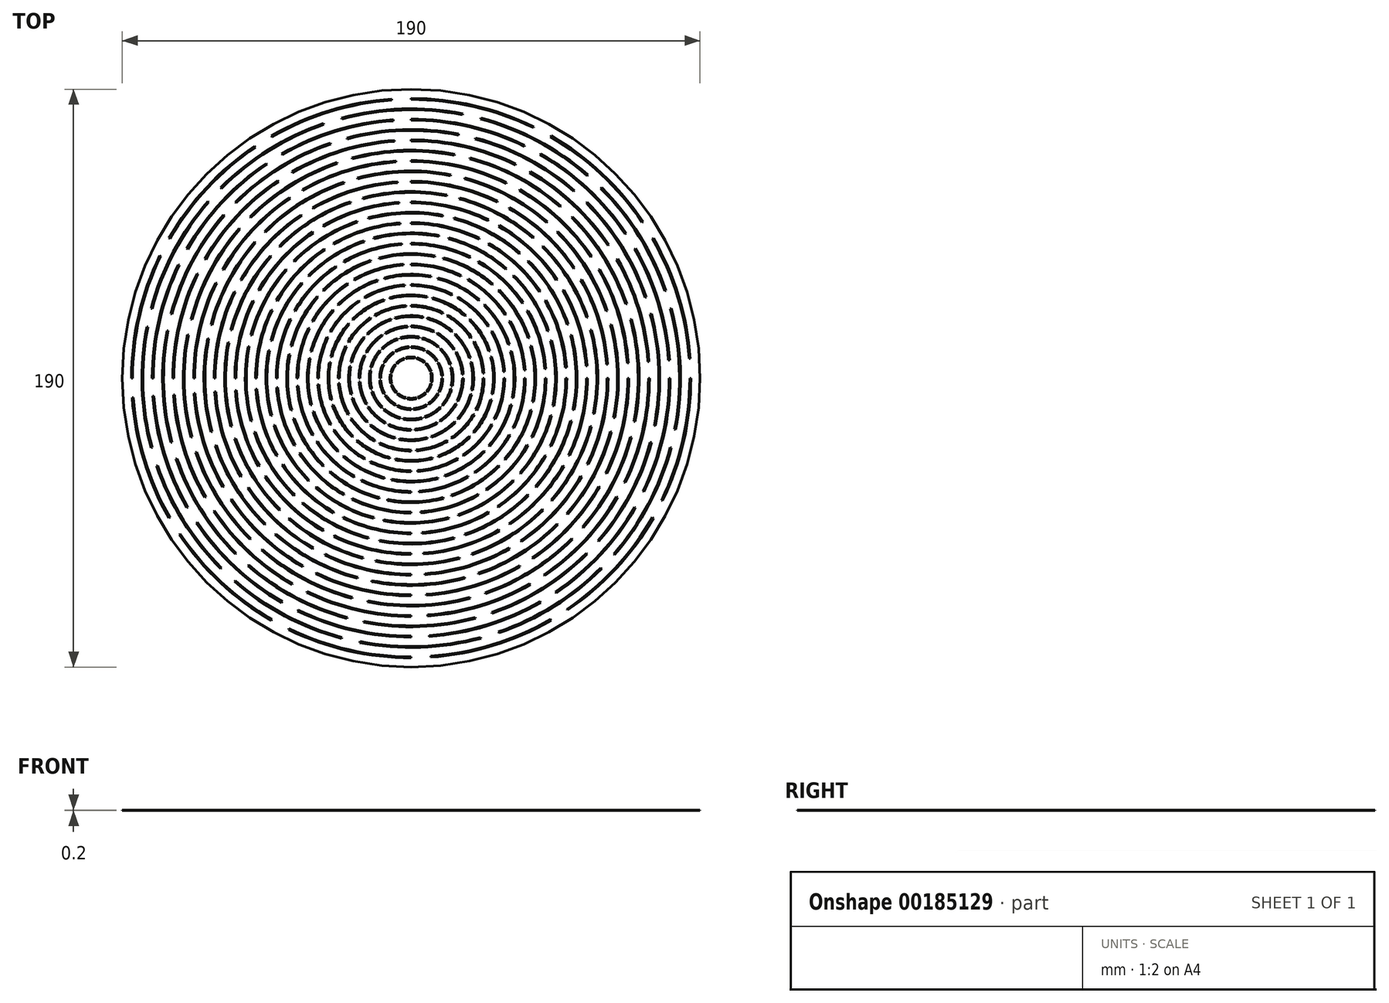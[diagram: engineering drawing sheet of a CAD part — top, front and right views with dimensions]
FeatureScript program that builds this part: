
annotation { "Feature Type Name" : "Feature", "Feature Type Description" : "" }
export const myFeature = defineFeature(function(context is Context, id is Id, definition is map)
    precondition{}
    {
        {
            assignVariable(context, id + "F0", {"name" : "T", "anyValue" : 0.2});
        }
        {
            var Q0;
            Q0=qCreatedBy(makeId("Top.planeOp"),FACE);
            var sketch = newSketch(context, id + "F1", { "sketchPlane" : qUnion([Q0])});
            skCircle(sketch, "E0", {"center": v(0, 0) * mm, "radius": 95 * mm});
            skPoint(sketch, "E1", {"position": v(-95, 0) * mm});
            skPoint(sketch, "E2", {"position": v(-92, 0) * mm});
            skPoint(sketch, "E3.1.0.0", {"position": v(-88.6, 0) * mm});
            skPoint(sketch, "E3.1.0.1", {"position": v(-91.6, 0) * mm});
            skPoint(sketch, "E3.2.0.0", {"position": v(-85.2, 0) * mm});
            skPoint(sketch, "E3.2.0.1", {"position": v(-88.2, 0) * mm});
            skPoint(sketch, "E3.3.0.0", {"position": v(-81.8, 0) * mm});
            skPoint(sketch, "E3.3.0.1", {"position": v(-84.8, 0) * mm});
            skPoint(sketch, "E3.4.0.0", {"position": v(-78.4, 0) * mm});
            skPoint(sketch, "E3.4.0.1", {"position": v(-81.4, 0) * mm});
            skPoint(sketch, "E3.5.0.0", {"position": v(-75, 0) * mm});
            skPoint(sketch, "E3.5.0.1", {"position": v(-78, 0) * mm});
            skPoint(sketch, "E3.6.0.0", {"position": v(-71.6, 0) * mm});
            skPoint(sketch, "E3.6.0.1", {"position": v(-74.6, 0) * mm});
            skPoint(sketch, "E3.7.0.0", {"position": v(-68.2, 0) * mm});
            skPoint(sketch, "E3.7.0.1", {"position": v(-71.2, 0) * mm});
            skPoint(sketch, "E3.8.0.0", {"position": v(-64.8, 0) * mm});
            skPoint(sketch, "E3.8.0.1", {"position": v(-67.8, 0) * mm});
            skPoint(sketch, "E3.9.0.0", {"position": v(-61.4, 0) * mm});
            skPoint(sketch, "E3.9.0.1", {"position": v(-64.4, 0) * mm});
            skPoint(sketch, "E3.10.0.0", {"position": v(-58, 0) * mm});
            skPoint(sketch, "E3.10.0.1", {"position": v(-61, 0) * mm});
            skPoint(sketch, "E3.11.0.0", {"position": v(-54.6, 0) * mm});
            skPoint(sketch, "E3.11.0.1", {"position": v(-57.6, 0) * mm});
            skPoint(sketch, "E3.12.0.0", {"position": v(-51.2, 0) * mm});
            skPoint(sketch, "E3.12.0.1", {"position": v(-54.2, 0) * mm});
            skPoint(sketch, "E3.13.0.0", {"position": v(-47.8, 0) * mm});
            skPoint(sketch, "E3.13.0.1", {"position": v(-50.8, 0) * mm});
            skPoint(sketch, "E3.14.0.0", {"position": v(-44.4, 0) * mm});
            skPoint(sketch, "E3.14.0.1", {"position": v(-47.4, 0) * mm});
            skPoint(sketch, "E3.15.0.0", {"position": v(-41, 0) * mm});
            skPoint(sketch, "E3.15.0.1", {"position": v(-44, 0) * mm});
            skPoint(sketch, "E3.16.0.0", {"position": v(-37.6, 0) * mm});
            skPoint(sketch, "E3.16.0.1", {"position": v(-40.6, 0) * mm});
            skPoint(sketch, "E3.17.0.0", {"position": v(-34.2, 0) * mm});
            skPoint(sketch, "E3.17.0.1", {"position": v(-37.2, 0) * mm});
            skPoint(sketch, "E3.18.0.0", {"position": v(-30.8, 0) * mm});
            skPoint(sketch, "E3.18.0.1", {"position": v(-33.8, 0) * mm});
            skPoint(sketch, "E3.19.0.0", {"position": v(-27.4, 0) * mm});
            skPoint(sketch, "E3.19.0.1", {"position": v(-30.4, 0) * mm});
            skPoint(sketch, "E3.20.0.0", {"position": v(-24, 0) * mm});
            skPoint(sketch, "E3.20.0.1", {"position": v(-27, 0) * mm});
            skPoint(sketch, "E3.21.0.0", {"position": v(-20.6, 0) * mm});
            skPoint(sketch, "E3.21.0.1", {"position": v(-23.6, 0) * mm});
            skPoint(sketch, "E3.22.0.0", {"position": v(-17.2, 0) * mm});
            skPoint(sketch, "E3.22.0.1", {"position": v(-20.2, 0) * mm});
            skPoint(sketch, "E3.23.0.0", {"position": v(-13.8, 0) * mm});
            skPoint(sketch, "E3.23.0.1", {"position": v(-16.8, 0) * mm});
            skPoint(sketch, "E3.24.0.0", {"position": v(-10.4, 0) * mm});
            skPoint(sketch, "E3.24.0.1", {"position": v(-13.4, 0) * mm});
            skPoint(sketch, "E3.25.0.0", {"position": v(-7, 0) * mm});
            skPoint(sketch, "E3.25.0.1", {"position": v(-10, 0) * mm});
            skLineSegment(sketch, "E3.direction1", {"start": v(-95, 0) * mm, "end": v(-91.6, 0) * mm, "construction": true});
            skArc(sketch, "E4", {"start": v(-92, 0) * mm, "mid": v(-89.64, 20.7) * mm, "end": v(-82.69, 40.33) * mm});
            skLineSegment(sketch, "E5", {"start": v(-82.69, 40.33) * mm, "end": v(0, 0) * mm, "construction": true});
            skLineSegment(sketch, "E6", {"start": v(0, 0) * mm, "end": v(-95, 0) * mm, "construction": true});
            skArc(sketch, "E7", {"start": v(-91.6, 0) * mm, "mid": v(-89.25, 20.6) * mm, "end": v(-82.33, 40.15) * mm});
            skLineSegment(sketch, "E8", {"start": v(-92, 0) * mm, "end": v(-91.6, 0) * mm});
            skLineSegment(sketch, "E9", {"start": v(-82.69, 40.33) * mm, "end": v(-82.33, 40.15) * mm});
            skArc(sketch, "E10", {"start": v(-88.6, 0) * mm, "mid": v(-88.2, 8.5) * mm, "end": v(-86.97, 16.9) * mm});
            skArc(sketch, "E11", {"start": v(-88.6, 0) * mm, "mid": v(-87.84, -11.56) * mm, "end": v(-85.58, -22.93) * mm});
            skLineSegment(sketch, "E12", {"start": v(-86.97, 16.9) * mm, "end": v(0, 0) * mm, "construction": true});
            skLineSegment(sketch, "E13", {"start": v(0, 0) * mm, "end": v(-85.58, -22.93) * mm, "construction": true});
            skArc(sketch, "E14", {"start": v(-88.2, 0) * mm, "mid": v(-87.8, 8.45) * mm, "end": v(-86.58, 16.83) * mm});
            skArc(sketch, "E15", {"start": v(-88.2, 0) * mm, "mid": v(-87.45, -11.51) * mm, "end": v(-85.2, -22.83) * mm});
            skLineSegment(sketch, "E16", {"start": v(-86.97, 16.9) * mm, "end": v(-86.58, 16.83) * mm});
            skLineSegment(sketch, "E17", {"start": v(-85.58, -22.93) * mm, "end": v(-85.2, -22.83) * mm});
            skArc(sketch, "E18", {"start": v(-85.2, 0) * mm, "mid": v(-83.02, 19.17) * mm, "end": v(-76.58, 37.35) * mm});
            skArc(sketch, "E19", {"start": v(-84.8, 0) * mm, "mid": v(-82.63, 19.08) * mm, "end": v(-76.22, 37.17) * mm});
            skLineSegment(sketch, "E20", {"start": v(-76.58, 37.35) * mm, "end": v(-76.22, 37.17) * mm});
            skLineSegment(sketch, "E21", {"start": v(-85.2, 0) * mm, "end": v(-84.8, 0) * mm});
            skArc(sketch, "E22", {"start": v(-81.8, 0) * mm, "mid": v(-81.42, 7.84) * mm, "end": v(-80.3, 15.6) * mm});
            skArc(sketch, "E23", {"start": v(-81.8, 0) * mm, "mid": v(-81.1, -10.68) * mm, "end": v(-79.01, -21.17) * mm});
            skArc(sketch, "E24", {"start": v(-81.4, 0) * mm, "mid": v(-81.03, 7.8) * mm, "end": v(-79.9, 15.53) * mm});
            skArc(sketch, "E25", {"start": v(-81.4, 0) * mm, "mid": v(-80.7, -10.62) * mm, "end": v(-78.63, -21.07) * mm});
            skLineSegment(sketch, "E26", {"start": v(-80.3, 15.6) * mm, "end": v(-79.9, 15.53) * mm});
            skLineSegment(sketch, "E27", {"start": v(-79.01, -21.17) * mm, "end": v(-78.63, -21.07) * mm});
            skArc(sketch, "E28", {"start": v(-78.4, 0) * mm, "mid": v(-76.4, 17.64) * mm, "end": v(-70.47, 34.37) * mm});
            skArc(sketch, "E29", {"start": v(-78, 0) * mm, "mid": v(-76, 17.55) * mm, "end": v(-70.1, 34.2) * mm});
            skLineSegment(sketch, "E30", {"start": v(-70.47, 34.37) * mm, "end": v(-70.1, 34.2) * mm});
            skLineSegment(sketch, "E31", {"start": v(-78.4, 0) * mm, "end": v(-78, 0) * mm});
            skArc(sketch, "E32", {"start": v(-75, 0) * mm, "mid": v(-74.65, 7.19) * mm, "end": v(-73.62, 14.31) * mm});
            skArc(sketch, "E33", {"start": v(-75, 0) * mm, "mid": v(-74.36, -9.79) * mm, "end": v(-72.44, -19.41) * mm});
            skArc(sketch, "E34", {"start": v(-74.6, 0) * mm, "mid": v(-74.26, 7.15) * mm, "end": v(-73.23, 14.23) * mm});
            skArc(sketch, "E35", {"start": v(-74.6, 0) * mm, "mid": v(-73.96, -9.74) * mm, "end": v(-72.06, -19.3) * mm});
            skLineSegment(sketch, "E36", {"start": v(-73.62, 14.31) * mm, "end": v(-73.23, 14.23) * mm});
            skLineSegment(sketch, "E37", {"start": v(-72.44, -19.41) * mm, "end": v(-72.06, -19.3) * mm});
            skArc(sketch, "E38", {"start": v(-71.6, 0) * mm, "mid": v(-69.76, 16.1) * mm, "end": v(-64.35, 31.39) * mm});
            skArc(sketch, "E39", {"start": v(-71.2, 0) * mm, "mid": v(-69.38, 16.02) * mm, "end": v(-64, 31.21) * mm});
            skLineSegment(sketch, "E40", {"start": v(-64.35, 31.39) * mm, "end": v(-64, 31.21) * mm});
            skLineSegment(sketch, "E41", {"start": v(-71.6, 0) * mm, "end": v(-71.2, 0) * mm});
            skArc(sketch, "E42", {"start": v(-68.2, 0) * mm, "mid": v(-67.89, 6.54) * mm, "end": v(-66.95, 13.01) * mm});
            skArc(sketch, "E43", {"start": v(-68.2, 0) * mm, "mid": v(-67.62, -8.9) * mm, "end": v(-65.88, -17.65) * mm});
            skArc(sketch, "E44", {"start": v(-67.8, 0) * mm, "mid": v(-67.49, 6.5) * mm, "end": v(-66.55, 12.94) * mm});
            skArc(sketch, "E45", {"start": v(-67.8, 0) * mm, "mid": v(-67.22, -8.85) * mm, "end": v(-65.49, -17.55) * mm});
            skLineSegment(sketch, "E46", {"start": v(-66.95, 13.01) * mm, "end": v(-66.55, 12.94) * mm});
            skLineSegment(sketch, "E47", {"start": v(-65.88, -17.65) * mm, "end": v(-65.49, -17.55) * mm});
            skArc(sketch, "E48", {"start": v(-64.8, 0) * mm, "mid": v(-63.14, 14.58) * mm, "end": v(-58.24, 28.4) * mm});
            skArc(sketch, "E49", {"start": v(-64.4, 0) * mm, "mid": v(-62.75, 14.49) * mm, "end": v(-57.88, 28.23) * mm});
            skLineSegment(sketch, "E50", {"start": v(-58.24, 28.4) * mm, "end": v(-57.88, 28.23) * mm});
            skLineSegment(sketch, "E51", {"start": v(-64.8, 0) * mm, "end": v(-64.4, 0) * mm});
            skArc(sketch, "E52", {"start": v(-61.4, 0) * mm, "mid": v(-61.12, 5.88) * mm, "end": v(-60.27, 11.72) * mm});
            skArc(sketch, "E53", {"start": v(-61.4, 0) * mm, "mid": v(-60.87, -8.01) * mm, "end": v(-59.3, -15.9) * mm});
            skArc(sketch, "E54", {"start": v(-61, 0) * mm, "mid": v(-60.72, 5.85) * mm, "end": v(-59.88, 11.64) * mm});
            skArc(sketch, "E55", {"start": v(-61, 0) * mm, "mid": v(-60.48, -7.96) * mm, "end": v(-58.92, -15.79) * mm});
            skLineSegment(sketch, "E56", {"start": v(-60.27, 11.72) * mm, "end": v(-59.88, 11.64) * mm});
            skLineSegment(sketch, "E57", {"start": v(-59.3, -15.9) * mm, "end": v(-58.92, -15.79) * mm});
            skArc(sketch, "E58", {"start": v(-58, 0) * mm, "mid": v(-56.51, 13.05) * mm, "end": v(-52.13, 25.43) * mm});
            skArc(sketch, "E59", {"start": v(-57.6, 0) * mm, "mid": v(-56.12, 12.96) * mm, "end": v(-51.77, 25.25) * mm});
            skLineSegment(sketch, "E60", {"start": v(-52.13, 25.43) * mm, "end": v(-51.77, 25.25) * mm});
            skLineSegment(sketch, "E61", {"start": v(-58, 0) * mm, "end": v(-57.6, 0) * mm});
            skArc(sketch, "E62", {"start": v(-54.6, 0) * mm, "mid": v(-54.35, 5.23) * mm, "end": v(-53.6, 10.42) * mm});
            skArc(sketch, "E63", {"start": v(-54.6, 0) * mm, "mid": v(-54.13, -7.13) * mm, "end": v(-52.74, -14.13) * mm});
            skArc(sketch, "E64", {"start": v(-54.2, 0) * mm, "mid": v(-53.95, 5.2) * mm, "end": v(-53.2, 10.34) * mm});
            skArc(sketch, "E65", {"start": v(-54.2, 0) * mm, "mid": v(-53.74, -7.07) * mm, "end": v(-52.35, -14.03) * mm});
            skLineSegment(sketch, "E66", {"start": v(-53.6, 10.42) * mm, "end": v(-53.2, 10.34) * mm});
            skLineSegment(sketch, "E67", {"start": v(-52.74, -14.13) * mm, "end": v(-52.35, -14.03) * mm});
            skArc(sketch, "E68", {"start": v(-51.2, 0) * mm, "mid": v(-49.89, 11.52) * mm, "end": v(-46.02, 22.44) * mm});
            skArc(sketch, "E69", {"start": v(-50.8, 0) * mm, "mid": v(-49.5, 11.43) * mm, "end": v(-45.66, 22.27) * mm});
            skLineSegment(sketch, "E70", {"start": v(-46.02, 22.44) * mm, "end": v(-45.66, 22.27) * mm});
            skLineSegment(sketch, "E71", {"start": v(-51.2, 0) * mm, "end": v(-50.8, 0) * mm});
            skArc(sketch, "E72", {"start": v(-47.8, 0) * mm, "mid": v(-47.58, 4.58) * mm, "end": v(-46.92, 9.12) * mm});
            skArc(sketch, "E73", {"start": v(-47.8, 0) * mm, "mid": v(-47.4, -6.24) * mm, "end": v(-46.17, -12.37) * mm});
            skArc(sketch, "E74", {"start": v(-47.4, 0) * mm, "mid": v(-47.18, 4.54) * mm, "end": v(-46.53, 9.04) * mm});
            skArc(sketch, "E75", {"start": v(-47.4, 0) * mm, "mid": v(-47, -6.19) * mm, "end": v(-45.78, -12.27) * mm});
            skLineSegment(sketch, "E76", {"start": v(-46.92, 9.12) * mm, "end": v(-46.53, 9.04) * mm});
            skLineSegment(sketch, "E77", {"start": v(-46.17, -12.37) * mm, "end": v(-45.78, -12.27) * mm});
            skArc(sketch, "E78", {"start": v(-44.4, 0) * mm, "mid": v(-43.26, 9.99) * mm, "end": v(-39.9, 19.46) * mm});
            skArc(sketch, "E79", {"start": v(-44, 0) * mm, "mid": v(-42.87, 9.9) * mm, "end": v(-39.55, 19.29) * mm});
            skLineSegment(sketch, "E80", {"start": v(-39.9, 19.46) * mm, "end": v(-39.55, 19.29) * mm});
            skLineSegment(sketch, "E81", {"start": v(-44.4, 0) * mm, "end": v(-44, 0) * mm});
            skArc(sketch, "E82", {"start": v(-41, 0) * mm, "mid": v(-40.81, 3.93) * mm, "end": v(-40.25, 7.82) * mm});
            skArc(sketch, "E83", {"start": v(-41, 0) * mm, "mid": v(-40.65, -5.35) * mm, "end": v(-39.6, -10.61) * mm});
            skArc(sketch, "E84", {"start": v(-40.6, 0) * mm, "mid": v(-40.41, 3.9) * mm, "end": v(-39.85, 7.75) * mm});
            skArc(sketch, "E85", {"start": v(-40.6, 0) * mm, "mid": v(-40.25, -5.3) * mm, "end": v(-39.22, -10.5) * mm});
            skLineSegment(sketch, "E86", {"start": v(-40.25, 7.82) * mm, "end": v(-39.85, 7.75) * mm});
            skLineSegment(sketch, "E87", {"start": v(-39.6, -10.61) * mm, "end": v(-39.22, -10.5) * mm});
            skArc(sketch, "E88", {"start": v(-37.6, 0) * mm, "mid": v(-36.64, 8.46) * mm, "end": v(-33.8, 16.48) * mm});
            skArc(sketch, "E89", {"start": v(-37.2, 0) * mm, "mid": v(-36.25, 8.37) * mm, "end": v(-33.44, 16.3) * mm});
            skLineSegment(sketch, "E90", {"start": v(-33.8, 16.48) * mm, "end": v(-33.44, 16.3) * mm});
            skLineSegment(sketch, "E91", {"start": v(-37.6, 0) * mm, "end": v(-37.2, 0) * mm});
            skArc(sketch, "E92", {"start": v(-34.2, 0) * mm, "mid": v(-34.04, 3.28) * mm, "end": v(-33.57, 6.53) * mm});
            skArc(sketch, "E93", {"start": v(-34.2, 0) * mm, "mid": v(-33.9, -4.46) * mm, "end": v(-33.03, -8.85) * mm});
            skArc(sketch, "E94", {"start": v(-33.8, 0) * mm, "mid": v(-33.64, 3.24) * mm, "end": v(-33.18, 6.45) * mm});
            skArc(sketch, "E95", {"start": v(-33.8, 0) * mm, "mid": v(-33.51, -4.41) * mm, "end": v(-32.65, -8.75) * mm});
            skLineSegment(sketch, "E96", {"start": v(-33.57, 6.53) * mm, "end": v(-33.18, 6.45) * mm});
            skLineSegment(sketch, "E97", {"start": v(-33.03, -8.85) * mm, "end": v(-32.65, -8.75) * mm});
            skArc(sketch, "E98", {"start": v(-30.8, 0) * mm, "mid": v(-30.01, 6.93) * mm, "end": v(-27.68, 13.5) * mm});
            skArc(sketch, "E99", {"start": v(-30.4, 0) * mm, "mid": v(-29.62, 6.84) * mm, "end": v(-27.32, 13.33) * mm});
            skLineSegment(sketch, "E100", {"start": v(-27.68, 13.5) * mm, "end": v(-27.32, 13.33) * mm});
            skLineSegment(sketch, "E101", {"start": v(-30.8, 0) * mm, "end": v(-30.4, 0) * mm});
            skArc(sketch, "E102", {"start": v(-27.4, 0) * mm, "mid": v(-27.27, 2.63) * mm, "end": v(-26.9, 5.23) * mm});
            skArc(sketch, "E103", {"start": v(-27, 0) * mm, "mid": v(-26.88, 2.59) * mm, "end": v(-26.5, 5.15) * mm});
            skArc(sketch, "E104", {"start": v(-27.4, 0) * mm, "mid": v(-27.17, -3.58) * mm, "end": v(-26.47, -7.1) * mm});
            skArc(sketch, "E105", {"start": v(-27, 0) * mm, "mid": v(-26.77, -3.52) * mm, "end": v(-26.08, -6.99) * mm});
            skLineSegment(sketch, "E106", {"start": v(-26.9, 5.23) * mm, "end": v(-26.5, 5.15) * mm});
            skLineSegment(sketch, "E107", {"start": v(-26.47, -7.1) * mm, "end": v(-26.08, -6.99) * mm});
            skArc(sketch, "E108", {"start": v(-24, 0) * mm, "mid": v(-23.38, 5.4) * mm, "end": v(-21.57, 10.52) * mm});
            skArc(sketch, "E109", {"start": v(-23.6, 0) * mm, "mid": v(-23, 5.3) * mm, "end": v(-21.21, 10.35) * mm});
            skLineSegment(sketch, "E110", {"start": v(-21.57, 10.52) * mm, "end": v(-21.21, 10.35) * mm});
            skLineSegment(sketch, "E111", {"start": v(-24, 0) * mm, "end": v(-23.6, 0) * mm});
            skArc(sketch, "E112", {"start": v(-20.6, 0) * mm, "mid": v(-20.5, 1.97) * mm, "end": v(-20.22, 3.93) * mm});
            skArc(sketch, "E113", {"start": v(-20.6, 0) * mm, "mid": v(-20.42, -2.69) * mm, "end": v(-19.9, -5.33) * mm});
            skArc(sketch, "E114", {"start": v(-20.2, 0) * mm, "mid": v(-20.1, 1.94) * mm, "end": v(-19.83, 3.85) * mm});
            skArc(sketch, "E115", {"start": v(-20.2, 0) * mm, "mid": v(-20.03, -2.64) * mm, "end": v(-19.51, -5.23) * mm});
            skLineSegment(sketch, "E116", {"start": v(-20.22, 3.93) * mm, "end": v(-19.83, 3.85) * mm});
            skLineSegment(sketch, "E117", {"start": v(-19.9, -5.33) * mm, "end": v(-19.51, -5.23) * mm});
            skArc(sketch, "E118", {"start": v(-17.2, 0) * mm, "mid": v(-16.76, 3.87) * mm, "end": v(-15.46, 7.54) * mm});
            skArc(sketch, "E119", {"start": v(-16.8, 0) * mm, "mid": v(-16.37, 3.78) * mm, "end": v(-15.1, 7.36) * mm});
            skLineSegment(sketch, "E120", {"start": v(-15.46, 7.54) * mm, "end": v(-15.1, 7.36) * mm});
            skLineSegment(sketch, "E121", {"start": v(-17.2, 0) * mm, "end": v(-16.8, 0) * mm});
            skArc(sketch, "E122", {"start": v(-13.8, 0) * mm, "mid": v(-13.74, 1.32) * mm, "end": v(-13.55, 2.63) * mm});
            skArc(sketch, "E123", {"start": v(-13.8, 0) * mm, "mid": v(-13.68, -1.8) * mm, "end": v(-13.33, -3.57) * mm});
            skArc(sketch, "E124", {"start": v(-13.4, 0) * mm, "mid": v(-13.34, 1.28) * mm, "end": v(-13.15, 2.56) * mm});
            skArc(sketch, "E125", {"start": v(-13.4, 0) * mm, "mid": v(-13.29, -1.75) * mm, "end": v(-12.94, -3.47) * mm});
            skLineSegment(sketch, "E126", {"start": v(-13.55, 2.63) * mm, "end": v(-13.15, 2.56) * mm});
            skLineSegment(sketch, "E127", {"start": v(-13.33, -3.57) * mm, "end": v(-12.94, -3.47) * mm});
            skArc(sketch, "E128", {"start": v(-10.4, 0) * mm, "mid": v(-10.13, 2.34) * mm, "end": v(-9.35, 4.56) * mm});
            skArc(sketch, "E129", {"start": v(-10, 0) * mm, "mid": v(-9.74, 2.25) * mm, "end": v(-8.99, 4.38) * mm});
            skLineSegment(sketch, "E130", {"start": v(-9.35, 4.56) * mm, "end": v(-8.99, 4.38) * mm});
            skLineSegment(sketch, "E131", {"start": v(-10.4, 0) * mm, "end": v(-10, 0) * mm});
            skArc(sketch, "E132", {"start": v(-7, 0) * mm, "mid": v(-6.97, 0.67) * mm, "end": v(-6.87, 1.34) * mm});
            skArc(sketch, "E133", {"start": v(-7, 0) * mm, "mid": v(-6.94, -0.91) * mm, "end": v(-6.76, -1.81) * mm});
            skArc(sketch, "E134", {"start": v(-6.38, -1.7) * mm, "mid": v(-6.6, -0.23) * mm, "end": v(-6.48, 1.26) * mm});
            skLineSegment(sketch, "E135", {"start": v(-6.87, 1.34) * mm, "end": v(-6.48, 1.26) * mm});
            skLineSegment(sketch, "E136", {"start": v(-6.76, -1.81) * mm, "end": v(-6.38, -1.7) * mm});
            skArc(sketch, "E137.1.0", {"start": v(-17.84, 10.3) * mm, "mid": v(-19.03, 7.88) * mm, "end": v(-19.9, 5.33) * mm});
            skArc(sketch, "E137.1.1", {"start": v(-14.9, 8.6) * mm, "mid": v(-12.58, 11.73) * mm, "end": v(-9.62, 14.26) * mm});
            skArc(sketch, "E137.1.2", {"start": v(-17.5, 10.1) * mm, "mid": v(-18.66, 7.73) * mm, "end": v(-19.51, 5.23) * mm});
            skArc(sketch, "E137.1.3", {"start": v(-55.77, 32.2) * mm, "mid": v(-47.1, 43.92) * mm, "end": v(-36.01, 53.4) * mm});
            skArc(sketch, "E137.1.4", {"start": v(-70.5, 40.7) * mm, "mid": v(-75.2, 31.15) * mm, "end": v(-78.63, 21.07) * mm});
            skArc(sketch, "E137.1.5", {"start": v(-17.5, 10.1) * mm, "mid": v(-16.45, 11.73) * mm, "end": v(-15.25, 13.25) * mm});
            skArc(sketch, "E137.1.6", {"start": v(-67.9, 39.2) * mm, "mid": v(-57.34, 53.47) * mm, "end": v(-43.84, 65) * mm});
            skArc(sketch, "E137.1.7", {"start": v(-9, 5.2) * mm, "mid": v(-7.6, 7.1) * mm, "end": v(-5.82, 8.62) * mm});
            skArc(sketch, "E137.1.8", {"start": v(-32.56, 18.8) * mm, "mid": v(-27.5, 25.64) * mm, "end": v(-21.03, 31.17) * mm});
            skArc(sketch, "E137.1.9", {"start": v(-79.67, 46) * mm, "mid": v(-67.28, 62.74) * mm, "end": v(-51.45, 76.27) * mm});
            skArc(sketch, "E137.1.10", {"start": v(-23.73, 13.7) * mm, "mid": v(-22.3, 15.91) * mm, "end": v(-20.68, 17.98) * mm});
            skArc(sketch, "E137.1.11", {"start": v(-23.73, 13.7) * mm, "mid": v(-25.31, 10.49) * mm, "end": v(-26.47, 7.1) * mm});
            skArc(sketch, "E137.1.12", {"start": v(-76.73, 44.3) * mm, "mid": v(-81.86, 33.9) * mm, "end": v(-85.58, 22.93) * mm});
            skArc(sketch, "E137.1.13", {"start": v(-73.79, 42.6) * mm, "mid": v(-62.31, 58.1) * mm, "end": v(-47.64, 70.63) * mm});
            skArc(sketch, "E137.1.14", {"start": v(-47.28, 27.3) * mm, "mid": v(-50.44, 20.9) * mm, "end": v(-52.74, 14.13) * mm});
            skArc(sketch, "E137.1.15", {"start": v(-46.94, 27.1) * mm, "mid": v(-50.07, 20.74) * mm, "end": v(-52.35, 14.03) * mm});
            skArc(sketch, "E137.1.16", {"start": v(-79.33, 45.8) * mm, "mid": v(-67, 62.47) * mm, "end": v(-51.22, 75.94) * mm});
            skArc(sketch, "E137.1.17", {"start": v(-70.5, 40.7) * mm, "mid": v(-66.27, 47.27) * mm, "end": v(-61.43, 53.4) * mm});
            skArc(sketch, "E137.1.18", {"start": v(-26.67, 15.4) * mm, "mid": v(-22.53, 21) * mm, "end": v(-17.22, 25.53) * mm});
            skArc(sketch, "E137.1.19", {"start": v(-50.23, 29) * mm, "mid": v(-42.42, 39.56) * mm, "end": v(-32.43, 48.08) * mm});
            skArc(sketch, "E137.1.20", {"start": v(-49.88, 28.8) * mm, "mid": v(-42.13, 39.28) * mm, "end": v(-32.2, 47.75) * mm});
            skArc(sketch, "E137.1.21", {"start": v(-56.12, 32.4) * mm, "mid": v(-47.4, 44.2) * mm, "end": v(-36.24, 53.72) * mm});
            skArc(sketch, "E137.1.22", {"start": v(-35.5, 20.5) * mm, "mid": v(-37.88, 15.7) * mm, "end": v(-39.6, 10.61) * mm});
            skArc(sketch, "E137.1.23", {"start": v(-8.66, 5) * mm, "mid": v(-7.31, 6.82) * mm, "end": v(-5.6, 8.3) * mm});
            skArc(sketch, "E137.1.24", {"start": v(-11.95, 6.9) * mm, "mid": v(-12.75, 5.28) * mm, "end": v(-13.33, 3.57) * mm});
            skArc(sketch, "E137.1.25", {"start": v(-23.38, 13.5) * mm, "mid": v(-21.98, 15.68) * mm, "end": v(-20.38, 17.71) * mm});
            skArc(sketch, "E137.1.26", {"start": v(-29.27, 16.9) * mm, "mid": v(-31.23, 12.93) * mm, "end": v(-32.65, 8.75) * mm});
            skArc(sketch, "E137.1.27", {"start": v(-62, 35.8) * mm, "mid": v(-52.36, 48.83) * mm, "end": v(-40.04, 59.36) * mm});
            skArc(sketch, "E137.1.28", {"start": v(-41.4, 23.9) * mm, "mid": v(-38.91, 27.76) * mm, "end": v(-36.08, 31.36) * mm});
            skArc(sketch, "E137.1.29", {"start": v(-11.6, 6.7) * mm, "mid": v(-12.38, 5.13) * mm, "end": v(-12.94, 3.47) * mm});
            skArc(sketch, "E137.1.30", {"start": v(-46.94, 27.1) * mm, "mid": v(-44.13, 31.47) * mm, "end": v(-40.9, 35.56) * mm});
            skArc(sketch, "E137.1.31", {"start": v(-70.84, 40.9) * mm, "mid": v(-66.6, 47.5) * mm, "end": v(-61.74, 53.67) * mm});
            skArc(sketch, "E137.1.32", {"start": v(-64.95, 37.5) * mm, "mid": v(-61.06, 43.55) * mm, "end": v(-56.6, 49.2) * mm});
            skArc(sketch, "E137.1.33", {"start": v(-29.62, 17.1) * mm, "mid": v(-27.84, 19.86) * mm, "end": v(-25.81, 22.44) * mm});
            skArc(sketch, "E137.1.34", {"start": v(-29.27, 16.9) * mm, "mid": v(-27.52, 19.63) * mm, "end": v(-25.5, 22.17) * mm});
            skArc(sketch, "E137.1.35", {"start": v(-35.16, 20.3) * mm, "mid": v(-37.5, 15.54) * mm, "end": v(-39.22, 10.5) * mm});
            skArc(sketch, "E137.1.36", {"start": v(-73.44, 42.4) * mm, "mid": v(-62.02, 57.83) * mm, "end": v(-47.42, 70.3) * mm});
            skArc(sketch, "E137.1.37", {"start": v(-20.44, 11.8) * mm, "mid": v(-17.26, 16.1) * mm, "end": v(-13.2, 19.57) * mm});
            skArc(sketch, "E137.1.38", {"start": v(-6.06, 3.5) * mm, "mid": v(-6.47, 2.68) * mm, "end": v(-6.76, 1.81) * mm});
            skArc(sketch, "E137.1.39", {"start": v(-70.84, 40.9) * mm, "mid": v(-75.57, 31.3) * mm, "end": v(-79.01, 21.17) * mm});
            skArc(sketch, "E137.1.40", {"start": v(-44.34, 25.6) * mm, "mid": v(-37.45, 34.92) * mm, "end": v(-28.63, 42.45) * mm});
            skArc(sketch, "E137.1.41", {"start": v(-38.45, 22.2) * mm, "mid": v(-32.47, 30.28) * mm, "end": v(-24.83, 36.8) * mm});
            skArc(sketch, "E137.1.42", {"start": v(-53.17, 30.7) * mm, "mid": v(-49.99, 35.66) * mm, "end": v(-46.34, 40.28) * mm});
            skArc(sketch, "E137.1.43", {"start": v(-41.4, 23.9) * mm, "mid": v(-44.16, 18.3) * mm, "end": v(-46.17, 12.37) * mm});
            skArc(sketch, "E137.1.44", {"start": v(-23.38, 13.5) * mm, "mid": v(-24.94, 10.33) * mm, "end": v(-26.08, 6.99) * mm});
            skArc(sketch, "E137.1.45", {"start": v(-11.6, 6.7) * mm, "mid": v(-10.9, 7.78) * mm, "end": v(-10.11, 8.8) * mm});
            skArc(sketch, "E137.1.46", {"start": v(-32.22, 18.6) * mm, "mid": v(-27.2, 25.37) * mm, "end": v(-20.8, 30.84) * mm});
            skArc(sketch, "E137.1.47", {"start": v(-59.06, 34.1) * mm, "mid": v(-55.52, 39.6) * mm, "end": v(-51.47, 44.74) * mm});
            skArc(sketch, "E137.1.48", {"start": v(-52.83, 30.5) * mm, "mid": v(-49.66, 35.42) * mm, "end": v(-46.04, 40.02) * mm});
            skArc(sketch, "E137.1.49", {"start": v(-76.73, 44.3) * mm, "mid": v(-72.13, 51.45) * mm, "end": v(-66.87, 58.13) * mm});
            skArc(sketch, "E137.1.50", {"start": v(-58.72, 33.9) * mm, "mid": v(-55.2, 39.37) * mm, "end": v(-51.17, 44.48) * mm});
            skArc(sketch, "E137.1.51", {"start": v(-67.55, 39) * mm, "mid": v(-57.05, 53.2) * mm, "end": v(-43.62, 64.66) * mm});
            skArc(sketch, "E137.1.52", {"start": v(-14.55, 8.4) * mm, "mid": v(-12.29, 11.46) * mm, "end": v(-9.4, 13.93) * mm});
            skArc(sketch, "E137.1.53", {"start": v(-44, 25.4) * mm, "mid": v(-37.15, 34.65) * mm, "end": v(-28.4, 42.12) * mm});
            skArc(sketch, "E137.1.54", {"start": v(-41.05, 23.7) * mm, "mid": v(-38.59, 27.53) * mm, "end": v(-35.77, 31.1) * mm});
            skArc(sketch, "E137.1.55", {"start": v(-38.1, 22) * mm, "mid": v(-32.18, 30) * mm, "end": v(-24.6, 36.48) * mm});
            skArc(sketch, "E137.1.56", {"start": v(-59.06, 34.1) * mm, "mid": v(-63, 26.1) * mm, "end": v(-65.88, 17.65) * mm});
            skArc(sketch, "E137.1.57", {"start": v(-76.38, 44.1) * mm, "mid": v(-71.8, 51.22) * mm, "end": v(-66.57, 57.86) * mm});
            skArc(sketch, "E137.1.58", {"start": v(-64.6, 37.3) * mm, "mid": v(-60.73, 43.32) * mm, "end": v(-56.3, 48.94) * mm});
            skLineSegment(sketch, "E137.1.59", {"start": v(-51.45, 76.27) * mm, "end": v(-51.22, 75.94) * mm});
            skArc(sketch, "E137.1.60", {"start": v(-64.95, 37.5) * mm, "mid": v(-69.3, 28.7) * mm, "end": v(-72.44, 19.41) * mm});
            skArc(sketch, "E137.1.61", {"start": v(-64.6, 37.3) * mm, "mid": v(-68.92, 28.55) * mm, "end": v(-72.06, 19.3) * mm});
            skArc(sketch, "E137.1.62", {"start": v(-76.38, 44.1) * mm, "mid": v(-81.49, 33.75) * mm, "end": v(-85.2, 22.83) * mm});
            skArc(sketch, "E137.1.63", {"start": v(-6.06, 3.5) * mm, "mid": v(-5.7, 4.06) * mm, "end": v(-5.28, 4.6) * mm});
            skArc(sketch, "E137.1.64", {"start": v(-35.5, 20.5) * mm, "mid": v(-33.38, 23.8) * mm, "end": v(-30.94, 26.9) * mm});
            skArc(sketch, "E137.1.65", {"start": v(-58.72, 33.9) * mm, "mid": v(-62.64, 25.95) * mm, "end": v(-65.49, 17.55) * mm});
            skArc(sketch, "E137.1.66", {"start": v(-47.28, 27.3) * mm, "mid": v(-44.45, 31.7) * mm, "end": v(-41.2, 35.82) * mm});
            skArc(sketch, "E137.1.67", {"start": v(-17.84, 10.3) * mm, "mid": v(-16.77, 11.96) * mm, "end": v(-15.55, 13.51) * mm});
            skArc(sketch, "E137.1.68", {"start": v(-11.95, 6.9) * mm, "mid": v(-11.23, 8.01) * mm, "end": v(-10.41, 9.05) * mm});
            skArc(sketch, "E137.1.69", {"start": v(-20.78, 12) * mm, "mid": v(-17.55, 16.37) * mm, "end": v(-13.42, 19.9) * mm});
            skArc(sketch, "E137.1.70", {"start": v(-26.33, 15.2) * mm, "mid": v(-22.23, 20.73) * mm, "end": v(-17, 25.2) * mm});
            skArc(sketch, "E137.1.71", {"start": v(-53.17, 30.7) * mm, "mid": v(-56.73, 23.5) * mm, "end": v(-59.3, 15.9) * mm});
            skArc(sketch, "E137.1.72", {"start": v(-6.38, 1.7) * mm, "mid": v(-5.83, 3.1) * mm, "end": v(-4.98, 4.33) * mm});
            skArc(sketch, "E137.1.73", {"start": v(-52.83, 30.5) * mm, "mid": v(-56.36, 23.34) * mm, "end": v(-58.92, 15.79) * mm});
            skArc(sketch, "E137.1.74", {"start": v(-41.05, 23.7) * mm, "mid": v(-43.8, 18.14) * mm, "end": v(-45.78, 12.27) * mm});
            skArc(sketch, "E137.1.75", {"start": v(-29.62, 17.1) * mm, "mid": v(-31.6, 13.09) * mm, "end": v(-33.03, 8.85) * mm});
            skArc(sketch, "E137.1.76", {"start": v(-35.16, 20.3) * mm, "mid": v(-33.05, 23.58) * mm, "end": v(-30.64, 26.64) * mm});
            skArc(sketch, "E137.1.77", {"start": v(-61.66, 35.6) * mm, "mid": v(-52.07, 48.56) * mm, "end": v(-39.81, 59.03) * mm});
            skArc(sketch, "E137.2.0", {"start": v(-10.3, 17.84) * mm, "mid": v(-12.54, 16.34) * mm, "end": v(-14.57, 14.57) * mm});
            skArc(sketch, "E137.2.1", {"start": v(-8.6, 14.9) * mm, "mid": v(-5.03, 16.45) * mm, "end": v(-1.2, 17.16) * mm});
            skArc(sketch, "E137.2.2", {"start": v(-10.1, 17.5) * mm, "mid": v(-12.3, 16.03) * mm, "end": v(-14.28, 14.28) * mm});
            skArc(sketch, "E137.2.3", {"start": v(-32.2, 55.77) * mm, "mid": v(-18.83, 61.59) * mm, "end": v(-4.5, 64.24) * mm});
            skArc(sketch, "E137.2.4", {"start": v(-40.7, 70.5) * mm, "mid": v(-49.55, 64.58) * mm, "end": v(-57.56, 57.56) * mm});
            skArc(sketch, "E137.2.5", {"start": v(-10.1, 17.5) * mm, "mid": v(-8.38, 18.38) * mm, "end": v(-6.58, 19.1) * mm});
            skArc(sketch, "E137.2.6", {"start": v(-39.2, 67.9) * mm, "mid": v(-22.92, 74.97) * mm, "end": v(-5.47, 78.2) * mm});
            skArc(sketch, "E137.2.7", {"start": v(-5.2, 9) * mm, "mid": v(-3.04, 9.95) * mm, "end": v(-0.73, 10.37) * mm});
            skArc(sketch, "E137.2.8", {"start": v(-18.8, 32.56) * mm, "mid": v(-11, 35.96) * mm, "end": v(-2.62, 37.5) * mm});
            skArc(sketch, "E137.2.9", {"start": v(-46, 79.67) * mm, "mid": v(-26.9, 87.98) * mm, "end": v(-6.42, 91.78) * mm});
            skArc(sketch, "E137.2.10", {"start": v(-13.7, 23.73) * mm, "mid": v(-11.36, 24.93) * mm, "end": v(-8.92, 25.9) * mm});
            skArc(sketch, "E137.2.11", {"start": v(-13.7, 23.73) * mm, "mid": v(-16.68, 21.74) * mm, "end": v(-19.37, 19.37) * mm});
            skArc(sketch, "E137.2.12", {"start": v(-44.3, 76.73) * mm, "mid": v(-53.94, 70.3) * mm, "end": v(-62.65, 62.65) * mm});
            skArc(sketch, "E137.2.13", {"start": v(-42.6, 73.79) * mm, "mid": v(-24.91, 81.48) * mm, "end": v(-5.94, 85) * mm});
            skArc(sketch, "E137.2.14", {"start": v(-27.3, 47.28) * mm, "mid": v(-33.24, 43.32) * mm, "end": v(-38.6, 38.6) * mm});
            skArc(sketch, "E137.2.15", {"start": v(-27.1, 46.94) * mm, "mid": v(-33, 43) * mm, "end": v(-38.33, 38.33) * mm});
            skArc(sketch, "E137.2.16", {"start": v(-45.8, 79.33) * mm, "mid": v(-26.78, 87.6) * mm, "end": v(-6.39, 91.38) * mm});
            skArc(sketch, "E137.2.17", {"start": v(-40.7, 70.5) * mm, "mid": v(-33.76, 74.07) * mm, "end": v(-26.5, 76.97) * mm});
            skArc(sketch, "E137.2.18", {"start": v(-15.4, 26.67) * mm, "mid": v(-9, 29.45) * mm, "end": v(-2.15, 30.72) * mm});
            skArc(sketch, "E137.2.19", {"start": v(-29, 50.23) * mm, "mid": v(-16.96, 55.47) * mm, "end": v(-4.05, 57.86) * mm});
            skArc(sketch, "E137.2.20", {"start": v(-28.8, 49.88) * mm, "mid": v(-16.84, 55.08) * mm, "end": v(-4.02, 57.46) * mm});
            skArc(sketch, "E137.2.21", {"start": v(-32.4, 56.12) * mm, "mid": v(-18.95, 61.97) * mm, "end": v(-4.52, 64.64) * mm});
            skArc(sketch, "E137.2.22", {"start": v(-20.5, 35.5) * mm, "mid": v(-24.96, 32.53) * mm, "end": v(-29, 29) * mm});
            skArc(sketch, "E137.2.23", {"start": v(-5, 8.66) * mm, "mid": v(-2.92, 9.56) * mm, "end": v(-0.7, 9.98) * mm});
            skArc(sketch, "E137.2.24", {"start": v(-6.9, 11.95) * mm, "mid": v(-8.4, 10.95) * mm, "end": v(-9.76, 9.76) * mm});
            skArc(sketch, "E137.2.25", {"start": v(-13.5, 23.38) * mm, "mid": v(-11.2, 24.57) * mm, "end": v(-8.8, 25.53) * mm});
            skArc(sketch, "E137.2.26", {"start": v(-16.9, 29.27) * mm, "mid": v(-20.58, 26.82) * mm, "end": v(-23.9, 23.9) * mm});
            skArc(sketch, "E137.2.27", {"start": v(-35.8, 62) * mm, "mid": v(-20.93, 68.47) * mm, "end": v(-5, 71.43) * mm});
            skArc(sketch, "E137.2.28", {"start": v(-23.9, 41.4) * mm, "mid": v(-19.82, 43.5) * mm, "end": v(-15.56, 45.2) * mm});
            skArc(sketch, "E137.2.29", {"start": v(-6.7, 11.6) * mm, "mid": v(-8.16, 10.63) * mm, "end": v(-9.48, 9.48) * mm});
            skArc(sketch, "E137.2.30", {"start": v(-27.1, 46.94) * mm, "mid": v(-22.48, 49.32) * mm, "end": v(-17.65, 51.25) * mm});
            skArc(sketch, "E137.2.31", {"start": v(-40.9, 70.84) * mm, "mid": v(-33.92, 74.43) * mm, "end": v(-26.63, 77.34) * mm});
            skArc(sketch, "E137.2.32", {"start": v(-37.5, 64.95) * mm, "mid": v(-31.1, 68.25) * mm, "end": v(-24.42, 70.91) * mm});
            skArc(sketch, "E137.2.33", {"start": v(-17.1, 29.62) * mm, "mid": v(-14.18, 31.12) * mm, "end": v(-11.13, 32.34) * mm});
            skArc(sketch, "E137.2.34", {"start": v(-16.9, 29.27) * mm, "mid": v(-14.02, 30.76) * mm, "end": v(-11, 31.96) * mm});
            skArc(sketch, "E137.2.35", {"start": v(-20.3, 35.16) * mm, "mid": v(-24.72, 32.21) * mm, "end": v(-28.7, 28.7) * mm});
            skArc(sketch, "E137.2.36", {"start": v(-42.4, 73.44) * mm, "mid": v(-24.8, 81.1) * mm, "end": v(-5.92, 84.6) * mm});
            skArc(sketch, "E137.2.37", {"start": v(-11.8, 20.44) * mm, "mid": v(-6.9, 22.57) * mm, "end": v(-1.65, 23.54) * mm});
            skArc(sketch, "E137.2.38", {"start": v(-3.5, 6.06) * mm, "mid": v(-4.26, 5.55) * mm, "end": v(-4.95, 4.95) * mm});
            skArc(sketch, "E137.2.39", {"start": v(-40.9, 70.84) * mm, "mid": v(-49.8, 64.9) * mm, "end": v(-57.84, 57.84) * mm});
            skArc(sketch, "E137.2.40", {"start": v(-25.6, 44.34) * mm, "mid": v(-14.97, 48.96) * mm, "end": v(-3.57, 51.08) * mm});
            skArc(sketch, "E137.2.41", {"start": v(-22.2, 38.45) * mm, "mid": v(-12.98, 42.46) * mm, "end": v(-3.1, 44.3) * mm});
            skArc(sketch, "E137.2.42", {"start": v(-30.7, 53.17) * mm, "mid": v(-25.46, 55.87) * mm, "end": v(-19.99, 58.05) * mm});
            skArc(sketch, "E137.2.43", {"start": v(-23.9, 41.4) * mm, "mid": v(-29.1, 37.92) * mm, "end": v(-33.8, 33.8) * mm});
            skArc(sketch, "E137.2.44", {"start": v(-13.5, 23.38) * mm, "mid": v(-16.44, 21.42) * mm, "end": v(-19.1, 19.1) * mm});
            skArc(sketch, "E137.2.45", {"start": v(-6.7, 11.6) * mm, "mid": v(-5.56, 12.2) * mm, "end": v(-4.36, 12.67) * mm});
            skArc(sketch, "E137.2.46", {"start": v(-18.6, 32.22) * mm, "mid": v(-10.88, 35.57) * mm, "end": v(-2.6, 37.1) * mm});
            skArc(sketch, "E137.2.47", {"start": v(-34.1, 59.06) * mm, "mid": v(-28.28, 62.06) * mm, "end": v(-22.2, 64.48) * mm});
            skArc(sketch, "E137.2.48", {"start": v(-30.5, 52.83) * mm, "mid": v(-25.3, 55.5) * mm, "end": v(-19.86, 57.68) * mm});
            skArc(sketch, "E137.2.49", {"start": v(-44.3, 76.73) * mm, "mid": v(-36.74, 80.62) * mm, "end": v(-28.85, 83.77) * mm});
            skArc(sketch, "E137.2.50", {"start": v(-33.9, 58.72) * mm, "mid": v(-28.12, 61.7) * mm, "end": v(-22.07, 64.1) * mm});
            skArc(sketch, "E137.2.51", {"start": v(-39, 67.55) * mm, "mid": v(-22.8, 74.6) * mm, "end": v(-5.44, 77.8) * mm});
            skArc(sketch, "E137.2.52", {"start": v(-8.4, 14.55) * mm, "mid": v(-4.91, 16.07) * mm, "end": v(-1.17, 16.76) * mm});
            skArc(sketch, "E137.2.53", {"start": v(-25.4, 44) * mm, "mid": v(-14.85, 48.58) * mm, "end": v(-3.54, 50.68) * mm});
            skArc(sketch, "E137.2.54", {"start": v(-23.7, 41.05) * mm, "mid": v(-19.66, 43.13) * mm, "end": v(-15.43, 44.82) * mm});
            skArc(sketch, "E137.2.55", {"start": v(-22, 38.1) * mm, "mid": v(-12.86, 42.08) * mm, "end": v(-3.07, 43.9) * mm});
            skArc(sketch, "E137.2.56", {"start": v(-34.1, 59.06) * mm, "mid": v(-41.52, 54.1) * mm, "end": v(-48.22, 48.22) * mm});
            skArc(sketch, "E137.2.57", {"start": v(-44.1, 76.38) * mm, "mid": v(-36.58, 80.26) * mm, "end": v(-28.72, 83.4) * mm});
            skArc(sketch, "E137.2.58", {"start": v(-37.3, 64.6) * mm, "mid": v(-30.94, 67.88) * mm, "end": v(-24.29, 70.54) * mm});
            skLineSegment(sketch, "E137.2.59", {"start": v(-6.42, 91.78) * mm, "end": v(-6.39, 91.38) * mm});
            skArc(sketch, "E137.2.60", {"start": v(-37.5, 64.95) * mm, "mid": v(-45.66, 59.5) * mm, "end": v(-53.03, 53.03) * mm});
            skArc(sketch, "E137.2.61", {"start": v(-37.3, 64.6) * mm, "mid": v(-45.41, 59.18) * mm, "end": v(-52.75, 52.75) * mm});
            skArc(sketch, "E137.2.62", {"start": v(-44.1, 76.38) * mm, "mid": v(-53.7, 69.97) * mm, "end": v(-62.37, 62.37) * mm});
            skArc(sketch, "E137.2.63", {"start": v(-3.5, 6.06) * mm, "mid": v(-2.9, 6.37) * mm, "end": v(-2.28, 6.62) * mm});
            skArc(sketch, "E137.2.64", {"start": v(-20.5, 35.5) * mm, "mid": v(-17, 37.3) * mm, "end": v(-13.35, 38.77) * mm});
            skArc(sketch, "E137.2.65", {"start": v(-33.9, 58.72) * mm, "mid": v(-41.27, 53.79) * mm, "end": v(-47.94, 47.94) * mm});
            skArc(sketch, "E137.2.66", {"start": v(-27.3, 47.28) * mm, "mid": v(-22.64, 49.68) * mm, "end": v(-17.78, 51.63) * mm});
            skArc(sketch, "E137.2.67", {"start": v(-10.3, 17.84) * mm, "mid": v(-8.54, 18.75) * mm, "end": v(-6.7, 19.48) * mm});
            skArc(sketch, "E137.2.68", {"start": v(-6.9, 11.95) * mm, "mid": v(-5.72, 12.56) * mm, "end": v(-4.5, 13.05) * mm});
            skArc(sketch, "E137.2.69", {"start": v(-12, 20.78) * mm, "mid": v(-7.02, 22.95) * mm, "end": v(-1.67, 23.94) * mm});
            skArc(sketch, "E137.2.70", {"start": v(-15.2, 26.33) * mm, "mid": v(-8.89, 29.07) * mm, "end": v(-2.12, 30.33) * mm});
            skArc(sketch, "E137.2.71", {"start": v(-30.7, 53.17) * mm, "mid": v(-37.38, 48.71) * mm, "end": v(-43.42, 43.42) * mm});
            skArc(sketch, "E137.2.72", {"start": v(-4.67, 4.67) * mm, "mid": v(-3.5, 5.6) * mm, "end": v(-2.15, 6.24) * mm});
            skArc(sketch, "E137.2.73", {"start": v(-30.5, 52.83) * mm, "mid": v(-37.13, 48.4) * mm, "end": v(-43.13, 43.13) * mm});
            skArc(sketch, "E137.2.74", {"start": v(-23.7, 41.05) * mm, "mid": v(-28.86, 37.6) * mm, "end": v(-33.52, 33.52) * mm});
            skArc(sketch, "E137.2.75", {"start": v(-17.1, 29.62) * mm, "mid": v(-20.82, 27.13) * mm, "end": v(-24.18, 24.18) * mm});
            skArc(sketch, "E137.2.76", {"start": v(-20.3, 35.16) * mm, "mid": v(-16.84, 36.94) * mm, "end": v(-13.22, 38.39) * mm});
            skArc(sketch, "E137.2.77", {"start": v(-35.6, 61.66) * mm, "mid": v(-20.82, 68.09) * mm, "end": v(-4.97, 71.03) * mm});
            skArc(sketch, "E137.3.0", {"start": v(0, 20.6) * mm, "mid": v(-2.69, 20.42) * mm, "end": v(-5.33, 19.9) * mm});
            skArc(sketch, "E137.3.1", {"start": v(0, 17.2) * mm, "mid": v(3.87, 16.76) * mm, "end": v(7.54, 15.46) * mm});
            skArc(sketch, "E137.3.2", {"start": v(0, 20.2) * mm, "mid": v(-2.64, 20.03) * mm, "end": v(-5.23, 19.51) * mm});
            skArc(sketch, "E137.3.3", {"start": v(0, 64.4) * mm, "mid": v(14.49, 62.75) * mm, "end": v(28.23, 57.88) * mm});
            skArc(sketch, "E137.3.4", {"start": v(0, 81.4) * mm, "mid": v(-10.62, 80.7) * mm, "end": v(-21.07, 78.63) * mm});
            skArc(sketch, "E137.3.5", {"start": v(0, 20.2) * mm, "mid": v(1.94, 20.1) * mm, "end": v(3.85, 19.83) * mm});
            skArc(sketch, "E137.3.6", {"start": v(0, 78.4) * mm, "mid": v(17.64, 76.4) * mm, "end": v(34.37, 70.47) * mm});
            skArc(sketch, "E137.3.7", {"start": v(0, 10.4) * mm, "mid": v(2.34, 10.13) * mm, "end": v(4.56, 9.35) * mm});
            skArc(sketch, "E137.3.8", {"start": v(0, 37.6) * mm, "mid": v(8.46, 36.64) * mm, "end": v(16.48, 33.8) * mm});
            skArc(sketch, "E137.3.9", {"start": v(0, 92) * mm, "mid": v(20.7, 89.64) * mm, "end": v(40.33, 82.69) * mm});
            skArc(sketch, "E137.3.10", {"start": v(0, 27.4) * mm, "mid": v(2.63, 27.27) * mm, "end": v(5.23, 26.9) * mm});
            skArc(sketch, "E137.3.11", {"start": v(0, 27.4) * mm, "mid": v(-3.58, 27.17) * mm, "end": v(-7.1, 26.47) * mm});
            skArc(sketch, "E137.3.12", {"start": v(0, 88.6) * mm, "mid": v(-11.56, 87.84) * mm, "end": v(-22.93, 85.58) * mm});
            skArc(sketch, "E137.3.13", {"start": v(0, 85.2) * mm, "mid": v(19.17, 83.02) * mm, "end": v(37.35, 76.58) * mm});
            skArc(sketch, "E137.3.14", {"start": v(0, 54.6) * mm, "mid": v(-7.13, 54.13) * mm, "end": v(-14.13, 52.74) * mm});
            skArc(sketch, "E137.3.15", {"start": v(0, 54.2) * mm, "mid": v(-7.07, 53.74) * mm, "end": v(-14.03, 52.35) * mm});
            skArc(sketch, "E137.3.16", {"start": v(0, 91.6) * mm, "mid": v(20.6, 89.25) * mm, "end": v(40.15, 82.33) * mm});
            skArc(sketch, "E137.3.17", {"start": v(0, 81.4) * mm, "mid": v(7.8, 81.03) * mm, "end": v(15.53, 79.9) * mm});
            skArc(sketch, "E137.3.18", {"start": v(0, 30.8) * mm, "mid": v(6.93, 30.01) * mm, "end": v(13.5, 27.68) * mm});
            skArc(sketch, "E137.3.19", {"start": v(0, 58) * mm, "mid": v(13.05, 56.51) * mm, "end": v(25.43, 52.13) * mm});
            skArc(sketch, "E137.3.20", {"start": v(0, 57.6) * mm, "mid": v(12.96, 56.12) * mm, "end": v(25.25, 51.77) * mm});
            skArc(sketch, "E137.3.21", {"start": v(0, 64.8) * mm, "mid": v(14.58, 63.14) * mm, "end": v(28.4, 58.24) * mm});
            skArc(sketch, "E137.3.22", {"start": v(0, 41) * mm, "mid": v(-5.35, 40.65) * mm, "end": v(-10.61, 39.6) * mm});
            skArc(sketch, "E137.3.23", {"start": v(0, 10) * mm, "mid": v(2.25, 9.74) * mm, "end": v(4.38, 8.99) * mm});
            skArc(sketch, "E137.3.24", {"start": v(0, 13.8) * mm, "mid": v(-1.8, 13.68) * mm, "end": v(-3.57, 13.33) * mm});
            skArc(sketch, "E137.3.25", {"start": v(0, 27) * mm, "mid": v(2.59, 26.88) * mm, "end": v(5.15, 26.5) * mm});
            skArc(sketch, "E137.3.26", {"start": v(0, 33.8) * mm, "mid": v(-4.41, 33.51) * mm, "end": v(-8.75, 32.65) * mm});
            skArc(sketch, "E137.3.27", {"start": v(0, 71.6) * mm, "mid": v(16.1, 69.76) * mm, "end": v(31.39, 64.35) * mm});
            skArc(sketch, "E137.3.28", {"start": v(0, 47.8) * mm, "mid": v(4.58, 47.58) * mm, "end": v(9.12, 46.92) * mm});
            skArc(sketch, "E137.3.29", {"start": v(0, 13.4) * mm, "mid": v(-1.75, 13.29) * mm, "end": v(-3.47, 12.94) * mm});
            skArc(sketch, "E137.3.30", {"start": v(0, 54.2) * mm, "mid": v(5.2, 53.95) * mm, "end": v(10.34, 53.2) * mm});
            skArc(sketch, "E137.3.31", {"start": v(0, 81.8) * mm, "mid": v(7.84, 81.42) * mm, "end": v(15.6, 80.3) * mm});
            skArc(sketch, "E137.3.32", {"start": v(0, 75) * mm, "mid": v(7.19, 74.65) * mm, "end": v(14.31, 73.62) * mm});
            skArc(sketch, "E137.3.33", {"start": v(0, 34.2) * mm, "mid": v(3.28, 34.04) * mm, "end": v(6.53, 33.57) * mm});
            skArc(sketch, "E137.3.34", {"start": v(0, 33.8) * mm, "mid": v(3.24, 33.64) * mm, "end": v(6.45, 33.18) * mm});
            skArc(sketch, "E137.3.35", {"start": v(0, 40.6) * mm, "mid": v(-5.3, 40.25) * mm, "end": v(-10.5, 39.22) * mm});
            skArc(sketch, "E137.3.36", {"start": v(0, 84.8) * mm, "mid": v(19.08, 82.63) * mm, "end": v(37.17, 76.22) * mm});
            skArc(sketch, "E137.3.37", {"start": v(0, 23.6) * mm, "mid": v(5.3, 23) * mm, "end": v(10.35, 21.21) * mm});
            skArc(sketch, "E137.3.38", {"start": v(0, 7) * mm, "mid": v(-0.91, 6.94) * mm, "end": v(-1.81, 6.76) * mm});
            skArc(sketch, "E137.3.39", {"start": v(0, 81.8) * mm, "mid": v(-10.68, 81.1) * mm, "end": v(-21.17, 79.01) * mm});
            skArc(sketch, "E137.3.40", {"start": v(0, 51.2) * mm, "mid": v(11.52, 49.89) * mm, "end": v(22.44, 46.02) * mm});
            skArc(sketch, "E137.3.41", {"start": v(0, 44.4) * mm, "mid": v(9.99, 43.26) * mm, "end": v(19.46, 39.9) * mm});
            skArc(sketch, "E137.3.42", {"start": v(0, 61.4) * mm, "mid": v(5.88, 61.12) * mm, "end": v(11.72, 60.27) * mm});
            skArc(sketch, "E137.3.43", {"start": v(0, 47.8) * mm, "mid": v(-6.24, 47.4) * mm, "end": v(-12.37, 46.17) * mm});
            skArc(sketch, "E137.3.44", {"start": v(0, 27) * mm, "mid": v(-3.52, 26.77) * mm, "end": v(-6.99, 26.08) * mm});
            skArc(sketch, "E137.3.45", {"start": v(0, 13.4) * mm, "mid": v(1.28, 13.34) * mm, "end": v(2.56, 13.15) * mm});
            skArc(sketch, "E137.3.46", {"start": v(0, 37.2) * mm, "mid": v(8.37, 36.25) * mm, "end": v(16.3, 33.44) * mm});
            skArc(sketch, "E137.3.47", {"start": v(0, 68.2) * mm, "mid": v(6.54, 67.89) * mm, "end": v(13.01, 66.95) * mm});
            skArc(sketch, "E137.3.48", {"start": v(0, 61) * mm, "mid": v(5.85, 60.72) * mm, "end": v(11.64, 59.88) * mm});
            skArc(sketch, "E137.3.49", {"start": v(0, 88.6) * mm, "mid": v(8.5, 88.2) * mm, "end": v(16.9, 86.97) * mm});
            skArc(sketch, "E137.3.50", {"start": v(0, 67.8) * mm, "mid": v(6.5, 67.49) * mm, "end": v(12.94, 66.55) * mm});
            skArc(sketch, "E137.3.51", {"start": v(0, 78) * mm, "mid": v(17.55, 76) * mm, "end": v(34.2, 70.1) * mm});
            skArc(sketch, "E137.3.52", {"start": v(0, 16.8) * mm, "mid": v(3.78, 16.37) * mm, "end": v(7.36, 15.1) * mm});
            skArc(sketch, "E137.3.53", {"start": v(0, 50.8) * mm, "mid": v(11.43, 49.5) * mm, "end": v(22.27, 45.66) * mm});
            skArc(sketch, "E137.3.54", {"start": v(0, 47.4) * mm, "mid": v(4.54, 47.18) * mm, "end": v(9.04, 46.53) * mm});
            skArc(sketch, "E137.3.55", {"start": v(0, 44) * mm, "mid": v(9.9, 42.87) * mm, "end": v(19.29, 39.55) * mm});
            skArc(sketch, "E137.3.56", {"start": v(0, 68.2) * mm, "mid": v(-8.9, 67.62) * mm, "end": v(-17.65, 65.88) * mm});
            skArc(sketch, "E137.3.57", {"start": v(0, 88.2) * mm, "mid": v(8.45, 87.8) * mm, "end": v(16.83, 86.58) * mm});
            skArc(sketch, "E137.3.58", {"start": v(0, 74.6) * mm, "mid": v(7.15, 74.26) * mm, "end": v(14.23, 73.23) * mm});
            skLineSegment(sketch, "E137.3.59", {"start": v(40.33, 82.69) * mm, "end": v(40.15, 82.33) * mm});
            skArc(sketch, "E137.3.60", {"start": v(0, 75) * mm, "mid": v(-9.79, 74.36) * mm, "end": v(-19.41, 72.44) * mm});
            skArc(sketch, "E137.3.61", {"start": v(0, 74.6) * mm, "mid": v(-9.74, 73.96) * mm, "end": v(-19.3, 72.06) * mm});
            skArc(sketch, "E137.3.62", {"start": v(0, 88.2) * mm, "mid": v(-11.51, 87.45) * mm, "end": v(-22.83, 85.2) * mm});
            skArc(sketch, "E137.3.63", {"start": v(0, 7) * mm, "mid": v(0.67, 6.97) * mm, "end": v(1.34, 6.87) * mm});
            skArc(sketch, "E137.3.64", {"start": v(0, 41) * mm, "mid": v(3.93, 40.81) * mm, "end": v(7.82, 40.25) * mm});
            skArc(sketch, "E137.3.65", {"start": v(0, 67.8) * mm, "mid": v(-8.85, 67.22) * mm, "end": v(-17.55, 65.49) * mm});
            skArc(sketch, "E137.3.66", {"start": v(0, 54.6) * mm, "mid": v(5.23, 54.35) * mm, "end": v(10.42, 53.6) * mm});
            skArc(sketch, "E137.3.67", {"start": v(0, 20.6) * mm, "mid": v(1.97, 20.5) * mm, "end": v(3.93, 20.22) * mm});
            skArc(sketch, "E137.3.68", {"start": v(0, 13.8) * mm, "mid": v(1.32, 13.74) * mm, "end": v(2.63, 13.55) * mm});
            skArc(sketch, "E137.3.69", {"start": v(0, 24) * mm, "mid": v(5.4, 23.38) * mm, "end": v(10.52, 21.57) * mm});
            skArc(sketch, "E137.3.70", {"start": v(0, 30.4) * mm, "mid": v(6.84, 29.62) * mm, "end": v(13.33, 27.32) * mm});
            skArc(sketch, "E137.3.71", {"start": v(0, 61.4) * mm, "mid": v(-8.01, 60.87) * mm, "end": v(-15.9, 59.3) * mm});
            skArc(sketch, "E137.3.72", {"start": v(-1.7, 6.38) * mm, "mid": v(-0.23, 6.6) * mm, "end": v(1.26, 6.48) * mm});
            skArc(sketch, "E137.3.73", {"start": v(0, 61) * mm, "mid": v(-7.96, 60.48) * mm, "end": v(-15.79, 58.92) * mm});
            skArc(sketch, "E137.3.74", {"start": v(0, 47.4) * mm, "mid": v(-6.19, 47) * mm, "end": v(-12.27, 45.78) * mm});
            skArc(sketch, "E137.3.75", {"start": v(0, 34.2) * mm, "mid": v(-4.46, 33.9) * mm, "end": v(-8.85, 33.03) * mm});
            skArc(sketch, "E137.3.76", {"start": v(0, 40.6) * mm, "mid": v(3.9, 40.41) * mm, "end": v(7.75, 39.85) * mm});
            skArc(sketch, "E137.3.77", {"start": v(0, 71.2) * mm, "mid": v(16.02, 69.38) * mm, "end": v(31.21, 64) * mm});
            skArc(sketch, "E137.4.0", {"start": v(10.3, 17.84) * mm, "mid": v(7.88, 19.03) * mm, "end": v(5.33, 19.9) * mm});
            skArc(sketch, "E137.4.1", {"start": v(8.6, 14.9) * mm, "mid": v(11.73, 12.58) * mm, "end": v(14.26, 9.62) * mm});
            skArc(sketch, "E137.4.2", {"start": v(10.1, 17.5) * mm, "mid": v(7.73, 18.66) * mm, "end": v(5.23, 19.51) * mm});
            skArc(sketch, "E137.4.3", {"start": v(32.2, 55.77) * mm, "mid": v(43.92, 47.1) * mm, "end": v(53.4, 36.01) * mm});
            skArc(sketch, "E137.4.4", {"start": v(40.7, 70.5) * mm, "mid": v(31.15, 75.2) * mm, "end": v(21.07, 78.63) * mm});
            skArc(sketch, "E137.4.5", {"start": v(10.1, 17.5) * mm, "mid": v(11.73, 16.45) * mm, "end": v(13.25, 15.25) * mm});
            skArc(sketch, "E137.4.6", {"start": v(39.2, 67.9) * mm, "mid": v(53.47, 57.34) * mm, "end": v(65, 43.84) * mm});
            skArc(sketch, "E137.4.7", {"start": v(5.2, 9) * mm, "mid": v(7.1, 7.6) * mm, "end": v(8.62, 5.82) * mm});
            skArc(sketch, "E137.4.8", {"start": v(18.8, 32.56) * mm, "mid": v(25.64, 27.5) * mm, "end": v(31.17, 21.03) * mm});
            skArc(sketch, "E137.4.9", {"start": v(46, 79.67) * mm, "mid": v(62.74, 67.28) * mm, "end": v(76.27, 51.45) * mm});
            skArc(sketch, "E137.4.10", {"start": v(13.7, 23.73) * mm, "mid": v(15.91, 22.3) * mm, "end": v(17.98, 20.68) * mm});
            skArc(sketch, "E137.4.11", {"start": v(13.7, 23.73) * mm, "mid": v(10.49, 25.31) * mm, "end": v(7.1, 26.47) * mm});
            skArc(sketch, "E137.4.12", {"start": v(44.3, 76.73) * mm, "mid": v(33.9, 81.86) * mm, "end": v(22.93, 85.58) * mm});
            skArc(sketch, "E137.4.13", {"start": v(42.6, 73.79) * mm, "mid": v(58.1, 62.31) * mm, "end": v(70.63, 47.64) * mm});
            skArc(sketch, "E137.4.14", {"start": v(27.3, 47.28) * mm, "mid": v(20.9, 50.44) * mm, "end": v(14.13, 52.74) * mm});
            skArc(sketch, "E137.4.15", {"start": v(27.1, 46.94) * mm, "mid": v(20.74, 50.07) * mm, "end": v(14.03, 52.35) * mm});
            skArc(sketch, "E137.4.16", {"start": v(45.8, 79.33) * mm, "mid": v(62.47, 67) * mm, "end": v(75.94, 51.22) * mm});
            skArc(sketch, "E137.4.17", {"start": v(40.7, 70.5) * mm, "mid": v(47.27, 66.27) * mm, "end": v(53.4, 61.43) * mm});
            skArc(sketch, "E137.4.18", {"start": v(15.4, 26.67) * mm, "mid": v(21, 22.53) * mm, "end": v(25.53, 17.22) * mm});
            skArc(sketch, "E137.4.19", {"start": v(29, 50.23) * mm, "mid": v(39.56, 42.42) * mm, "end": v(48.08, 32.43) * mm});
            skArc(sketch, "E137.4.20", {"start": v(28.8, 49.88) * mm, "mid": v(39.28, 42.13) * mm, "end": v(47.75, 32.2) * mm});
            skArc(sketch, "E137.4.21", {"start": v(32.4, 56.12) * mm, "mid": v(44.2, 47.4) * mm, "end": v(53.72, 36.24) * mm});
            skArc(sketch, "E137.4.22", {"start": v(20.5, 35.5) * mm, "mid": v(15.7, 37.88) * mm, "end": v(10.61, 39.6) * mm});
            skArc(sketch, "E137.4.23", {"start": v(5, 8.66) * mm, "mid": v(6.82, 7.31) * mm, "end": v(8.3, 5.6) * mm});
            skArc(sketch, "E137.4.24", {"start": v(6.9, 11.95) * mm, "mid": v(5.28, 12.75) * mm, "end": v(3.57, 13.33) * mm});
            skArc(sketch, "E137.4.25", {"start": v(13.5, 23.38) * mm, "mid": v(15.68, 21.98) * mm, "end": v(17.71, 20.38) * mm});
            skArc(sketch, "E137.4.26", {"start": v(16.9, 29.27) * mm, "mid": v(12.93, 31.23) * mm, "end": v(8.75, 32.65) * mm});
            skArc(sketch, "E137.4.27", {"start": v(35.8, 62) * mm, "mid": v(48.83, 52.36) * mm, "end": v(59.36, 40.04) * mm});
            skArc(sketch, "E137.4.28", {"start": v(23.9, 41.4) * mm, "mid": v(27.76, 38.91) * mm, "end": v(31.36, 36.08) * mm});
            skArc(sketch, "E137.4.29", {"start": v(6.7, 11.6) * mm, "mid": v(5.13, 12.38) * mm, "end": v(3.47, 12.94) * mm});
            skArc(sketch, "E137.4.30", {"start": v(27.1, 46.94) * mm, "mid": v(31.47, 44.13) * mm, "end": v(35.56, 40.9) * mm});
            skArc(sketch, "E137.4.31", {"start": v(40.9, 70.84) * mm, "mid": v(47.5, 66.6) * mm, "end": v(53.67, 61.74) * mm});
            skArc(sketch, "E137.4.32", {"start": v(37.5, 64.95) * mm, "mid": v(43.55, 61.06) * mm, "end": v(49.2, 56.6) * mm});
            skArc(sketch, "E137.4.33", {"start": v(17.1, 29.62) * mm, "mid": v(19.86, 27.84) * mm, "end": v(22.44, 25.81) * mm});
            skArc(sketch, "E137.4.34", {"start": v(16.9, 29.27) * mm, "mid": v(19.63, 27.52) * mm, "end": v(22.17, 25.5) * mm});
            skArc(sketch, "E137.4.35", {"start": v(20.3, 35.16) * mm, "mid": v(15.54, 37.5) * mm, "end": v(10.5, 39.22) * mm});
            skArc(sketch, "E137.4.36", {"start": v(42.4, 73.44) * mm, "mid": v(57.83, 62.02) * mm, "end": v(70.3, 47.42) * mm});
            skArc(sketch, "E137.4.37", {"start": v(11.8, 20.44) * mm, "mid": v(16.1, 17.26) * mm, "end": v(19.57, 13.2) * mm});
            skArc(sketch, "E137.4.38", {"start": v(3.5, 6.06) * mm, "mid": v(2.68, 6.47) * mm, "end": v(1.81, 6.76) * mm});
            skArc(sketch, "E137.4.39", {"start": v(40.9, 70.84) * mm, "mid": v(31.3, 75.57) * mm, "end": v(21.17, 79.01) * mm});
            skArc(sketch, "E137.4.40", {"start": v(25.6, 44.34) * mm, "mid": v(34.92, 37.45) * mm, "end": v(42.45, 28.63) * mm});
            skArc(sketch, "E137.4.41", {"start": v(22.2, 38.45) * mm, "mid": v(30.28, 32.47) * mm, "end": v(36.8, 24.83) * mm});
            skArc(sketch, "E137.4.42", {"start": v(30.7, 53.17) * mm, "mid": v(35.66, 49.99) * mm, "end": v(40.28, 46.34) * mm});
            skArc(sketch, "E137.4.43", {"start": v(23.9, 41.4) * mm, "mid": v(18.3, 44.16) * mm, "end": v(12.37, 46.17) * mm});
            skArc(sketch, "E137.4.44", {"start": v(13.5, 23.38) * mm, "mid": v(10.33, 24.94) * mm, "end": v(6.99, 26.08) * mm});
            skArc(sketch, "E137.4.45", {"start": v(6.7, 11.6) * mm, "mid": v(7.78, 10.9) * mm, "end": v(8.8, 10.11) * mm});
            skArc(sketch, "E137.4.46", {"start": v(18.6, 32.22) * mm, "mid": v(25.37, 27.2) * mm, "end": v(30.84, 20.8) * mm});
            skArc(sketch, "E137.4.47", {"start": v(34.1, 59.06) * mm, "mid": v(39.6, 55.52) * mm, "end": v(44.74, 51.47) * mm});
            skArc(sketch, "E137.4.48", {"start": v(30.5, 52.83) * mm, "mid": v(35.42, 49.66) * mm, "end": v(40.02, 46.04) * mm});
            skArc(sketch, "E137.4.49", {"start": v(44.3, 76.73) * mm, "mid": v(51.45, 72.13) * mm, "end": v(58.13, 66.87) * mm});
            skArc(sketch, "E137.4.50", {"start": v(33.9, 58.72) * mm, "mid": v(39.37, 55.2) * mm, "end": v(44.48, 51.17) * mm});
            skArc(sketch, "E137.4.51", {"start": v(39, 67.55) * mm, "mid": v(53.2, 57.05) * mm, "end": v(64.66, 43.62) * mm});
            skArc(sketch, "E137.4.52", {"start": v(8.4, 14.55) * mm, "mid": v(11.46, 12.29) * mm, "end": v(13.93, 9.4) * mm});
            skArc(sketch, "E137.4.53", {"start": v(25.4, 44) * mm, "mid": v(34.65, 37.15) * mm, "end": v(42.12, 28.4) * mm});
            skArc(sketch, "E137.4.54", {"start": v(23.7, 41.05) * mm, "mid": v(27.53, 38.59) * mm, "end": v(31.1, 35.77) * mm});
            skArc(sketch, "E137.4.55", {"start": v(22, 38.1) * mm, "mid": v(30, 32.18) * mm, "end": v(36.48, 24.6) * mm});
            skArc(sketch, "E137.4.56", {"start": v(34.1, 59.06) * mm, "mid": v(26.1, 63) * mm, "end": v(17.65, 65.88) * mm});
            skArc(sketch, "E137.4.57", {"start": v(44.1, 76.38) * mm, "mid": v(51.22, 71.8) * mm, "end": v(57.86, 66.57) * mm});
            skArc(sketch, "E137.4.58", {"start": v(37.3, 64.6) * mm, "mid": v(43.32, 60.73) * mm, "end": v(48.94, 56.3) * mm});
            skLineSegment(sketch, "E137.4.59", {"start": v(76.27, 51.45) * mm, "end": v(75.94, 51.22) * mm});
            skArc(sketch, "E137.4.60", {"start": v(37.5, 64.95) * mm, "mid": v(28.7, 69.3) * mm, "end": v(19.41, 72.44) * mm});
            skArc(sketch, "E137.4.61", {"start": v(37.3, 64.6) * mm, "mid": v(28.55, 68.92) * mm, "end": v(19.3, 72.06) * mm});
            skArc(sketch, "E137.4.62", {"start": v(44.1, 76.38) * mm, "mid": v(33.75, 81.49) * mm, "end": v(22.83, 85.2) * mm});
            skArc(sketch, "E137.4.63", {"start": v(3.5, 6.06) * mm, "mid": v(4.06, 5.7) * mm, "end": v(4.6, 5.28) * mm});
            skArc(sketch, "E137.4.64", {"start": v(20.5, 35.5) * mm, "mid": v(23.8, 33.38) * mm, "end": v(26.9, 30.94) * mm});
            skArc(sketch, "E137.4.65", {"start": v(33.9, 58.72) * mm, "mid": v(25.95, 62.64) * mm, "end": v(17.55, 65.49) * mm});
            skArc(sketch, "E137.4.66", {"start": v(27.3, 47.28) * mm, "mid": v(31.7, 44.45) * mm, "end": v(35.82, 41.2) * mm});
            skArc(sketch, "E137.4.67", {"start": v(10.3, 17.84) * mm, "mid": v(11.96, 16.77) * mm, "end": v(13.51, 15.55) * mm});
            skArc(sketch, "E137.4.68", {"start": v(6.9, 11.95) * mm, "mid": v(8.01, 11.23) * mm, "end": v(9.05, 10.41) * mm});
            skArc(sketch, "E137.4.69", {"start": v(12, 20.78) * mm, "mid": v(16.37, 17.55) * mm, "end": v(19.9, 13.42) * mm});
            skArc(sketch, "E137.4.70", {"start": v(15.2, 26.33) * mm, "mid": v(20.73, 22.23) * mm, "end": v(25.2, 17) * mm});
            skArc(sketch, "E137.4.71", {"start": v(30.7, 53.17) * mm, "mid": v(23.5, 56.73) * mm, "end": v(15.9, 59.3) * mm});
            skArc(sketch, "E137.4.72", {"start": v(1.7, 6.38) * mm, "mid": v(3.1, 5.83) * mm, "end": v(4.33, 4.98) * mm});
            skArc(sketch, "E137.4.73", {"start": v(30.5, 52.83) * mm, "mid": v(23.34, 56.36) * mm, "end": v(15.79, 58.92) * mm});
            skArc(sketch, "E137.4.74", {"start": v(23.7, 41.05) * mm, "mid": v(18.14, 43.8) * mm, "end": v(12.27, 45.78) * mm});
            skArc(sketch, "E137.4.75", {"start": v(17.1, 29.62) * mm, "mid": v(13.09, 31.6) * mm, "end": v(8.85, 33.03) * mm});
            skArc(sketch, "E137.4.76", {"start": v(20.3, 35.16) * mm, "mid": v(23.58, 33.05) * mm, "end": v(26.64, 30.64) * mm});
            skArc(sketch, "E137.4.77", {"start": v(35.6, 61.66) * mm, "mid": v(48.56, 52.07) * mm, "end": v(59.03, 39.81) * mm});
            skArc(sketch, "E137.5.0", {"start": v(17.84, 10.3) * mm, "mid": v(16.34, 12.54) * mm, "end": v(14.57, 14.57) * mm});
            skArc(sketch, "E137.5.1", {"start": v(14.9, 8.6) * mm, "mid": v(16.45, 5.03) * mm, "end": v(17.16, 1.2) * mm});
            skArc(sketch, "E137.5.2", {"start": v(17.5, 10.1) * mm, "mid": v(16.03, 12.3) * mm, "end": v(14.28, 14.28) * mm});
            skArc(sketch, "E137.5.3", {"start": v(55.77, 32.2) * mm, "mid": v(61.59, 18.83) * mm, "end": v(64.24, 4.5) * mm});
            skArc(sketch, "E137.5.4", {"start": v(70.5, 40.7) * mm, "mid": v(64.58, 49.55) * mm, "end": v(57.56, 57.56) * mm});
            skArc(sketch, "E137.5.5", {"start": v(17.5, 10.1) * mm, "mid": v(18.38, 8.38) * mm, "end": v(19.1, 6.58) * mm});
            skArc(sketch, "E137.5.6", {"start": v(67.9, 39.2) * mm, "mid": v(74.97, 22.92) * mm, "end": v(78.2, 5.47) * mm});
            skArc(sketch, "E137.5.7", {"start": v(9, 5.2) * mm, "mid": v(9.95, 3.04) * mm, "end": v(10.37, 0.73) * mm});
            skArc(sketch, "E137.5.8", {"start": v(32.56, 18.8) * mm, "mid": v(35.96, 11) * mm, "end": v(37.5, 2.62) * mm});
            skArc(sketch, "E137.5.9", {"start": v(79.67, 46) * mm, "mid": v(87.98, 26.9) * mm, "end": v(91.78, 6.42) * mm});
            skArc(sketch, "E137.5.10", {"start": v(23.73, 13.7) * mm, "mid": v(24.93, 11.36) * mm, "end": v(25.9, 8.92) * mm});
            skArc(sketch, "E137.5.11", {"start": v(23.73, 13.7) * mm, "mid": v(21.74, 16.68) * mm, "end": v(19.37, 19.37) * mm});
            skArc(sketch, "E137.5.12", {"start": v(76.73, 44.3) * mm, "mid": v(70.3, 53.94) * mm, "end": v(62.65, 62.65) * mm});
            skArc(sketch, "E137.5.13", {"start": v(73.79, 42.6) * mm, "mid": v(81.48, 24.91) * mm, "end": v(85, 5.94) * mm});
            skArc(sketch, "E137.5.14", {"start": v(47.28, 27.3) * mm, "mid": v(43.32, 33.24) * mm, "end": v(38.6, 38.6) * mm});
            skArc(sketch, "E137.5.15", {"start": v(46.94, 27.1) * mm, "mid": v(43, 33) * mm, "end": v(38.33, 38.33) * mm});
            skArc(sketch, "E137.5.16", {"start": v(79.33, 45.8) * mm, "mid": v(87.6, 26.78) * mm, "end": v(91.38, 6.39) * mm});
            skArc(sketch, "E137.5.17", {"start": v(70.5, 40.7) * mm, "mid": v(74.07, 33.76) * mm, "end": v(76.97, 26.5) * mm});
            skArc(sketch, "E137.5.18", {"start": v(26.67, 15.4) * mm, "mid": v(29.45, 9) * mm, "end": v(30.72, 2.15) * mm});
            skArc(sketch, "E137.5.19", {"start": v(50.23, 29) * mm, "mid": v(55.47, 16.96) * mm, "end": v(57.86, 4.05) * mm});
            skArc(sketch, "E137.5.20", {"start": v(49.88, 28.8) * mm, "mid": v(55.08, 16.84) * mm, "end": v(57.46, 4.02) * mm});
            skArc(sketch, "E137.5.21", {"start": v(56.12, 32.4) * mm, "mid": v(61.97, 18.95) * mm, "end": v(64.64, 4.52) * mm});
            skArc(sketch, "E137.5.22", {"start": v(35.5, 20.5) * mm, "mid": v(32.53, 24.96) * mm, "end": v(29, 29) * mm});
            skArc(sketch, "E137.5.23", {"start": v(8.66, 5) * mm, "mid": v(9.56, 2.92) * mm, "end": v(9.98, 0.7) * mm});
            skArc(sketch, "E137.5.24", {"start": v(11.95, 6.9) * mm, "mid": v(10.95, 8.4) * mm, "end": v(9.76, 9.76) * mm});
            skArc(sketch, "E137.5.25", {"start": v(23.38, 13.5) * mm, "mid": v(24.57, 11.2) * mm, "end": v(25.53, 8.8) * mm});
            skArc(sketch, "E137.5.26", {"start": v(29.27, 16.9) * mm, "mid": v(26.82, 20.58) * mm, "end": v(23.9, 23.9) * mm});
            skArc(sketch, "E137.5.27", {"start": v(62, 35.8) * mm, "mid": v(68.47, 20.93) * mm, "end": v(71.43, 5) * mm});
            skArc(sketch, "E137.5.28", {"start": v(41.4, 23.9) * mm, "mid": v(43.5, 19.82) * mm, "end": v(45.2, 15.56) * mm});
            skArc(sketch, "E137.5.29", {"start": v(11.6, 6.7) * mm, "mid": v(10.63, 8.16) * mm, "end": v(9.48, 9.48) * mm});
            skArc(sketch, "E137.5.30", {"start": v(46.94, 27.1) * mm, "mid": v(49.32, 22.48) * mm, "end": v(51.25, 17.65) * mm});
            skArc(sketch, "E137.5.31", {"start": v(70.84, 40.9) * mm, "mid": v(74.43, 33.92) * mm, "end": v(77.34, 26.63) * mm});
            skArc(sketch, "E137.5.32", {"start": v(64.95, 37.5) * mm, "mid": v(68.25, 31.1) * mm, "end": v(70.91, 24.42) * mm});
            skArc(sketch, "E137.5.33", {"start": v(29.62, 17.1) * mm, "mid": v(31.12, 14.18) * mm, "end": v(32.34, 11.13) * mm});
            skArc(sketch, "E137.5.34", {"start": v(29.27, 16.9) * mm, "mid": v(30.76, 14.02) * mm, "end": v(31.96, 11) * mm});
            skArc(sketch, "E137.5.35", {"start": v(35.16, 20.3) * mm, "mid": v(32.21, 24.72) * mm, "end": v(28.7, 28.7) * mm});
            skArc(sketch, "E137.5.36", {"start": v(73.44, 42.4) * mm, "mid": v(81.1, 24.8) * mm, "end": v(84.6, 5.92) * mm});
            skArc(sketch, "E137.5.37", {"start": v(20.44, 11.8) * mm, "mid": v(22.57, 6.9) * mm, "end": v(23.54, 1.65) * mm});
            skArc(sketch, "E137.5.38", {"start": v(6.06, 3.5) * mm, "mid": v(5.55, 4.26) * mm, "end": v(4.95, 4.95) * mm});
            skArc(sketch, "E137.5.39", {"start": v(70.84, 40.9) * mm, "mid": v(64.9, 49.8) * mm, "end": v(57.84, 57.84) * mm});
            skArc(sketch, "E137.5.40", {"start": v(44.34, 25.6) * mm, "mid": v(48.96, 14.97) * mm, "end": v(51.08, 3.57) * mm});
            skArc(sketch, "E137.5.41", {"start": v(38.45, 22.2) * mm, "mid": v(42.46, 12.98) * mm, "end": v(44.3, 3.1) * mm});
            skArc(sketch, "E137.5.42", {"start": v(53.17, 30.7) * mm, "mid": v(55.87, 25.46) * mm, "end": v(58.05, 19.99) * mm});
            skArc(sketch, "E137.5.43", {"start": v(41.4, 23.9) * mm, "mid": v(37.92, 29.1) * mm, "end": v(33.8, 33.8) * mm});
            skArc(sketch, "E137.5.44", {"start": v(23.38, 13.5) * mm, "mid": v(21.42, 16.44) * mm, "end": v(19.1, 19.1) * mm});
            skArc(sketch, "E137.5.45", {"start": v(11.6, 6.7) * mm, "mid": v(12.2, 5.56) * mm, "end": v(12.67, 4.36) * mm});
            skArc(sketch, "E137.5.46", {"start": v(32.22, 18.6) * mm, "mid": v(35.57, 10.88) * mm, "end": v(37.1, 2.6) * mm});
            skArc(sketch, "E137.5.47", {"start": v(59.06, 34.1) * mm, "mid": v(62.06, 28.28) * mm, "end": v(64.48, 22.2) * mm});
            skArc(sketch, "E137.5.48", {"start": v(52.83, 30.5) * mm, "mid": v(55.5, 25.3) * mm, "end": v(57.68, 19.86) * mm});
            skArc(sketch, "E137.5.49", {"start": v(76.73, 44.3) * mm, "mid": v(80.62, 36.74) * mm, "end": v(83.77, 28.85) * mm});
            skArc(sketch, "E137.5.50", {"start": v(58.72, 33.9) * mm, "mid": v(61.7, 28.12) * mm, "end": v(64.1, 22.07) * mm});
            skArc(sketch, "E137.5.51", {"start": v(67.55, 39) * mm, "mid": v(74.6, 22.8) * mm, "end": v(77.8, 5.44) * mm});
            skArc(sketch, "E137.5.52", {"start": v(14.55, 8.4) * mm, "mid": v(16.07, 4.91) * mm, "end": v(16.76, 1.17) * mm});
            skArc(sketch, "E137.5.53", {"start": v(44, 25.4) * mm, "mid": v(48.58, 14.85) * mm, "end": v(50.68, 3.54) * mm});
            skArc(sketch, "E137.5.54", {"start": v(41.05, 23.7) * mm, "mid": v(43.13, 19.66) * mm, "end": v(44.82, 15.43) * mm});
            skArc(sketch, "E137.5.55", {"start": v(38.1, 22) * mm, "mid": v(42.08, 12.86) * mm, "end": v(43.9, 3.07) * mm});
            skArc(sketch, "E137.5.56", {"start": v(59.06, 34.1) * mm, "mid": v(54.1, 41.52) * mm, "end": v(48.22, 48.22) * mm});
            skArc(sketch, "E137.5.57", {"start": v(76.38, 44.1) * mm, "mid": v(80.26, 36.58) * mm, "end": v(83.4, 28.72) * mm});
            skArc(sketch, "E137.5.58", {"start": v(64.6, 37.3) * mm, "mid": v(67.88, 30.94) * mm, "end": v(70.54, 24.29) * mm});
            skLineSegment(sketch, "E137.5.59", {"start": v(91.78, 6.42) * mm, "end": v(91.38, 6.39) * mm});
            skArc(sketch, "E137.5.60", {"start": v(64.95, 37.5) * mm, "mid": v(59.5, 45.66) * mm, "end": v(53.03, 53.03) * mm});
            skArc(sketch, "E137.5.61", {"start": v(64.6, 37.3) * mm, "mid": v(59.18, 45.41) * mm, "end": v(52.75, 52.75) * mm});
            skArc(sketch, "E137.5.62", {"start": v(76.38, 44.1) * mm, "mid": v(69.97, 53.7) * mm, "end": v(62.37, 62.37) * mm});
            skArc(sketch, "E137.5.63", {"start": v(6.06, 3.5) * mm, "mid": v(6.37, 2.9) * mm, "end": v(6.62, 2.28) * mm});
            skArc(sketch, "E137.5.64", {"start": v(35.5, 20.5) * mm, "mid": v(37.3, 17) * mm, "end": v(38.77, 13.35) * mm});
            skArc(sketch, "E137.5.65", {"start": v(58.72, 33.9) * mm, "mid": v(53.79, 41.27) * mm, "end": v(47.94, 47.94) * mm});
            skArc(sketch, "E137.5.66", {"start": v(47.28, 27.3) * mm, "mid": v(49.68, 22.64) * mm, "end": v(51.63, 17.78) * mm});
            skArc(sketch, "E137.5.67", {"start": v(17.84, 10.3) * mm, "mid": v(18.75, 8.54) * mm, "end": v(19.48, 6.7) * mm});
            skArc(sketch, "E137.5.68", {"start": v(11.95, 6.9) * mm, "mid": v(12.56, 5.72) * mm, "end": v(13.05, 4.5) * mm});
            skArc(sketch, "E137.5.69", {"start": v(20.78, 12) * mm, "mid": v(22.95, 7.02) * mm, "end": v(23.94, 1.67) * mm});
            skArc(sketch, "E137.5.70", {"start": v(26.33, 15.2) * mm, "mid": v(29.07, 8.89) * mm, "end": v(30.33, 2.12) * mm});
            skArc(sketch, "E137.5.71", {"start": v(53.17, 30.7) * mm, "mid": v(48.71, 37.38) * mm, "end": v(43.42, 43.42) * mm});
            skArc(sketch, "E137.5.72", {"start": v(4.67, 4.67) * mm, "mid": v(5.6, 3.5) * mm, "end": v(6.24, 2.15) * mm});
            skArc(sketch, "E137.5.73", {"start": v(52.83, 30.5) * mm, "mid": v(48.4, 37.13) * mm, "end": v(43.13, 43.13) * mm});
            skArc(sketch, "E137.5.74", {"start": v(41.05, 23.7) * mm, "mid": v(37.6, 28.86) * mm, "end": v(33.52, 33.52) * mm});
            skArc(sketch, "E137.5.75", {"start": v(29.62, 17.1) * mm, "mid": v(27.13, 20.82) * mm, "end": v(24.18, 24.18) * mm});
            skArc(sketch, "E137.5.76", {"start": v(35.16, 20.3) * mm, "mid": v(36.94, 16.84) * mm, "end": v(38.39, 13.22) * mm});
            skArc(sketch, "E137.5.77", {"start": v(61.66, 35.6) * mm, "mid": v(68.09, 20.82) * mm, "end": v(71.03, 4.97) * mm});
            skArc(sketch, "E137.6.0", {"start": v(20.6, 0) * mm, "mid": v(20.42, 2.69) * mm, "end": v(19.9, 5.33) * mm});
            skArc(sketch, "E137.6.1", {"start": v(17.2, 0) * mm, "mid": v(16.76, -3.87) * mm, "end": v(15.46, -7.54) * mm});
            skArc(sketch, "E137.6.2", {"start": v(20.2, 0) * mm, "mid": v(20.03, 2.64) * mm, "end": v(19.51, 5.23) * mm});
            skArc(sketch, "E137.6.3", {"start": v(64.4, 0) * mm, "mid": v(62.75, -14.49) * mm, "end": v(57.88, -28.23) * mm});
            skArc(sketch, "E137.6.4", {"start": v(81.4, 0) * mm, "mid": v(80.7, 10.62) * mm, "end": v(78.63, 21.07) * mm});
            skArc(sketch, "E137.6.5", {"start": v(20.2, 0) * mm, "mid": v(20.1, -1.94) * mm, "end": v(19.83, -3.85) * mm});
            skArc(sketch, "E137.6.6", {"start": v(78.4, 0) * mm, "mid": v(76.4, -17.64) * mm, "end": v(70.47, -34.37) * mm});
            skArc(sketch, "E137.6.7", {"start": v(10.4, 0) * mm, "mid": v(10.13, -2.34) * mm, "end": v(9.35, -4.56) * mm});
            skArc(sketch, "E137.6.8", {"start": v(37.6, 0) * mm, "mid": v(36.64, -8.46) * mm, "end": v(33.8, -16.48) * mm});
            skArc(sketch, "E137.6.9", {"start": v(92, 0) * mm, "mid": v(89.64, -20.7) * mm, "end": v(82.69, -40.33) * mm});
            skArc(sketch, "E137.6.10", {"start": v(27.4, 0) * mm, "mid": v(27.27, -2.63) * mm, "end": v(26.9, -5.23) * mm});
            skArc(sketch, "E137.6.11", {"start": v(27.4, 0) * mm, "mid": v(27.17, 3.58) * mm, "end": v(26.47, 7.1) * mm});
            skArc(sketch, "E137.6.12", {"start": v(88.6, 0) * mm, "mid": v(87.84, 11.56) * mm, "end": v(85.58, 22.93) * mm});
            skArc(sketch, "E137.6.13", {"start": v(85.2, 0) * mm, "mid": v(83.02, -19.17) * mm, "end": v(76.58, -37.35) * mm});
            skArc(sketch, "E137.6.14", {"start": v(54.6, 0) * mm, "mid": v(54.13, 7.13) * mm, "end": v(52.74, 14.13) * mm});
            skArc(sketch, "E137.6.15", {"start": v(54.2, 0) * mm, "mid": v(53.74, 7.07) * mm, "end": v(52.35, 14.03) * mm});
            skArc(sketch, "E137.6.16", {"start": v(91.6, 0) * mm, "mid": v(89.25, -20.6) * mm, "end": v(82.33, -40.15) * mm});
            skArc(sketch, "E137.6.17", {"start": v(81.4, 0) * mm, "mid": v(81.03, -7.8) * mm, "end": v(79.9, -15.53) * mm});
            skArc(sketch, "E137.6.18", {"start": v(30.8, 0) * mm, "mid": v(30.01, -6.93) * mm, "end": v(27.68, -13.5) * mm});
            skArc(sketch, "E137.6.19", {"start": v(58, 0) * mm, "mid": v(56.51, -13.05) * mm, "end": v(52.13, -25.43) * mm});
            skArc(sketch, "E137.6.20", {"start": v(57.6, 0) * mm, "mid": v(56.12, -12.96) * mm, "end": v(51.77, -25.25) * mm});
            skArc(sketch, "E137.6.21", {"start": v(64.8, 0) * mm, "mid": v(63.14, -14.58) * mm, "end": v(58.24, -28.4) * mm});
            skArc(sketch, "E137.6.22", {"start": v(41, 0) * mm, "mid": v(40.65, 5.35) * mm, "end": v(39.6, 10.61) * mm});
            skArc(sketch, "E137.6.23", {"start": v(10, 0) * mm, "mid": v(9.74, -2.25) * mm, "end": v(8.99, -4.38) * mm});
            skArc(sketch, "E137.6.24", {"start": v(13.8, 0) * mm, "mid": v(13.68, 1.8) * mm, "end": v(13.33, 3.57) * mm});
            skArc(sketch, "E137.6.25", {"start": v(27, 0) * mm, "mid": v(26.88, -2.59) * mm, "end": v(26.5, -5.15) * mm});
            skArc(sketch, "E137.6.26", {"start": v(33.8, 0) * mm, "mid": v(33.51, 4.41) * mm, "end": v(32.65, 8.75) * mm});
            skArc(sketch, "E137.6.27", {"start": v(71.6, 0) * mm, "mid": v(69.76, -16.1) * mm, "end": v(64.35, -31.39) * mm});
            skArc(sketch, "E137.6.28", {"start": v(47.8, 0) * mm, "mid": v(47.58, -4.58) * mm, "end": v(46.92, -9.12) * mm});
            skArc(sketch, "E137.6.29", {"start": v(13.4, 0) * mm, "mid": v(13.29, 1.75) * mm, "end": v(12.94, 3.47) * mm});
            skArc(sketch, "E137.6.30", {"start": v(54.2, 0) * mm, "mid": v(53.95, -5.2) * mm, "end": v(53.2, -10.34) * mm});
            skArc(sketch, "E137.6.31", {"start": v(81.8, 0) * mm, "mid": v(81.42, -7.84) * mm, "end": v(80.3, -15.6) * mm});
            skArc(sketch, "E137.6.32", {"start": v(75, 0) * mm, "mid": v(74.65, -7.19) * mm, "end": v(73.62, -14.31) * mm});
            skArc(sketch, "E137.6.33", {"start": v(34.2, 0) * mm, "mid": v(34.04, -3.28) * mm, "end": v(33.57, -6.53) * mm});
            skArc(sketch, "E137.6.34", {"start": v(33.8, 0) * mm, "mid": v(33.64, -3.24) * mm, "end": v(33.18, -6.45) * mm});
            skArc(sketch, "E137.6.35", {"start": v(40.6, 0) * mm, "mid": v(40.25, 5.3) * mm, "end": v(39.22, 10.5) * mm});
            skArc(sketch, "E137.6.36", {"start": v(84.8, 0) * mm, "mid": v(82.63, -19.08) * mm, "end": v(76.22, -37.17) * mm});
            skArc(sketch, "E137.6.37", {"start": v(23.6, 0) * mm, "mid": v(23, -5.3) * mm, "end": v(21.21, -10.35) * mm});
            skArc(sketch, "E137.6.38", {"start": v(7, 0) * mm, "mid": v(6.94, 0.91) * mm, "end": v(6.76, 1.81) * mm});
            skArc(sketch, "E137.6.39", {"start": v(81.8, 0) * mm, "mid": v(81.1, 10.68) * mm, "end": v(79.01, 21.17) * mm});
            skArc(sketch, "E137.6.40", {"start": v(51.2, 0) * mm, "mid": v(49.89, -11.52) * mm, "end": v(46.02, -22.44) * mm});
            skArc(sketch, "E137.6.41", {"start": v(44.4, 0) * mm, "mid": v(43.26, -9.99) * mm, "end": v(39.9, -19.46) * mm});
            skArc(sketch, "E137.6.42", {"start": v(61.4, 0) * mm, "mid": v(61.12, -5.88) * mm, "end": v(60.27, -11.72) * mm});
            skArc(sketch, "E137.6.43", {"start": v(47.8, 0) * mm, "mid": v(47.4, 6.24) * mm, "end": v(46.17, 12.37) * mm});
            skArc(sketch, "E137.6.44", {"start": v(27, 0) * mm, "mid": v(26.77, 3.52) * mm, "end": v(26.08, 6.99) * mm});
            skArc(sketch, "E137.6.45", {"start": v(13.4, 0) * mm, "mid": v(13.34, -1.28) * mm, "end": v(13.15, -2.56) * mm});
            skArc(sketch, "E137.6.46", {"start": v(37.2, 0) * mm, "mid": v(36.25, -8.37) * mm, "end": v(33.44, -16.3) * mm});
            skArc(sketch, "E137.6.47", {"start": v(68.2, 0) * mm, "mid": v(67.89, -6.54) * mm, "end": v(66.95, -13.01) * mm});
            skArc(sketch, "E137.6.48", {"start": v(61, 0) * mm, "mid": v(60.72, -5.85) * mm, "end": v(59.88, -11.64) * mm});
            skArc(sketch, "E137.6.49", {"start": v(88.6, 0) * mm, "mid": v(88.2, -8.5) * mm, "end": v(86.97, -16.9) * mm});
            skArc(sketch, "E137.6.50", {"start": v(67.8, 0) * mm, "mid": v(67.49, -6.5) * mm, "end": v(66.55, -12.94) * mm});
            skArc(sketch, "E137.6.51", {"start": v(78, 0) * mm, "mid": v(76, -17.55) * mm, "end": v(70.1, -34.2) * mm});
            skArc(sketch, "E137.6.52", {"start": v(16.8, 0) * mm, "mid": v(16.37, -3.78) * mm, "end": v(15.1, -7.36) * mm});
            skArc(sketch, "E137.6.53", {"start": v(50.8, 0) * mm, "mid": v(49.5, -11.43) * mm, "end": v(45.66, -22.27) * mm});
            skArc(sketch, "E137.6.54", {"start": v(47.4, 0) * mm, "mid": v(47.18, -4.54) * mm, "end": v(46.53, -9.04) * mm});
            skArc(sketch, "E137.6.55", {"start": v(44, 0) * mm, "mid": v(42.87, -9.9) * mm, "end": v(39.55, -19.29) * mm});
            skArc(sketch, "E137.6.56", {"start": v(68.2, 0) * mm, "mid": v(67.62, 8.9) * mm, "end": v(65.88, 17.65) * mm});
            skArc(sketch, "E137.6.57", {"start": v(88.2, 0) * mm, "mid": v(87.8, -8.45) * mm, "end": v(86.58, -16.83) * mm});
            skArc(sketch, "E137.6.58", {"start": v(74.6, 0) * mm, "mid": v(74.26, -7.15) * mm, "end": v(73.23, -14.23) * mm});
            skLineSegment(sketch, "E137.6.59", {"start": v(82.69, -40.33) * mm, "end": v(82.33, -40.15) * mm});
            skArc(sketch, "E137.6.60", {"start": v(75, 0) * mm, "mid": v(74.36, 9.79) * mm, "end": v(72.44, 19.41) * mm});
            skArc(sketch, "E137.6.61", {"start": v(74.6, 0) * mm, "mid": v(73.96, 9.74) * mm, "end": v(72.06, 19.3) * mm});
            skArc(sketch, "E137.6.62", {"start": v(88.2, 0) * mm, "mid": v(87.45, 11.51) * mm, "end": v(85.2, 22.83) * mm});
            skArc(sketch, "E137.6.63", {"start": v(7, 0) * mm, "mid": v(6.97, -0.67) * mm, "end": v(6.87, -1.34) * mm});
            skArc(sketch, "E137.6.64", {"start": v(41, 0) * mm, "mid": v(40.81, -3.93) * mm, "end": v(40.25, -7.82) * mm});
            skArc(sketch, "E137.6.65", {"start": v(67.8, 0) * mm, "mid": v(67.22, 8.85) * mm, "end": v(65.49, 17.55) * mm});
            skArc(sketch, "E137.6.66", {"start": v(54.6, 0) * mm, "mid": v(54.35, -5.23) * mm, "end": v(53.6, -10.42) * mm});
            skArc(sketch, "E137.6.67", {"start": v(20.6, 0) * mm, "mid": v(20.5, -1.97) * mm, "end": v(20.22, -3.93) * mm});
            skArc(sketch, "E137.6.68", {"start": v(13.8, 0) * mm, "mid": v(13.74, -1.32) * mm, "end": v(13.55, -2.63) * mm});
            skArc(sketch, "E137.6.69", {"start": v(24, 0) * mm, "mid": v(23.38, -5.4) * mm, "end": v(21.57, -10.52) * mm});
            skArc(sketch, "E137.6.70", {"start": v(30.4, 0) * mm, "mid": v(29.62, -6.84) * mm, "end": v(27.32, -13.33) * mm});
            skArc(sketch, "E137.6.71", {"start": v(61.4, 0) * mm, "mid": v(60.87, 8.01) * mm, "end": v(59.3, 15.9) * mm});
            skArc(sketch, "E137.6.72", {"start": v(6.38, 1.7) * mm, "mid": v(6.6, 0.23) * mm, "end": v(6.48, -1.26) * mm});
            skArc(sketch, "E137.6.73", {"start": v(61, 0) * mm, "mid": v(60.48, 7.96) * mm, "end": v(58.92, 15.79) * mm});
            skArc(sketch, "E137.6.74", {"start": v(47.4, 0) * mm, "mid": v(47, 6.19) * mm, "end": v(45.78, 12.27) * mm});
            skArc(sketch, "E137.6.75", {"start": v(34.2, 0) * mm, "mid": v(33.9, 4.46) * mm, "end": v(33.03, 8.85) * mm});
            skArc(sketch, "E137.6.76", {"start": v(40.6, 0) * mm, "mid": v(40.41, -3.9) * mm, "end": v(39.85, -7.75) * mm});
            skArc(sketch, "E137.6.77", {"start": v(71.2, 0) * mm, "mid": v(69.38, -16.02) * mm, "end": v(64, -31.21) * mm});
            skArc(sketch, "E137.7.0", {"start": v(17.84, -10.3) * mm, "mid": v(19.03, -7.88) * mm, "end": v(19.9, -5.33) * mm});
            skArc(sketch, "E137.7.1", {"start": v(14.9, -8.6) * mm, "mid": v(12.58, -11.73) * mm, "end": v(9.62, -14.26) * mm});
            skArc(sketch, "E137.7.2", {"start": v(17.5, -10.1) * mm, "mid": v(18.66, -7.73) * mm, "end": v(19.51, -5.23) * mm});
            skArc(sketch, "E137.7.3", {"start": v(55.77, -32.2) * mm, "mid": v(47.1, -43.92) * mm, "end": v(36.01, -53.4) * mm});
            skArc(sketch, "E137.7.4", {"start": v(70.5, -40.7) * mm, "mid": v(75.2, -31.15) * mm, "end": v(78.63, -21.07) * mm});
            skArc(sketch, "E137.7.5", {"start": v(17.5, -10.1) * mm, "mid": v(16.45, -11.73) * mm, "end": v(15.25, -13.25) * mm});
            skArc(sketch, "E137.7.6", {"start": v(67.9, -39.2) * mm, "mid": v(57.34, -53.47) * mm, "end": v(43.84, -65) * mm});
            skArc(sketch, "E137.7.7", {"start": v(9, -5.2) * mm, "mid": v(7.6, -7.1) * mm, "end": v(5.82, -8.62) * mm});
            skArc(sketch, "E137.7.8", {"start": v(32.56, -18.8) * mm, "mid": v(27.5, -25.64) * mm, "end": v(21.03, -31.17) * mm});
            skArc(sketch, "E137.7.9", {"start": v(79.67, -46) * mm, "mid": v(67.28, -62.74) * mm, "end": v(51.45, -76.27) * mm});
            skArc(sketch, "E137.7.10", {"start": v(23.73, -13.7) * mm, "mid": v(22.3, -15.91) * mm, "end": v(20.68, -17.98) * mm});
            skArc(sketch, "E137.7.11", {"start": v(23.73, -13.7) * mm, "mid": v(25.31, -10.49) * mm, "end": v(26.47, -7.1) * mm});
            skArc(sketch, "E137.7.12", {"start": v(76.73, -44.3) * mm, "mid": v(81.86, -33.9) * mm, "end": v(85.58, -22.93) * mm});
            skArc(sketch, "E137.7.13", {"start": v(73.79, -42.6) * mm, "mid": v(62.31, -58.1) * mm, "end": v(47.64, -70.63) * mm});
            skArc(sketch, "E137.7.14", {"start": v(47.28, -27.3) * mm, "mid": v(50.44, -20.9) * mm, "end": v(52.74, -14.13) * mm});
            skArc(sketch, "E137.7.15", {"start": v(46.94, -27.1) * mm, "mid": v(50.07, -20.74) * mm, "end": v(52.35, -14.03) * mm});
            skArc(sketch, "E137.7.16", {"start": v(79.33, -45.8) * mm, "mid": v(67, -62.47) * mm, "end": v(51.22, -75.94) * mm});
            skArc(sketch, "E137.7.17", {"start": v(70.5, -40.7) * mm, "mid": v(66.27, -47.27) * mm, "end": v(61.43, -53.4) * mm});
            skArc(sketch, "E137.7.18", {"start": v(26.67, -15.4) * mm, "mid": v(22.53, -21) * mm, "end": v(17.22, -25.53) * mm});
            skArc(sketch, "E137.7.19", {"start": v(50.23, -29) * mm, "mid": v(42.42, -39.56) * mm, "end": v(32.43, -48.08) * mm});
            skArc(sketch, "E137.7.20", {"start": v(49.88, -28.8) * mm, "mid": v(42.13, -39.28) * mm, "end": v(32.2, -47.75) * mm});
            skArc(sketch, "E137.7.21", {"start": v(56.12, -32.4) * mm, "mid": v(47.4, -44.2) * mm, "end": v(36.24, -53.72) * mm});
            skArc(sketch, "E137.7.22", {"start": v(35.5, -20.5) * mm, "mid": v(37.88, -15.7) * mm, "end": v(39.6, -10.61) * mm});
            skArc(sketch, "E137.7.23", {"start": v(8.66, -5) * mm, "mid": v(7.31, -6.82) * mm, "end": v(5.6, -8.3) * mm});
            skArc(sketch, "E137.7.24", {"start": v(11.95, -6.9) * mm, "mid": v(12.75, -5.28) * mm, "end": v(13.33, -3.57) * mm});
            skArc(sketch, "E137.7.25", {"start": v(23.38, -13.5) * mm, "mid": v(21.98, -15.68) * mm, "end": v(20.38, -17.71) * mm});
            skArc(sketch, "E137.7.26", {"start": v(29.27, -16.9) * mm, "mid": v(31.23, -12.93) * mm, "end": v(32.65, -8.75) * mm});
            skArc(sketch, "E137.7.27", {"start": v(62, -35.8) * mm, "mid": v(52.36, -48.83) * mm, "end": v(40.04, -59.36) * mm});
            skArc(sketch, "E137.7.28", {"start": v(41.4, -23.9) * mm, "mid": v(38.91, -27.76) * mm, "end": v(36.08, -31.36) * mm});
            skArc(sketch, "E137.7.29", {"start": v(11.6, -6.7) * mm, "mid": v(12.38, -5.13) * mm, "end": v(12.94, -3.47) * mm});
            skArc(sketch, "E137.7.30", {"start": v(46.94, -27.1) * mm, "mid": v(44.13, -31.47) * mm, "end": v(40.9, -35.56) * mm});
            skArc(sketch, "E137.7.31", {"start": v(70.84, -40.9) * mm, "mid": v(66.6, -47.5) * mm, "end": v(61.74, -53.67) * mm});
            skArc(sketch, "E137.7.32", {"start": v(64.95, -37.5) * mm, "mid": v(61.06, -43.55) * mm, "end": v(56.6, -49.2) * mm});
            skArc(sketch, "E137.7.33", {"start": v(29.62, -17.1) * mm, "mid": v(27.84, -19.86) * mm, "end": v(25.81, -22.44) * mm});
            skArc(sketch, "E137.7.34", {"start": v(29.27, -16.9) * mm, "mid": v(27.52, -19.63) * mm, "end": v(25.5, -22.17) * mm});
            skArc(sketch, "E137.7.35", {"start": v(35.16, -20.3) * mm, "mid": v(37.5, -15.54) * mm, "end": v(39.22, -10.5) * mm});
            skArc(sketch, "E137.7.36", {"start": v(73.44, -42.4) * mm, "mid": v(62.02, -57.83) * mm, "end": v(47.42, -70.3) * mm});
            skArc(sketch, "E137.7.37", {"start": v(20.44, -11.8) * mm, "mid": v(17.26, -16.1) * mm, "end": v(13.2, -19.57) * mm});
            skArc(sketch, "E137.7.38", {"start": v(6.06, -3.5) * mm, "mid": v(6.47, -2.68) * mm, "end": v(6.76, -1.81) * mm});
            skArc(sketch, "E137.7.39", {"start": v(70.84, -40.9) * mm, "mid": v(75.57, -31.3) * mm, "end": v(79.01, -21.17) * mm});
            skArc(sketch, "E137.7.40", {"start": v(44.34, -25.6) * mm, "mid": v(37.45, -34.92) * mm, "end": v(28.63, -42.45) * mm});
            skArc(sketch, "E137.7.41", {"start": v(38.45, -22.2) * mm, "mid": v(32.47, -30.28) * mm, "end": v(24.83, -36.8) * mm});
            skArc(sketch, "E137.7.42", {"start": v(53.17, -30.7) * mm, "mid": v(49.99, -35.66) * mm, "end": v(46.34, -40.28) * mm});
            skArc(sketch, "E137.7.43", {"start": v(41.4, -23.9) * mm, "mid": v(44.16, -18.3) * mm, "end": v(46.17, -12.37) * mm});
            skArc(sketch, "E137.7.44", {"start": v(23.38, -13.5) * mm, "mid": v(24.94, -10.33) * mm, "end": v(26.08, -6.99) * mm});
            skArc(sketch, "E137.7.45", {"start": v(11.6, -6.7) * mm, "mid": v(10.9, -7.78) * mm, "end": v(10.11, -8.8) * mm});
            skArc(sketch, "E137.7.46", {"start": v(32.22, -18.6) * mm, "mid": v(27.2, -25.37) * mm, "end": v(20.8, -30.84) * mm});
            skArc(sketch, "E137.7.47", {"start": v(59.06, -34.1) * mm, "mid": v(55.52, -39.6) * mm, "end": v(51.47, -44.74) * mm});
            skArc(sketch, "E137.7.48", {"start": v(52.83, -30.5) * mm, "mid": v(49.66, -35.42) * mm, "end": v(46.04, -40.02) * mm});
            skArc(sketch, "E137.7.49", {"start": v(76.73, -44.3) * mm, "mid": v(72.13, -51.45) * mm, "end": v(66.87, -58.13) * mm});
            skArc(sketch, "E137.7.50", {"start": v(58.72, -33.9) * mm, "mid": v(55.2, -39.37) * mm, "end": v(51.17, -44.48) * mm});
            skArc(sketch, "E137.7.51", {"start": v(67.55, -39) * mm, "mid": v(57.05, -53.2) * mm, "end": v(43.62, -64.66) * mm});
            skArc(sketch, "E137.7.52", {"start": v(14.55, -8.4) * mm, "mid": v(12.29, -11.46) * mm, "end": v(9.4, -13.93) * mm});
            skArc(sketch, "E137.7.53", {"start": v(44, -25.4) * mm, "mid": v(37.15, -34.65) * mm, "end": v(28.4, -42.12) * mm});
            skArc(sketch, "E137.7.54", {"start": v(41.05, -23.7) * mm, "mid": v(38.59, -27.53) * mm, "end": v(35.77, -31.1) * mm});
            skArc(sketch, "E137.7.55", {"start": v(38.1, -22) * mm, "mid": v(32.18, -30) * mm, "end": v(24.6, -36.48) * mm});
            skArc(sketch, "E137.7.56", {"start": v(59.06, -34.1) * mm, "mid": v(63, -26.1) * mm, "end": v(65.88, -17.65) * mm});
            skArc(sketch, "E137.7.57", {"start": v(76.38, -44.1) * mm, "mid": v(71.8, -51.22) * mm, "end": v(66.57, -57.86) * mm});
            skArc(sketch, "E137.7.58", {"start": v(64.6, -37.3) * mm, "mid": v(60.73, -43.32) * mm, "end": v(56.3, -48.94) * mm});
            skLineSegment(sketch, "E137.7.59", {"start": v(51.45, -76.27) * mm, "end": v(51.22, -75.94) * mm});
            skArc(sketch, "E137.7.60", {"start": v(64.95, -37.5) * mm, "mid": v(69.3, -28.7) * mm, "end": v(72.44, -19.41) * mm});
            skArc(sketch, "E137.7.61", {"start": v(64.6, -37.3) * mm, "mid": v(68.92, -28.55) * mm, "end": v(72.06, -19.3) * mm});
            skArc(sketch, "E137.7.62", {"start": v(76.38, -44.1) * mm, "mid": v(81.49, -33.75) * mm, "end": v(85.2, -22.83) * mm});
            skArc(sketch, "E137.7.63", {"start": v(6.06, -3.5) * mm, "mid": v(5.7, -4.06) * mm, "end": v(5.28, -4.6) * mm});
            skArc(sketch, "E137.7.64", {"start": v(35.5, -20.5) * mm, "mid": v(33.38, -23.8) * mm, "end": v(30.94, -26.9) * mm});
            skArc(sketch, "E137.7.65", {"start": v(58.72, -33.9) * mm, "mid": v(62.64, -25.95) * mm, "end": v(65.49, -17.55) * mm});
            skArc(sketch, "E137.7.66", {"start": v(47.28, -27.3) * mm, "mid": v(44.45, -31.7) * mm, "end": v(41.2, -35.82) * mm});
            skArc(sketch, "E137.7.67", {"start": v(17.84, -10.3) * mm, "mid": v(16.77, -11.96) * mm, "end": v(15.55, -13.51) * mm});
            skArc(sketch, "E137.7.68", {"start": v(11.95, -6.9) * mm, "mid": v(11.23, -8.01) * mm, "end": v(10.41, -9.05) * mm});
            skArc(sketch, "E137.7.69", {"start": v(20.78, -12) * mm, "mid": v(17.55, -16.37) * mm, "end": v(13.42, -19.9) * mm});
            skArc(sketch, "E137.7.70", {"start": v(26.33, -15.2) * mm, "mid": v(22.23, -20.73) * mm, "end": v(17, -25.2) * mm});
            skArc(sketch, "E137.7.71", {"start": v(53.17, -30.7) * mm, "mid": v(56.73, -23.5) * mm, "end": v(59.3, -15.9) * mm});
            skArc(sketch, "E137.7.72", {"start": v(6.38, -1.7) * mm, "mid": v(5.83, -3.1) * mm, "end": v(4.98, -4.33) * mm});
            skArc(sketch, "E137.7.73", {"start": v(52.83, -30.5) * mm, "mid": v(56.36, -23.34) * mm, "end": v(58.92, -15.79) * mm});
            skArc(sketch, "E137.7.74", {"start": v(41.05, -23.7) * mm, "mid": v(43.8, -18.14) * mm, "end": v(45.78, -12.27) * mm});
            skArc(sketch, "E137.7.75", {"start": v(29.62, -17.1) * mm, "mid": v(31.6, -13.09) * mm, "end": v(33.03, -8.85) * mm});
            skArc(sketch, "E137.7.76", {"start": v(35.16, -20.3) * mm, "mid": v(33.05, -23.58) * mm, "end": v(30.64, -26.64) * mm});
            skArc(sketch, "E137.7.77", {"start": v(61.66, -35.6) * mm, "mid": v(52.07, -48.56) * mm, "end": v(39.81, -59.03) * mm});
            skArc(sketch, "E137.8.0", {"start": v(10.3, -17.84) * mm, "mid": v(12.54, -16.34) * mm, "end": v(14.57, -14.57) * mm});
            skArc(sketch, "E137.8.1", {"start": v(8.6, -14.9) * mm, "mid": v(5.03, -16.45) * mm, "end": v(1.2, -17.16) * mm});
            skArc(sketch, "E137.8.2", {"start": v(10.1, -17.5) * mm, "mid": v(12.3, -16.03) * mm, "end": v(14.28, -14.28) * mm});
            skArc(sketch, "E137.8.3", {"start": v(32.2, -55.77) * mm, "mid": v(18.83, -61.59) * mm, "end": v(4.5, -64.24) * mm});
            skArc(sketch, "E137.8.4", {"start": v(40.7, -70.5) * mm, "mid": v(49.55, -64.58) * mm, "end": v(57.56, -57.56) * mm});
            skArc(sketch, "E137.8.5", {"start": v(10.1, -17.5) * mm, "mid": v(8.38, -18.38) * mm, "end": v(6.58, -19.1) * mm});
            skArc(sketch, "E137.8.6", {"start": v(39.2, -67.9) * mm, "mid": v(22.92, -74.97) * mm, "end": v(5.47, -78.2) * mm});
            skArc(sketch, "E137.8.7", {"start": v(5.2, -9) * mm, "mid": v(3.04, -9.95) * mm, "end": v(0.73, -10.37) * mm});
            skArc(sketch, "E137.8.8", {"start": v(18.8, -32.56) * mm, "mid": v(11, -35.96) * mm, "end": v(2.62, -37.5) * mm});
            skArc(sketch, "E137.8.9", {"start": v(46, -79.67) * mm, "mid": v(26.9, -87.98) * mm, "end": v(6.42, -91.78) * mm});
            skArc(sketch, "E137.8.10", {"start": v(13.7, -23.73) * mm, "mid": v(11.36, -24.93) * mm, "end": v(8.92, -25.9) * mm});
            skArc(sketch, "E137.8.11", {"start": v(13.7, -23.73) * mm, "mid": v(16.68, -21.74) * mm, "end": v(19.37, -19.37) * mm});
            skArc(sketch, "E137.8.12", {"start": v(44.3, -76.73) * mm, "mid": v(53.94, -70.3) * mm, "end": v(62.65, -62.65) * mm});
            skArc(sketch, "E137.8.13", {"start": v(42.6, -73.79) * mm, "mid": v(24.91, -81.48) * mm, "end": v(5.94, -85) * mm});
            skArc(sketch, "E137.8.14", {"start": v(27.3, -47.28) * mm, "mid": v(33.24, -43.32) * mm, "end": v(38.6, -38.6) * mm});
            skArc(sketch, "E137.8.15", {"start": v(27.1, -46.94) * mm, "mid": v(33, -43) * mm, "end": v(38.33, -38.33) * mm});
            skArc(sketch, "E137.8.16", {"start": v(45.8, -79.33) * mm, "mid": v(26.78, -87.6) * mm, "end": v(6.39, -91.38) * mm});
            skArc(sketch, "E137.8.17", {"start": v(40.7, -70.5) * mm, "mid": v(33.76, -74.07) * mm, "end": v(26.5, -76.97) * mm});
            skArc(sketch, "E137.8.18", {"start": v(15.4, -26.67) * mm, "mid": v(9, -29.45) * mm, "end": v(2.15, -30.72) * mm});
            skArc(sketch, "E137.8.19", {"start": v(29, -50.23) * mm, "mid": v(16.96, -55.47) * mm, "end": v(4.05, -57.86) * mm});
            skArc(sketch, "E137.8.20", {"start": v(28.8, -49.88) * mm, "mid": v(16.84, -55.08) * mm, "end": v(4.02, -57.46) * mm});
            skArc(sketch, "E137.8.21", {"start": v(32.4, -56.12) * mm, "mid": v(18.95, -61.97) * mm, "end": v(4.52, -64.64) * mm});
            skArc(sketch, "E137.8.22", {"start": v(20.5, -35.5) * mm, "mid": v(24.96, -32.53) * mm, "end": v(29, -29) * mm});
            skArc(sketch, "E137.8.23", {"start": v(5, -8.66) * mm, "mid": v(2.92, -9.56) * mm, "end": v(0.7, -9.98) * mm});
            skArc(sketch, "E137.8.24", {"start": v(6.9, -11.95) * mm, "mid": v(8.4, -10.95) * mm, "end": v(9.76, -9.76) * mm});
            skArc(sketch, "E137.8.25", {"start": v(13.5, -23.38) * mm, "mid": v(11.2, -24.57) * mm, "end": v(8.8, -25.53) * mm});
            skArc(sketch, "E137.8.26", {"start": v(16.9, -29.27) * mm, "mid": v(20.58, -26.82) * mm, "end": v(23.9, -23.9) * mm});
            skArc(sketch, "E137.8.27", {"start": v(35.8, -62) * mm, "mid": v(20.93, -68.47) * mm, "end": v(5, -71.43) * mm});
            skArc(sketch, "E137.8.28", {"start": v(23.9, -41.4) * mm, "mid": v(19.82, -43.5) * mm, "end": v(15.56, -45.2) * mm});
            skArc(sketch, "E137.8.29", {"start": v(6.7, -11.6) * mm, "mid": v(8.16, -10.63) * mm, "end": v(9.48, -9.48) * mm});
            skArc(sketch, "E137.8.30", {"start": v(27.1, -46.94) * mm, "mid": v(22.48, -49.32) * mm, "end": v(17.65, -51.25) * mm});
            skArc(sketch, "E137.8.31", {"start": v(40.9, -70.84) * mm, "mid": v(33.92, -74.43) * mm, "end": v(26.63, -77.34) * mm});
            skArc(sketch, "E137.8.32", {"start": v(37.5, -64.95) * mm, "mid": v(31.1, -68.25) * mm, "end": v(24.42, -70.91) * mm});
            skArc(sketch, "E137.8.33", {"start": v(17.1, -29.62) * mm, "mid": v(14.18, -31.12) * mm, "end": v(11.13, -32.34) * mm});
            skArc(sketch, "E137.8.34", {"start": v(16.9, -29.27) * mm, "mid": v(14.02, -30.76) * mm, "end": v(11, -31.96) * mm});
            skArc(sketch, "E137.8.35", {"start": v(20.3, -35.16) * mm, "mid": v(24.72, -32.21) * mm, "end": v(28.7, -28.7) * mm});
            skArc(sketch, "E137.8.36", {"start": v(42.4, -73.44) * mm, "mid": v(24.8, -81.1) * mm, "end": v(5.92, -84.6) * mm});
            skArc(sketch, "E137.8.37", {"start": v(11.8, -20.44) * mm, "mid": v(6.9, -22.57) * mm, "end": v(1.65, -23.54) * mm});
            skArc(sketch, "E137.8.38", {"start": v(3.5, -6.06) * mm, "mid": v(4.26, -5.55) * mm, "end": v(4.95, -4.95) * mm});
            skArc(sketch, "E137.8.39", {"start": v(40.9, -70.84) * mm, "mid": v(49.8, -64.9) * mm, "end": v(57.84, -57.84) * mm});
            skArc(sketch, "E137.8.40", {"start": v(25.6, -44.34) * mm, "mid": v(14.97, -48.96) * mm, "end": v(3.57, -51.08) * mm});
            skArc(sketch, "E137.8.41", {"start": v(22.2, -38.45) * mm, "mid": v(12.98, -42.46) * mm, "end": v(3.1, -44.3) * mm});
            skArc(sketch, "E137.8.42", {"start": v(30.7, -53.17) * mm, "mid": v(25.46, -55.87) * mm, "end": v(19.99, -58.05) * mm});
            skArc(sketch, "E137.8.43", {"start": v(23.9, -41.4) * mm, "mid": v(29.1, -37.92) * mm, "end": v(33.8, -33.8) * mm});
            skArc(sketch, "E137.8.44", {"start": v(13.5, -23.38) * mm, "mid": v(16.44, -21.42) * mm, "end": v(19.1, -19.1) * mm});
            skArc(sketch, "E137.8.45", {"start": v(6.7, -11.6) * mm, "mid": v(5.56, -12.2) * mm, "end": v(4.36, -12.67) * mm});
            skArc(sketch, "E137.8.46", {"start": v(18.6, -32.22) * mm, "mid": v(10.88, -35.57) * mm, "end": v(2.6, -37.1) * mm});
            skArc(sketch, "E137.8.47", {"start": v(34.1, -59.06) * mm, "mid": v(28.28, -62.06) * mm, "end": v(22.2, -64.48) * mm});
            skArc(sketch, "E137.8.48", {"start": v(30.5, -52.83) * mm, "mid": v(25.3, -55.5) * mm, "end": v(19.86, -57.68) * mm});
            skArc(sketch, "E137.8.49", {"start": v(44.3, -76.73) * mm, "mid": v(36.74, -80.62) * mm, "end": v(28.85, -83.77) * mm});
            skArc(sketch, "E137.8.50", {"start": v(33.9, -58.72) * mm, "mid": v(28.12, -61.7) * mm, "end": v(22.07, -64.1) * mm});
            skArc(sketch, "E137.8.51", {"start": v(39, -67.55) * mm, "mid": v(22.8, -74.6) * mm, "end": v(5.44, -77.8) * mm});
            skArc(sketch, "E137.8.52", {"start": v(8.4, -14.55) * mm, "mid": v(4.91, -16.07) * mm, "end": v(1.17, -16.76) * mm});
            skArc(sketch, "E137.8.53", {"start": v(25.4, -44) * mm, "mid": v(14.85, -48.58) * mm, "end": v(3.54, -50.68) * mm});
            skArc(sketch, "E137.8.54", {"start": v(23.7, -41.05) * mm, "mid": v(19.66, -43.13) * mm, "end": v(15.43, -44.82) * mm});
            skArc(sketch, "E137.8.55", {"start": v(22, -38.1) * mm, "mid": v(12.86, -42.08) * mm, "end": v(3.07, -43.9) * mm});
            skArc(sketch, "E137.8.56", {"start": v(34.1, -59.06) * mm, "mid": v(41.52, -54.1) * mm, "end": v(48.22, -48.22) * mm});
            skArc(sketch, "E137.8.57", {"start": v(44.1, -76.38) * mm, "mid": v(36.58, -80.26) * mm, "end": v(28.72, -83.4) * mm});
            skArc(sketch, "E137.8.58", {"start": v(37.3, -64.6) * mm, "mid": v(30.94, -67.88) * mm, "end": v(24.29, -70.54) * mm});
            skLineSegment(sketch, "E137.8.59", {"start": v(6.42, -91.78) * mm, "end": v(6.39, -91.38) * mm});
            skArc(sketch, "E137.8.60", {"start": v(37.5, -64.95) * mm, "mid": v(45.66, -59.5) * mm, "end": v(53.03, -53.03) * mm});
            skArc(sketch, "E137.8.61", {"start": v(37.3, -64.6) * mm, "mid": v(45.41, -59.18) * mm, "end": v(52.75, -52.75) * mm});
            skArc(sketch, "E137.8.62", {"start": v(44.1, -76.38) * mm, "mid": v(53.7, -69.97) * mm, "end": v(62.37, -62.37) * mm});
            skArc(sketch, "E137.8.63", {"start": v(3.5, -6.06) * mm, "mid": v(2.9, -6.37) * mm, "end": v(2.28, -6.62) * mm});
            skArc(sketch, "E137.8.64", {"start": v(20.5, -35.5) * mm, "mid": v(17, -37.3) * mm, "end": v(13.35, -38.77) * mm});
            skArc(sketch, "E137.8.65", {"start": v(33.9, -58.72) * mm, "mid": v(41.27, -53.79) * mm, "end": v(47.94, -47.94) * mm});
            skArc(sketch, "E137.8.66", {"start": v(27.3, -47.28) * mm, "mid": v(22.64, -49.68) * mm, "end": v(17.78, -51.63) * mm});
            skArc(sketch, "E137.8.67", {"start": v(10.3, -17.84) * mm, "mid": v(8.54, -18.75) * mm, "end": v(6.7, -19.48) * mm});
            skArc(sketch, "E137.8.68", {"start": v(6.9, -11.95) * mm, "mid": v(5.72, -12.56) * mm, "end": v(4.5, -13.05) * mm});
            skArc(sketch, "E137.8.69", {"start": v(12, -20.78) * mm, "mid": v(7.02, -22.95) * mm, "end": v(1.67, -23.94) * mm});
            skArc(sketch, "E137.8.70", {"start": v(15.2, -26.33) * mm, "mid": v(8.89, -29.07) * mm, "end": v(2.12, -30.33) * mm});
            skArc(sketch, "E137.8.71", {"start": v(30.7, -53.17) * mm, "mid": v(37.38, -48.71) * mm, "end": v(43.42, -43.42) * mm});
            skArc(sketch, "E137.8.72", {"start": v(4.67, -4.67) * mm, "mid": v(3.5, -5.6) * mm, "end": v(2.15, -6.24) * mm});
            skArc(sketch, "E137.8.73", {"start": v(30.5, -52.83) * mm, "mid": v(37.13, -48.4) * mm, "end": v(43.13, -43.13) * mm});
            skArc(sketch, "E137.8.74", {"start": v(23.7, -41.05) * mm, "mid": v(28.86, -37.6) * mm, "end": v(33.52, -33.52) * mm});
            skArc(sketch, "E137.8.75", {"start": v(17.1, -29.62) * mm, "mid": v(20.82, -27.13) * mm, "end": v(24.18, -24.18) * mm});
            skArc(sketch, "E137.8.76", {"start": v(20.3, -35.16) * mm, "mid": v(16.84, -36.94) * mm, "end": v(13.22, -38.39) * mm});
            skArc(sketch, "E137.8.77", {"start": v(35.6, -61.66) * mm, "mid": v(20.82, -68.09) * mm, "end": v(4.97, -71.03) * mm});
            skArc(sketch, "E137.9.0", {"start": v(0, -20.6) * mm, "mid": v(2.69, -20.42) * mm, "end": v(5.33, -19.9) * mm});
            skArc(sketch, "E137.9.1", {"start": v(0, -17.2) * mm, "mid": v(-3.87, -16.76) * mm, "end": v(-7.54, -15.46) * mm});
            skArc(sketch, "E137.9.2", {"start": v(0, -20.2) * mm, "mid": v(2.64, -20.03) * mm, "end": v(5.23, -19.51) * mm});
            skArc(sketch, "E137.9.3", {"start": v(0, -64.4) * mm, "mid": v(-14.49, -62.75) * mm, "end": v(-28.23, -57.88) * mm});
            skArc(sketch, "E137.9.4", {"start": v(0, -81.4) * mm, "mid": v(10.62, -80.7) * mm, "end": v(21.07, -78.63) * mm});
            skArc(sketch, "E137.9.5", {"start": v(0, -20.2) * mm, "mid": v(-1.94, -20.1) * mm, "end": v(-3.85, -19.83) * mm});
            skArc(sketch, "E137.9.6", {"start": v(0, -78.4) * mm, "mid": v(-17.64, -76.4) * mm, "end": v(-34.37, -70.47) * mm});
            skArc(sketch, "E137.9.7", {"start": v(0, -10.4) * mm, "mid": v(-2.34, -10.13) * mm, "end": v(-4.56, -9.35) * mm});
            skArc(sketch, "E137.9.8", {"start": v(0, -37.6) * mm, "mid": v(-8.46, -36.64) * mm, "end": v(-16.48, -33.8) * mm});
            skArc(sketch, "E137.9.9", {"start": v(0, -92) * mm, "mid": v(-20.7, -89.64) * mm, "end": v(-40.33, -82.69) * mm});
            skArc(sketch, "E137.9.10", {"start": v(0, -27.4) * mm, "mid": v(-2.63, -27.27) * mm, "end": v(-5.23, -26.9) * mm});
            skArc(sketch, "E137.9.11", {"start": v(0, -27.4) * mm, "mid": v(3.58, -27.17) * mm, "end": v(7.1, -26.47) * mm});
            skArc(sketch, "E137.9.12", {"start": v(0, -88.6) * mm, "mid": v(11.56, -87.84) * mm, "end": v(22.93, -85.58) * mm});
            skArc(sketch, "E137.9.13", {"start": v(0, -85.2) * mm, "mid": v(-19.17, -83.02) * mm, "end": v(-37.35, -76.58) * mm});
            skArc(sketch, "E137.9.14", {"start": v(0, -54.6) * mm, "mid": v(7.13, -54.13) * mm, "end": v(14.13, -52.74) * mm});
            skArc(sketch, "E137.9.15", {"start": v(0, -54.2) * mm, "mid": v(7.07, -53.74) * mm, "end": v(14.03, -52.35) * mm});
            skArc(sketch, "E137.9.16", {"start": v(0, -91.6) * mm, "mid": v(-20.6, -89.25) * mm, "end": v(-40.15, -82.33) * mm});
            skArc(sketch, "E137.9.17", {"start": v(0, -81.4) * mm, "mid": v(-7.8, -81.03) * mm, "end": v(-15.53, -79.9) * mm});
            skArc(sketch, "E137.9.18", {"start": v(0, -30.8) * mm, "mid": v(-6.93, -30.01) * mm, "end": v(-13.5, -27.68) * mm});
            skArc(sketch, "E137.9.19", {"start": v(0, -58) * mm, "mid": v(-13.05, -56.51) * mm, "end": v(-25.43, -52.13) * mm});
            skArc(sketch, "E137.9.20", {"start": v(0, -57.6) * mm, "mid": v(-12.96, -56.12) * mm, "end": v(-25.25, -51.77) * mm});
            skArc(sketch, "E137.9.21", {"start": v(0, -64.8) * mm, "mid": v(-14.58, -63.14) * mm, "end": v(-28.4, -58.24) * mm});
            skArc(sketch, "E137.9.22", {"start": v(0, -41) * mm, "mid": v(5.35, -40.65) * mm, "end": v(10.61, -39.6) * mm});
            skArc(sketch, "E137.9.23", {"start": v(0, -10) * mm, "mid": v(-2.25, -9.74) * mm, "end": v(-4.38, -8.99) * mm});
            skArc(sketch, "E137.9.24", {"start": v(0, -13.8) * mm, "mid": v(1.8, -13.68) * mm, "end": v(3.57, -13.33) * mm});
            skArc(sketch, "E137.9.25", {"start": v(0, -27) * mm, "mid": v(-2.59, -26.88) * mm, "end": v(-5.15, -26.5) * mm});
            skArc(sketch, "E137.9.26", {"start": v(0, -33.8) * mm, "mid": v(4.41, -33.51) * mm, "end": v(8.75, -32.65) * mm});
            skArc(sketch, "E137.9.27", {"start": v(0, -71.6) * mm, "mid": v(-16.1, -69.76) * mm, "end": v(-31.39, -64.35) * mm});
            skArc(sketch, "E137.9.28", {"start": v(0, -47.8) * mm, "mid": v(-4.58, -47.58) * mm, "end": v(-9.12, -46.92) * mm});
            skArc(sketch, "E137.9.29", {"start": v(0, -13.4) * mm, "mid": v(1.75, -13.29) * mm, "end": v(3.47, -12.94) * mm});
            skArc(sketch, "E137.9.30", {"start": v(0, -54.2) * mm, "mid": v(-5.2, -53.95) * mm, "end": v(-10.34, -53.2) * mm});
            skArc(sketch, "E137.9.31", {"start": v(0, -81.8) * mm, "mid": v(-7.84, -81.42) * mm, "end": v(-15.6, -80.3) * mm});
            skArc(sketch, "E137.9.32", {"start": v(0, -75) * mm, "mid": v(-7.19, -74.65) * mm, "end": v(-14.31, -73.62) * mm});
            skArc(sketch, "E137.9.33", {"start": v(0, -34.2) * mm, "mid": v(-3.28, -34.04) * mm, "end": v(-6.53, -33.57) * mm});
            skArc(sketch, "E137.9.34", {"start": v(0, -33.8) * mm, "mid": v(-3.24, -33.64) * mm, "end": v(-6.45, -33.18) * mm});
            skArc(sketch, "E137.9.35", {"start": v(0, -40.6) * mm, "mid": v(5.3, -40.25) * mm, "end": v(10.5, -39.22) * mm});
            skArc(sketch, "E137.9.36", {"start": v(0, -84.8) * mm, "mid": v(-19.08, -82.63) * mm, "end": v(-37.17, -76.22) * mm});
            skArc(sketch, "E137.9.37", {"start": v(0, -23.6) * mm, "mid": v(-5.3, -23) * mm, "end": v(-10.35, -21.21) * mm});
            skArc(sketch, "E137.9.38", {"start": v(0, -7) * mm, "mid": v(0.91, -6.94) * mm, "end": v(1.81, -6.76) * mm});
            skArc(sketch, "E137.9.39", {"start": v(0, -81.8) * mm, "mid": v(10.68, -81.1) * mm, "end": v(21.17, -79.01) * mm});
            skArc(sketch, "E137.9.40", {"start": v(0, -51.2) * mm, "mid": v(-11.52, -49.89) * mm, "end": v(-22.44, -46.02) * mm});
            skArc(sketch, "E137.9.41", {"start": v(0, -44.4) * mm, "mid": v(-9.99, -43.26) * mm, "end": v(-19.46, -39.9) * mm});
            skArc(sketch, "E137.9.42", {"start": v(0, -61.4) * mm, "mid": v(-5.88, -61.12) * mm, "end": v(-11.72, -60.27) * mm});
            skArc(sketch, "E137.9.43", {"start": v(0, -47.8) * mm, "mid": v(6.24, -47.4) * mm, "end": v(12.37, -46.17) * mm});
            skArc(sketch, "E137.9.44", {"start": v(0, -27) * mm, "mid": v(3.52, -26.77) * mm, "end": v(6.99, -26.08) * mm});
            skArc(sketch, "E137.9.45", {"start": v(0, -13.4) * mm, "mid": v(-1.28, -13.34) * mm, "end": v(-2.56, -13.15) * mm});
            skArc(sketch, "E137.9.46", {"start": v(0, -37.2) * mm, "mid": v(-8.37, -36.25) * mm, "end": v(-16.3, -33.44) * mm});
            skArc(sketch, "E137.9.47", {"start": v(0, -68.2) * mm, "mid": v(-6.54, -67.89) * mm, "end": v(-13.01, -66.95) * mm});
            skArc(sketch, "E137.9.48", {"start": v(0, -61) * mm, "mid": v(-5.85, -60.72) * mm, "end": v(-11.64, -59.88) * mm});
            skArc(sketch, "E137.9.49", {"start": v(0, -88.6) * mm, "mid": v(-8.5, -88.2) * mm, "end": v(-16.9, -86.97) * mm});
            skArc(sketch, "E137.9.50", {"start": v(0, -67.8) * mm, "mid": v(-6.5, -67.49) * mm, "end": v(-12.94, -66.55) * mm});
            skArc(sketch, "E137.9.51", {"start": v(0, -78) * mm, "mid": v(-17.55, -76) * mm, "end": v(-34.2, -70.1) * mm});
            skArc(sketch, "E137.9.52", {"start": v(0, -16.8) * mm, "mid": v(-3.78, -16.37) * mm, "end": v(-7.36, -15.1) * mm});
            skArc(sketch, "E137.9.53", {"start": v(0, -50.8) * mm, "mid": v(-11.43, -49.5) * mm, "end": v(-22.27, -45.66) * mm});
            skArc(sketch, "E137.9.54", {"start": v(0, -47.4) * mm, "mid": v(-4.54, -47.18) * mm, "end": v(-9.04, -46.53) * mm});
            skArc(sketch, "E137.9.55", {"start": v(0, -44) * mm, "mid": v(-9.9, -42.87) * mm, "end": v(-19.29, -39.55) * mm});
            skArc(sketch, "E137.9.56", {"start": v(0, -68.2) * mm, "mid": v(8.9, -67.62) * mm, "end": v(17.65, -65.88) * mm});
            skArc(sketch, "E137.9.57", {"start": v(0, -88.2) * mm, "mid": v(-8.45, -87.8) * mm, "end": v(-16.83, -86.58) * mm});
            skArc(sketch, "E137.9.58", {"start": v(0, -74.6) * mm, "mid": v(-7.15, -74.26) * mm, "end": v(-14.23, -73.23) * mm});
            skLineSegment(sketch, "E137.9.59", {"start": v(-40.33, -82.69) * mm, "end": v(-40.15, -82.33) * mm});
            skArc(sketch, "E137.9.60", {"start": v(0, -75) * mm, "mid": v(9.79, -74.36) * mm, "end": v(19.41, -72.44) * mm});
            skArc(sketch, "E137.9.61", {"start": v(0, -74.6) * mm, "mid": v(9.74, -73.96) * mm, "end": v(19.3, -72.06) * mm});
            skArc(sketch, "E137.9.62", {"start": v(0, -88.2) * mm, "mid": v(11.51, -87.45) * mm, "end": v(22.83, -85.2) * mm});
            skArc(sketch, "E137.9.63", {"start": v(0, -7) * mm, "mid": v(-0.67, -6.97) * mm, "end": v(-1.34, -6.87) * mm});
            skArc(sketch, "E137.9.64", {"start": v(0, -41) * mm, "mid": v(-3.93, -40.81) * mm, "end": v(-7.82, -40.25) * mm});
            skArc(sketch, "E137.9.65", {"start": v(0, -67.8) * mm, "mid": v(8.85, -67.22) * mm, "end": v(17.55, -65.49) * mm});
            skArc(sketch, "E137.9.66", {"start": v(0, -54.6) * mm, "mid": v(-5.23, -54.35) * mm, "end": v(-10.42, -53.6) * mm});
            skArc(sketch, "E137.9.67", {"start": v(0, -20.6) * mm, "mid": v(-1.97, -20.5) * mm, "end": v(-3.93, -20.22) * mm});
            skArc(sketch, "E137.9.68", {"start": v(0, -13.8) * mm, "mid": v(-1.32, -13.74) * mm, "end": v(-2.63, -13.55) * mm});
            skArc(sketch, "E137.9.69", {"start": v(0, -24) * mm, "mid": v(-5.4, -23.38) * mm, "end": v(-10.52, -21.57) * mm});
            skArc(sketch, "E137.9.70", {"start": v(0, -30.4) * mm, "mid": v(-6.84, -29.62) * mm, "end": v(-13.33, -27.32) * mm});
            skArc(sketch, "E137.9.71", {"start": v(0, -61.4) * mm, "mid": v(8.01, -60.87) * mm, "end": v(15.9, -59.3) * mm});
            skArc(sketch, "E137.9.72", {"start": v(1.7, -6.38) * mm, "mid": v(0.23, -6.6) * mm, "end": v(-1.26, -6.48) * mm});
            skArc(sketch, "E137.9.73", {"start": v(0, -61) * mm, "mid": v(7.96, -60.48) * mm, "end": v(15.79, -58.92) * mm});
            skArc(sketch, "E137.9.74", {"start": v(0, -47.4) * mm, "mid": v(6.19, -47) * mm, "end": v(12.27, -45.78) * mm});
            skArc(sketch, "E137.9.75", {"start": v(0, -34.2) * mm, "mid": v(4.46, -33.9) * mm, "end": v(8.85, -33.03) * mm});
            skArc(sketch, "E137.9.76", {"start": v(0, -40.6) * mm, "mid": v(-3.9, -40.41) * mm, "end": v(-7.75, -39.85) * mm});
            skArc(sketch, "E137.9.77", {"start": v(0, -71.2) * mm, "mid": v(-16.02, -69.38) * mm, "end": v(-31.21, -64) * mm});
            skArc(sketch, "E137.10.0", {"start": v(-10.3, -17.84) * mm, "mid": v(-7.88, -19.03) * mm, "end": v(-5.33, -19.9) * mm});
            skArc(sketch, "E137.10.1", {"start": v(-8.6, -14.9) * mm, "mid": v(-11.73, -12.58) * mm, "end": v(-14.26, -9.62) * mm});
            skArc(sketch, "E137.10.2", {"start": v(-10.1, -17.5) * mm, "mid": v(-7.73, -18.66) * mm, "end": v(-5.23, -19.51) * mm});
            skArc(sketch, "E137.10.3", {"start": v(-32.2, -55.77) * mm, "mid": v(-43.92, -47.1) * mm, "end": v(-53.4, -36.01) * mm});
            skArc(sketch, "E137.10.4", {"start": v(-40.7, -70.5) * mm, "mid": v(-31.15, -75.2) * mm, "end": v(-21.07, -78.63) * mm});
            skArc(sketch, "E137.10.5", {"start": v(-10.1, -17.5) * mm, "mid": v(-11.73, -16.45) * mm, "end": v(-13.25, -15.25) * mm});
            skArc(sketch, "E137.10.6", {"start": v(-39.2, -67.9) * mm, "mid": v(-53.47, -57.34) * mm, "end": v(-65, -43.84) * mm});
            skArc(sketch, "E137.10.7", {"start": v(-5.2, -9) * mm, "mid": v(-7.1, -7.6) * mm, "end": v(-8.62, -5.82) * mm});
            skArc(sketch, "E137.10.8", {"start": v(-18.8, -32.56) * mm, "mid": v(-25.64, -27.5) * mm, "end": v(-31.17, -21.03) * mm});
            skArc(sketch, "E137.10.9", {"start": v(-46, -79.67) * mm, "mid": v(-62.74, -67.28) * mm, "end": v(-76.27, -51.45) * mm});
            skArc(sketch, "E137.10.10", {"start": v(-13.7, -23.73) * mm, "mid": v(-15.91, -22.3) * mm, "end": v(-17.98, -20.68) * mm});
            skArc(sketch, "E137.10.11", {"start": v(-13.7, -23.73) * mm, "mid": v(-10.49, -25.31) * mm, "end": v(-7.1, -26.47) * mm});
            skArc(sketch, "E137.10.12", {"start": v(-44.3, -76.73) * mm, "mid": v(-33.9, -81.86) * mm, "end": v(-22.93, -85.58) * mm});
            skArc(sketch, "E137.10.13", {"start": v(-42.6, -73.79) * mm, "mid": v(-58.1, -62.31) * mm, "end": v(-70.63, -47.64) * mm});
            skArc(sketch, "E137.10.14", {"start": v(-27.3, -47.28) * mm, "mid": v(-20.9, -50.44) * mm, "end": v(-14.13, -52.74) * mm});
            skArc(sketch, "E137.10.15", {"start": v(-27.1, -46.94) * mm, "mid": v(-20.74, -50.07) * mm, "end": v(-14.03, -52.35) * mm});
            skArc(sketch, "E137.10.16", {"start": v(-45.8, -79.33) * mm, "mid": v(-62.47, -67) * mm, "end": v(-75.94, -51.22) * mm});
            skArc(sketch, "E137.10.17", {"start": v(-40.7, -70.5) * mm, "mid": v(-47.27, -66.27) * mm, "end": v(-53.4, -61.43) * mm});
            skArc(sketch, "E137.10.18", {"start": v(-15.4, -26.67) * mm, "mid": v(-21, -22.53) * mm, "end": v(-25.53, -17.22) * mm});
            skArc(sketch, "E137.10.19", {"start": v(-29, -50.23) * mm, "mid": v(-39.56, -42.42) * mm, "end": v(-48.08, -32.43) * mm});
            skArc(sketch, "E137.10.20", {"start": v(-28.8, -49.88) * mm, "mid": v(-39.28, -42.13) * mm, "end": v(-47.75, -32.2) * mm});
            skArc(sketch, "E137.10.21", {"start": v(-32.4, -56.12) * mm, "mid": v(-44.2, -47.4) * mm, "end": v(-53.72, -36.24) * mm});
            skArc(sketch, "E137.10.22", {"start": v(-20.5, -35.5) * mm, "mid": v(-15.7, -37.88) * mm, "end": v(-10.61, -39.6) * mm});
            skArc(sketch, "E137.10.23", {"start": v(-5, -8.66) * mm, "mid": v(-6.82, -7.31) * mm, "end": v(-8.3, -5.6) * mm});
            skArc(sketch, "E137.10.24", {"start": v(-6.9, -11.95) * mm, "mid": v(-5.28, -12.75) * mm, "end": v(-3.57, -13.33) * mm});
            skArc(sketch, "E137.10.25", {"start": v(-13.5, -23.38) * mm, "mid": v(-15.68, -21.98) * mm, "end": v(-17.71, -20.38) * mm});
            skArc(sketch, "E137.10.26", {"start": v(-16.9, -29.27) * mm, "mid": v(-12.93, -31.23) * mm, "end": v(-8.75, -32.65) * mm});
            skArc(sketch, "E137.10.27", {"start": v(-35.8, -62) * mm, "mid": v(-48.83, -52.36) * mm, "end": v(-59.36, -40.04) * mm});
            skArc(sketch, "E137.10.28", {"start": v(-23.9, -41.4) * mm, "mid": v(-27.76, -38.91) * mm, "end": v(-31.36, -36.08) * mm});
            skArc(sketch, "E137.10.29", {"start": v(-6.7, -11.6) * mm, "mid": v(-5.13, -12.38) * mm, "end": v(-3.47, -12.94) * mm});
            skArc(sketch, "E137.10.30", {"start": v(-27.1, -46.94) * mm, "mid": v(-31.47, -44.13) * mm, "end": v(-35.56, -40.9) * mm});
            skArc(sketch, "E137.10.31", {"start": v(-40.9, -70.84) * mm, "mid": v(-47.5, -66.6) * mm, "end": v(-53.67, -61.74) * mm});
            skArc(sketch, "E137.10.32", {"start": v(-37.5, -64.95) * mm, "mid": v(-43.55, -61.06) * mm, "end": v(-49.2, -56.6) * mm});
            skArc(sketch, "E137.10.33", {"start": v(-17.1, -29.62) * mm, "mid": v(-19.86, -27.84) * mm, "end": v(-22.44, -25.81) * mm});
            skArc(sketch, "E137.10.34", {"start": v(-16.9, -29.27) * mm, "mid": v(-19.63, -27.52) * mm, "end": v(-22.17, -25.5) * mm});
            skArc(sketch, "E137.10.35", {"start": v(-20.3, -35.16) * mm, "mid": v(-15.54, -37.5) * mm, "end": v(-10.5, -39.22) * mm});
            skArc(sketch, "E137.10.36", {"start": v(-42.4, -73.44) * mm, "mid": v(-57.83, -62.02) * mm, "end": v(-70.3, -47.42) * mm});
            skArc(sketch, "E137.10.37", {"start": v(-11.8, -20.44) * mm, "mid": v(-16.1, -17.26) * mm, "end": v(-19.57, -13.2) * mm});
            skArc(sketch, "E137.10.38", {"start": v(-3.5, -6.06) * mm, "mid": v(-2.68, -6.47) * mm, "end": v(-1.81, -6.76) * mm});
            skArc(sketch, "E137.10.39", {"start": v(-40.9, -70.84) * mm, "mid": v(-31.3, -75.57) * mm, "end": v(-21.17, -79.01) * mm});
            skArc(sketch, "E137.10.40", {"start": v(-25.6, -44.34) * mm, "mid": v(-34.92, -37.45) * mm, "end": v(-42.45, -28.63) * mm});
            skArc(sketch, "E137.10.41", {"start": v(-22.2, -38.45) * mm, "mid": v(-30.28, -32.47) * mm, "end": v(-36.8, -24.83) * mm});
            skArc(sketch, "E137.10.42", {"start": v(-30.7, -53.17) * mm, "mid": v(-35.66, -49.99) * mm, "end": v(-40.28, -46.34) * mm});
            skArc(sketch, "E137.10.43", {"start": v(-23.9, -41.4) * mm, "mid": v(-18.3, -44.16) * mm, "end": v(-12.37, -46.17) * mm});
            skArc(sketch, "E137.10.44", {"start": v(-13.5, -23.38) * mm, "mid": v(-10.33, -24.94) * mm, "end": v(-6.99, -26.08) * mm});
            skArc(sketch, "E137.10.45", {"start": v(-6.7, -11.6) * mm, "mid": v(-7.78, -10.9) * mm, "end": v(-8.8, -10.11) * mm});
            skArc(sketch, "E137.10.46", {"start": v(-18.6, -32.22) * mm, "mid": v(-25.37, -27.2) * mm, "end": v(-30.84, -20.8) * mm});
            skArc(sketch, "E137.10.47", {"start": v(-34.1, -59.06) * mm, "mid": v(-39.6, -55.52) * mm, "end": v(-44.74, -51.47) * mm});
            skArc(sketch, "E137.10.48", {"start": v(-30.5, -52.83) * mm, "mid": v(-35.42, -49.66) * mm, "end": v(-40.02, -46.04) * mm});
            skArc(sketch, "E137.10.49", {"start": v(-44.3, -76.73) * mm, "mid": v(-51.45, -72.13) * mm, "end": v(-58.13, -66.87) * mm});
            skArc(sketch, "E137.10.50", {"start": v(-33.9, -58.72) * mm, "mid": v(-39.37, -55.2) * mm, "end": v(-44.48, -51.17) * mm});
            skArc(sketch, "E137.10.51", {"start": v(-39, -67.55) * mm, "mid": v(-53.2, -57.05) * mm, "end": v(-64.66, -43.62) * mm});
            skArc(sketch, "E137.10.52", {"start": v(-8.4, -14.55) * mm, "mid": v(-11.46, -12.29) * mm, "end": v(-13.93, -9.4) * mm});
            skArc(sketch, "E137.10.53", {"start": v(-25.4, -44) * mm, "mid": v(-34.65, -37.15) * mm, "end": v(-42.12, -28.4) * mm});
            skArc(sketch, "E137.10.54", {"start": v(-23.7, -41.05) * mm, "mid": v(-27.53, -38.59) * mm, "end": v(-31.1, -35.77) * mm});
            skArc(sketch, "E137.10.55", {"start": v(-22, -38.1) * mm, "mid": v(-30, -32.18) * mm, "end": v(-36.48, -24.6) * mm});
            skArc(sketch, "E137.10.56", {"start": v(-34.1, -59.06) * mm, "mid": v(-26.1, -63) * mm, "end": v(-17.65, -65.88) * mm});
            skArc(sketch, "E137.10.57", {"start": v(-44.1, -76.38) * mm, "mid": v(-51.22, -71.8) * mm, "end": v(-57.86, -66.57) * mm});
            skArc(sketch, "E137.10.58", {"start": v(-37.3, -64.6) * mm, "mid": v(-43.32, -60.73) * mm, "end": v(-48.94, -56.3) * mm});
            skLineSegment(sketch, "E137.10.59", {"start": v(-76.27, -51.45) * mm, "end": v(-75.94, -51.22) * mm});
            skArc(sketch, "E137.10.60", {"start": v(-37.5, -64.95) * mm, "mid": v(-28.7, -69.3) * mm, "end": v(-19.41, -72.44) * mm});
            skArc(sketch, "E137.10.61", {"start": v(-37.3, -64.6) * mm, "mid": v(-28.55, -68.92) * mm, "end": v(-19.3, -72.06) * mm});
            skArc(sketch, "E137.10.62", {"start": v(-44.1, -76.38) * mm, "mid": v(-33.75, -81.49) * mm, "end": v(-22.83, -85.2) * mm});
            skArc(sketch, "E137.10.63", {"start": v(-3.5, -6.06) * mm, "mid": v(-4.06, -5.7) * mm, "end": v(-4.6, -5.28) * mm});
            skArc(sketch, "E137.10.64", {"start": v(-20.5, -35.5) * mm, "mid": v(-23.8, -33.38) * mm, "end": v(-26.9, -30.94) * mm});
            skArc(sketch, "E137.10.65", {"start": v(-33.9, -58.72) * mm, "mid": v(-25.95, -62.64) * mm, "end": v(-17.55, -65.49) * mm});
            skArc(sketch, "E137.10.66", {"start": v(-27.3, -47.28) * mm, "mid": v(-31.7, -44.45) * mm, "end": v(-35.82, -41.2) * mm});
            skArc(sketch, "E137.10.67", {"start": v(-10.3, -17.84) * mm, "mid": v(-11.96, -16.77) * mm, "end": v(-13.51, -15.55) * mm});
            skArc(sketch, "E137.10.68", {"start": v(-6.9, -11.95) * mm, "mid": v(-8.01, -11.23) * mm, "end": v(-9.05, -10.41) * mm});
            skArc(sketch, "E137.10.69", {"start": v(-12, -20.78) * mm, "mid": v(-16.37, -17.55) * mm, "end": v(-19.9, -13.42) * mm});
            skArc(sketch, "E137.10.70", {"start": v(-15.2, -26.33) * mm, "mid": v(-20.73, -22.23) * mm, "end": v(-25.2, -17) * mm});
            skArc(sketch, "E137.10.71", {"start": v(-30.7, -53.17) * mm, "mid": v(-23.5, -56.73) * mm, "end": v(-15.9, -59.3) * mm});
            skArc(sketch, "E137.10.72", {"start": v(-1.7, -6.38) * mm, "mid": v(-3.1, -5.83) * mm, "end": v(-4.33, -4.98) * mm});
            skArc(sketch, "E137.10.73", {"start": v(-30.5, -52.83) * mm, "mid": v(-23.34, -56.36) * mm, "end": v(-15.79, -58.92) * mm});
            skArc(sketch, "E137.10.74", {"start": v(-23.7, -41.05) * mm, "mid": v(-18.14, -43.8) * mm, "end": v(-12.27, -45.78) * mm});
            skArc(sketch, "E137.10.75", {"start": v(-17.1, -29.62) * mm, "mid": v(-13.09, -31.6) * mm, "end": v(-8.85, -33.03) * mm});
            skArc(sketch, "E137.10.76", {"start": v(-20.3, -35.16) * mm, "mid": v(-23.58, -33.05) * mm, "end": v(-26.64, -30.64) * mm});
            skArc(sketch, "E137.10.77", {"start": v(-35.6, -61.66) * mm, "mid": v(-48.56, -52.07) * mm, "end": v(-59.03, -39.81) * mm});
            skArc(sketch, "E137.11.0", {"start": v(-17.84, -10.3) * mm, "mid": v(-16.34, -12.54) * mm, "end": v(-14.57, -14.57) * mm});
            skArc(sketch, "E137.11.1", {"start": v(-14.9, -8.6) * mm, "mid": v(-16.45, -5.03) * mm, "end": v(-17.16, -1.2) * mm});
            skArc(sketch, "E137.11.2", {"start": v(-17.5, -10.1) * mm, "mid": v(-16.03, -12.3) * mm, "end": v(-14.28, -14.28) * mm});
            skArc(sketch, "E137.11.3", {"start": v(-55.77, -32.2) * mm, "mid": v(-61.59, -18.83) * mm, "end": v(-64.24, -4.5) * mm});
            skArc(sketch, "E137.11.4", {"start": v(-70.5, -40.7) * mm, "mid": v(-64.58, -49.55) * mm, "end": v(-57.56, -57.56) * mm});
            skArc(sketch, "E137.11.5", {"start": v(-17.5, -10.1) * mm, "mid": v(-18.38, -8.38) * mm, "end": v(-19.1, -6.58) * mm});
            skArc(sketch, "E137.11.6", {"start": v(-67.9, -39.2) * mm, "mid": v(-74.97, -22.92) * mm, "end": v(-78.2, -5.47) * mm});
            skArc(sketch, "E137.11.7", {"start": v(-9, -5.2) * mm, "mid": v(-9.95, -3.04) * mm, "end": v(-10.37, -0.73) * mm});
            skArc(sketch, "E137.11.8", {"start": v(-32.56, -18.8) * mm, "mid": v(-35.96, -11) * mm, "end": v(-37.5, -2.62) * mm});
            skArc(sketch, "E137.11.9", {"start": v(-79.67, -46) * mm, "mid": v(-87.98, -26.9) * mm, "end": v(-91.78, -6.42) * mm});
            skArc(sketch, "E137.11.10", {"start": v(-23.73, -13.7) * mm, "mid": v(-24.93, -11.36) * mm, "end": v(-25.9, -8.92) * mm});
            skArc(sketch, "E137.11.11", {"start": v(-23.73, -13.7) * mm, "mid": v(-21.74, -16.68) * mm, "end": v(-19.37, -19.37) * mm});
            skArc(sketch, "E137.11.12", {"start": v(-76.73, -44.3) * mm, "mid": v(-70.3, -53.94) * mm, "end": v(-62.65, -62.65) * mm});
            skArc(sketch, "E137.11.13", {"start": v(-73.79, -42.6) * mm, "mid": v(-81.48, -24.91) * mm, "end": v(-85, -5.94) * mm});
            skArc(sketch, "E137.11.14", {"start": v(-47.28, -27.3) * mm, "mid": v(-43.32, -33.24) * mm, "end": v(-38.6, -38.6) * mm});
            skArc(sketch, "E137.11.15", {"start": v(-46.94, -27.1) * mm, "mid": v(-43, -33) * mm, "end": v(-38.33, -38.33) * mm});
            skArc(sketch, "E137.11.16", {"start": v(-79.33, -45.8) * mm, "mid": v(-87.6, -26.78) * mm, "end": v(-91.38, -6.39) * mm});
            skArc(sketch, "E137.11.17", {"start": v(-70.5, -40.7) * mm, "mid": v(-74.07, -33.76) * mm, "end": v(-76.97, -26.5) * mm});
            skArc(sketch, "E137.11.18", {"start": v(-26.67, -15.4) * mm, "mid": v(-29.45, -9) * mm, "end": v(-30.72, -2.15) * mm});
            skArc(sketch, "E137.11.19", {"start": v(-50.23, -29) * mm, "mid": v(-55.47, -16.96) * mm, "end": v(-57.86, -4.05) * mm});
            skArc(sketch, "E137.11.20", {"start": v(-49.88, -28.8) * mm, "mid": v(-55.08, -16.84) * mm, "end": v(-57.46, -4.02) * mm});
            skArc(sketch, "E137.11.21", {"start": v(-56.12, -32.4) * mm, "mid": v(-61.97, -18.95) * mm, "end": v(-64.64, -4.52) * mm});
            skArc(sketch, "E137.11.22", {"start": v(-35.5, -20.5) * mm, "mid": v(-32.53, -24.96) * mm, "end": v(-29, -29) * mm});
            skArc(sketch, "E137.11.23", {"start": v(-8.66, -5) * mm, "mid": v(-9.56, -2.92) * mm, "end": v(-9.98, -0.7) * mm});
            skArc(sketch, "E137.11.24", {"start": v(-11.95, -6.9) * mm, "mid": v(-10.95, -8.4) * mm, "end": v(-9.76, -9.76) * mm});
            skArc(sketch, "E137.11.25", {"start": v(-23.38, -13.5) * mm, "mid": v(-24.57, -11.2) * mm, "end": v(-25.53, -8.8) * mm});
            skArc(sketch, "E137.11.26", {"start": v(-29.27, -16.9) * mm, "mid": v(-26.82, -20.58) * mm, "end": v(-23.9, -23.9) * mm});
            skArc(sketch, "E137.11.27", {"start": v(-62, -35.8) * mm, "mid": v(-68.47, -20.93) * mm, "end": v(-71.43, -5) * mm});
            skArc(sketch, "E137.11.28", {"start": v(-41.4, -23.9) * mm, "mid": v(-43.5, -19.82) * mm, "end": v(-45.2, -15.56) * mm});
            skArc(sketch, "E137.11.29", {"start": v(-11.6, -6.7) * mm, "mid": v(-10.63, -8.16) * mm, "end": v(-9.48, -9.48) * mm});
            skArc(sketch, "E137.11.30", {"start": v(-46.94, -27.1) * mm, "mid": v(-49.32, -22.48) * mm, "end": v(-51.25, -17.65) * mm});
            skArc(sketch, "E137.11.31", {"start": v(-70.84, -40.9) * mm, "mid": v(-74.43, -33.92) * mm, "end": v(-77.34, -26.63) * mm});
            skArc(sketch, "E137.11.32", {"start": v(-64.95, -37.5) * mm, "mid": v(-68.25, -31.1) * mm, "end": v(-70.91, -24.42) * mm});
            skArc(sketch, "E137.11.33", {"start": v(-29.62, -17.1) * mm, "mid": v(-31.12, -14.18) * mm, "end": v(-32.34, -11.13) * mm});
            skArc(sketch, "E137.11.34", {"start": v(-29.27, -16.9) * mm, "mid": v(-30.76, -14.02) * mm, "end": v(-31.96, -11) * mm});
            skArc(sketch, "E137.11.35", {"start": v(-35.16, -20.3) * mm, "mid": v(-32.21, -24.72) * mm, "end": v(-28.7, -28.7) * mm});
            skArc(sketch, "E137.11.36", {"start": v(-73.44, -42.4) * mm, "mid": v(-81.1, -24.8) * mm, "end": v(-84.6, -5.92) * mm});
            skArc(sketch, "E137.11.37", {"start": v(-20.44, -11.8) * mm, "mid": v(-22.57, -6.9) * mm, "end": v(-23.54, -1.65) * mm});
            skArc(sketch, "E137.11.38", {"start": v(-6.06, -3.5) * mm, "mid": v(-5.55, -4.26) * mm, "end": v(-4.95, -4.95) * mm});
            skArc(sketch, "E137.11.39", {"start": v(-70.84, -40.9) * mm, "mid": v(-64.9, -49.8) * mm, "end": v(-57.84, -57.84) * mm});
            skArc(sketch, "E137.11.40", {"start": v(-44.34, -25.6) * mm, "mid": v(-48.96, -14.97) * mm, "end": v(-51.08, -3.57) * mm});
            skArc(sketch, "E137.11.41", {"start": v(-38.45, -22.2) * mm, "mid": v(-42.46, -12.98) * mm, "end": v(-44.3, -3.1) * mm});
            skArc(sketch, "E137.11.42", {"start": v(-53.17, -30.7) * mm, "mid": v(-55.87, -25.46) * mm, "end": v(-58.05, -19.99) * mm});
            skArc(sketch, "E137.11.43", {"start": v(-41.4, -23.9) * mm, "mid": v(-37.92, -29.1) * mm, "end": v(-33.8, -33.8) * mm});
            skArc(sketch, "E137.11.44", {"start": v(-23.38, -13.5) * mm, "mid": v(-21.42, -16.44) * mm, "end": v(-19.1, -19.1) * mm});
            skArc(sketch, "E137.11.45", {"start": v(-11.6, -6.7) * mm, "mid": v(-12.2, -5.56) * mm, "end": v(-12.67, -4.36) * mm});
            skArc(sketch, "E137.11.46", {"start": v(-32.22, -18.6) * mm, "mid": v(-35.57, -10.88) * mm, "end": v(-37.1, -2.6) * mm});
            skArc(sketch, "E137.11.47", {"start": v(-59.06, -34.1) * mm, "mid": v(-62.06, -28.28) * mm, "end": v(-64.48, -22.2) * mm});
            skArc(sketch, "E137.11.48", {"start": v(-52.83, -30.5) * mm, "mid": v(-55.5, -25.3) * mm, "end": v(-57.68, -19.86) * mm});
            skArc(sketch, "E137.11.49", {"start": v(-76.73, -44.3) * mm, "mid": v(-80.62, -36.74) * mm, "end": v(-83.77, -28.85) * mm});
            skArc(sketch, "E137.11.50", {"start": v(-58.72, -33.9) * mm, "mid": v(-61.7, -28.12) * mm, "end": v(-64.1, -22.07) * mm});
            skArc(sketch, "E137.11.51", {"start": v(-67.55, -39) * mm, "mid": v(-74.6, -22.8) * mm, "end": v(-77.8, -5.44) * mm});
            skArc(sketch, "E137.11.52", {"start": v(-14.55, -8.4) * mm, "mid": v(-16.07, -4.91) * mm, "end": v(-16.76, -1.17) * mm});
            skArc(sketch, "E137.11.53", {"start": v(-44, -25.4) * mm, "mid": v(-48.58, -14.85) * mm, "end": v(-50.68, -3.54) * mm});
            skArc(sketch, "E137.11.54", {"start": v(-41.05, -23.7) * mm, "mid": v(-43.13, -19.66) * mm, "end": v(-44.82, -15.43) * mm});
            skArc(sketch, "E137.11.55", {"start": v(-38.1, -22) * mm, "mid": v(-42.08, -12.86) * mm, "end": v(-43.9, -3.07) * mm});
            skArc(sketch, "E137.11.56", {"start": v(-59.06, -34.1) * mm, "mid": v(-54.1, -41.52) * mm, "end": v(-48.22, -48.22) * mm});
            skArc(sketch, "E137.11.57", {"start": v(-76.38, -44.1) * mm, "mid": v(-80.26, -36.58) * mm, "end": v(-83.4, -28.72) * mm});
            skArc(sketch, "E137.11.58", {"start": v(-64.6, -37.3) * mm, "mid": v(-67.88, -30.94) * mm, "end": v(-70.54, -24.29) * mm});
            skLineSegment(sketch, "E137.11.59", {"start": v(-91.78, -6.42) * mm, "end": v(-91.38, -6.39) * mm});
            skArc(sketch, "E137.11.60", {"start": v(-64.95, -37.5) * mm, "mid": v(-59.5, -45.66) * mm, "end": v(-53.03, -53.03) * mm});
            skArc(sketch, "E137.11.61", {"start": v(-64.6, -37.3) * mm, "mid": v(-59.18, -45.41) * mm, "end": v(-52.75, -52.75) * mm});
            skArc(sketch, "E137.11.62", {"start": v(-76.38, -44.1) * mm, "mid": v(-69.97, -53.7) * mm, "end": v(-62.37, -62.37) * mm});
            skArc(sketch, "E137.11.63", {"start": v(-6.06, -3.5) * mm, "mid": v(-6.37, -2.9) * mm, "end": v(-6.62, -2.28) * mm});
            skArc(sketch, "E137.11.64", {"start": v(-35.5, -20.5) * mm, "mid": v(-37.3, -17) * mm, "end": v(-38.77, -13.35) * mm});
            skArc(sketch, "E137.11.65", {"start": v(-58.72, -33.9) * mm, "mid": v(-53.79, -41.27) * mm, "end": v(-47.94, -47.94) * mm});
            skArc(sketch, "E137.11.66", {"start": v(-47.28, -27.3) * mm, "mid": v(-49.68, -22.64) * mm, "end": v(-51.63, -17.78) * mm});
            skArc(sketch, "E137.11.67", {"start": v(-17.84, -10.3) * mm, "mid": v(-18.75, -8.54) * mm, "end": v(-19.48, -6.7) * mm});
            skArc(sketch, "E137.11.68", {"start": v(-11.95, -6.9) * mm, "mid": v(-12.56, -5.72) * mm, "end": v(-13.05, -4.5) * mm});
            skArc(sketch, "E137.11.69", {"start": v(-20.78, -12) * mm, "mid": v(-22.95, -7.02) * mm, "end": v(-23.94, -1.67) * mm});
            skArc(sketch, "E137.11.70", {"start": v(-26.33, -15.2) * mm, "mid": v(-29.07, -8.89) * mm, "end": v(-30.33, -2.12) * mm});
            skArc(sketch, "E137.11.71", {"start": v(-53.17, -30.7) * mm, "mid": v(-48.71, -37.38) * mm, "end": v(-43.42, -43.42) * mm});
            skArc(sketch, "E137.11.72", {"start": v(-4.67, -4.67) * mm, "mid": v(-5.6, -3.5) * mm, "end": v(-6.24, -2.15) * mm});
            skArc(sketch, "E137.11.73", {"start": v(-52.83, -30.5) * mm, "mid": v(-48.4, -37.13) * mm, "end": v(-43.13, -43.13) * mm});
            skArc(sketch, "E137.11.74", {"start": v(-41.05, -23.7) * mm, "mid": v(-37.6, -28.86) * mm, "end": v(-33.52, -33.52) * mm});
            skArc(sketch, "E137.11.75", {"start": v(-29.62, -17.1) * mm, "mid": v(-27.13, -20.82) * mm, "end": v(-24.18, -24.18) * mm});
            skArc(sketch, "E137.11.76", {"start": v(-35.16, -20.3) * mm, "mid": v(-36.94, -16.84) * mm, "end": v(-38.39, -13.22) * mm});
            skArc(sketch, "E137.11.77", {"start": v(-61.66, -35.6) * mm, "mid": v(-68.09, -20.82) * mm, "end": v(-71.03, -4.97) * mm});
            skLineSegment(sketch, "E137.anchor1", {"start": v(0, 0) * mm, "end": v(-92, 0) * mm, "construction": true});
            skLineSegment(sketch, "E137.anchor2", {"start": v(0, 0) * mm, "end": v(-79.67, -46) * mm, "construction": true});
            skLineSegment(sketch, "E138", {"start": v(-79.67, 46) * mm, "end": v(-79.33, 45.8) * mm});
            skLineSegment(sketch, "E139", {"start": v(-73.79, 42.6) * mm, "end": v(-73.44, 42.4) * mm});
            skLineSegment(sketch, "E140", {"start": v(-67.9, 39.2) * mm, "end": v(-67.55, 39) * mm});
            skLineSegment(sketch, "E141", {"start": v(-62, 35.8) * mm, "end": v(-61.66, 35.6) * mm});
            skLineSegment(sketch, "E142", {"start": v(-56.12, 32.4) * mm, "end": v(-55.77, 32.2) * mm});
            skLineSegment(sketch, "E143", {"start": v(-50.23, 29) * mm, "end": v(-49.88, 28.8) * mm});
            skLineSegment(sketch, "E144", {"start": v(-44.34, 25.6) * mm, "end": v(-44, 25.4) * mm});
            skLineSegment(sketch, "E145", {"start": v(-38.45, 22.2) * mm, "end": v(-38.1, 22) * mm});
            skLineSegment(sketch, "E146", {"start": v(-32.56, 18.8) * mm, "end": v(-32.22, 18.6) * mm});
            skLineSegment(sketch, "E147", {"start": v(-26.67, 15.4) * mm, "end": v(-26.33, 15.2) * mm});
            skLineSegment(sketch, "E148", {"start": v(-20.78, 12) * mm, "end": v(-20.44, 11.8) * mm});
            skLineSegment(sketch, "E149", {"start": v(-14.9, 8.6) * mm, "end": v(-14.55, 8.4) * mm});
            skLineSegment(sketch, "E150", {"start": v(-9, 5.2) * mm, "end": v(-8.66, 5) * mm});
            skLineSegment(sketch, "E151", {"start": v(-5.28, 4.6) * mm, "end": v(-4.98, 4.33) * mm});
            skLineSegment(sketch, "E152", {"start": v(-4.95, 4.95) * mm, "end": v(-4.67, 4.67) * mm});
            skLineSegment(sketch, "E153", {"start": v(-10.41, 9.05) * mm, "end": v(-10.11, 8.8) * mm});
            skLineSegment(sketch, "E154", {"start": v(-9.76, 9.76) * mm, "end": v(-9.48, 9.48) * mm});
            skLineSegment(sketch, "E155", {"start": v(-15.55, 13.51) * mm, "end": v(-15.25, 13.25) * mm});
            skLineSegment(sketch, "E156", {"start": v(-14.57, 14.57) * mm, "end": v(-14.28, 14.28) * mm});
            skLineSegment(sketch, "E157", {"start": v(-20.68, 17.98) * mm, "end": v(-20.38, 17.71) * mm});
            skLineSegment(sketch, "E158", {"start": v(-19.37, 19.37) * mm, "end": v(-19.1, 19.1) * mm});
            skLineSegment(sketch, "E159", {"start": v(-25.81, 22.44) * mm, "end": v(-25.5, 22.17) * mm});
            skLineSegment(sketch, "E160", {"start": v(-24.18, 24.18) * mm, "end": v(-23.9, 23.9) * mm});
            skLineSegment(sketch, "E161", {"start": v(-30.94, 26.9) * mm, "end": v(-30.64, 26.64) * mm});
            skLineSegment(sketch, "E162", {"start": v(-29, 29) * mm, "end": v(-28.7, 28.7) * mm});
            skLineSegment(sketch, "E163", {"start": v(-36.08, 31.36) * mm, "end": v(-35.77, 31.1) * mm});
            skLineSegment(sketch, "E164", {"start": v(-33.8, 33.8) * mm, "end": v(-33.52, 33.52) * mm});
            skLineSegment(sketch, "E165", {"start": v(-41.2, 35.82) * mm, "end": v(-40.9, 35.56) * mm});
            skLineSegment(sketch, "E166", {"start": v(-38.6, 38.6) * mm, "end": v(-38.33, 38.33) * mm});
            skLineSegment(sketch, "E167", {"start": v(-46.34, 40.28) * mm, "end": v(-46.04, 40.02) * mm});
            skLineSegment(sketch, "E168", {"start": v(-43.42, 43.42) * mm, "end": v(-43.13, 43.13) * mm});
            skLineSegment(sketch, "E169", {"start": v(-51.47, 44.74) * mm, "end": v(-51.17, 44.48) * mm});
            skLineSegment(sketch, "E170", {"start": v(-48.22, 48.22) * mm, "end": v(-47.94, 47.94) * mm});
            skLineSegment(sketch, "E171", {"start": v(-56.6, 49.2) * mm, "end": v(-56.3, 48.94) * mm});
            skLineSegment(sketch, "E172", {"start": v(-53.03, 53.03) * mm, "end": v(-52.75, 52.75) * mm});
            skLineSegment(sketch, "E173", {"start": v(-61.74, 53.67) * mm, "end": v(-61.43, 53.4) * mm});
            skLineSegment(sketch, "E174", {"start": v(-57.84, 57.84) * mm, "end": v(-57.56, 57.56) * mm});
            skLineSegment(sketch, "E175", {"start": v(-66.87, 58.13) * mm, "end": v(-66.57, 57.86) * mm});
            skLineSegment(sketch, "E176", {"start": v(-62.65, 62.65) * mm, "end": v(-62.37, 62.37) * mm});
            skLineSegment(sketch, "E177.1.0", {"start": v(-29, 50.23) * mm, "end": v(-28.8, 49.88) * mm});
            skLineSegment(sketch, "E177.1.1", {"start": v(-19.99, 58.05) * mm, "end": v(-19.86, 57.68) * mm});
            skLineSegment(sketch, "E177.1.2", {"start": v(-18.8, 32.56) * mm, "end": v(-18.6, 32.22) * mm});
            skLineSegment(sketch, "E177.1.3", {"start": v(-4.5, 13.05) * mm, "end": v(-4.36, 12.67) * mm});
            skLineSegment(sketch, "E177.1.4", {"start": v(-2.28, 6.62) * mm, "end": v(-2.15, 6.24) * mm});
            skLineSegment(sketch, "E177.1.5", {"start": v(-22.2, 64.48) * mm, "end": v(-22.07, 64.1) * mm});
            skLineSegment(sketch, "E177.1.6", {"start": v(-28.85, 83.77) * mm, "end": v(-28.72, 83.4) * mm});
            skLineSegment(sketch, "E177.1.7", {"start": v(-19.41, 72.44) * mm, "end": v(-19.3, 72.06) * mm});
            skLineSegment(sketch, "E177.1.8", {"start": v(-8.92, 25.9) * mm, "end": v(-8.8, 25.53) * mm});
            skLineSegment(sketch, "E177.1.9", {"start": v(-8.85, 33.03) * mm, "end": v(-8.75, 32.65) * mm});
            skLineSegment(sketch, "E177.1.10", {"start": v(-3.57, 13.33) * mm, "end": v(-3.47, 12.94) * mm});
            skLineSegment(sketch, "E177.1.11", {"start": v(-14.13, 52.74) * mm, "end": v(-14.03, 52.35) * mm});
            skLineSegment(sketch, "E177.1.12", {"start": v(-7.1, 26.47) * mm, "end": v(-6.99, 26.08) * mm});
            skLineSegment(sketch, "E177.1.13", {"start": v(-42.6, 73.79) * mm, "end": v(-42.4, 73.44) * mm});
            skLineSegment(sketch, "E177.1.14", {"start": v(-24.42, 70.91) * mm, "end": v(-24.29, 70.54) * mm});
            skLineSegment(sketch, "E177.1.15", {"start": v(-8.6, 14.9) * mm, "end": v(-8.4, 14.55) * mm});
            skLineSegment(sketch, "E177.1.16", {"start": v(-11.13, 32.34) * mm, "end": v(-11, 31.96) * mm});
            skLineSegment(sketch, "E177.1.17", {"start": v(-17.78, 51.63) * mm, "end": v(-17.65, 51.25) * mm});
            skLineSegment(sketch, "E177.1.18", {"start": v(-25.6, 44.34) * mm, "end": v(-25.4, 44) * mm});
            skLineSegment(sketch, "E177.1.19", {"start": v(-13.35, 38.77) * mm, "end": v(-13.22, 38.39) * mm});
            skLineSegment(sketch, "E177.1.20", {"start": v(-21.17, 79.01) * mm, "end": v(-21.07, 78.63) * mm});
            skLineSegment(sketch, "E177.1.21", {"start": v(-15.9, 59.3) * mm, "end": v(-15.79, 58.92) * mm});
            skLineSegment(sketch, "E177.1.22", {"start": v(-1.81, 6.76) * mm, "end": v(-1.7, 6.38) * mm});
            skLineSegment(sketch, "E177.1.23", {"start": v(-5.33, 19.9) * mm, "end": v(-5.23, 19.51) * mm});
            skLineSegment(sketch, "E177.1.24", {"start": v(-35.8, 62) * mm, "end": v(-35.6, 61.66) * mm});
            skLineSegment(sketch, "E177.1.25", {"start": v(-6.7, 19.48) * mm, "end": v(-6.58, 19.1) * mm});
            skLineSegment(sketch, "E177.1.26", {"start": v(-12.37, 46.17) * mm, "end": v(-12.27, 45.78) * mm});
            skLineSegment(sketch, "E177.1.27", {"start": v(-46, 79.67) * mm, "end": v(-45.8, 79.33) * mm});
            skLineSegment(sketch, "E177.1.28", {"start": v(-10.61, 39.6) * mm, "end": v(-10.5, 39.22) * mm});
            skLineSegment(sketch, "E177.1.29", {"start": v(-22.2, 38.45) * mm, "end": v(-22, 38.1) * mm});
            skLineSegment(sketch, "E177.1.30", {"start": v(-32.4, 56.12) * mm, "end": v(-32.2, 55.77) * mm});
            skLineSegment(sketch, "E177.1.31", {"start": v(-17.65, 65.88) * mm, "end": v(-17.55, 65.49) * mm});
            skLineSegment(sketch, "E177.1.32", {"start": v(-22.93, 85.58) * mm, "end": v(-22.83, 85.2) * mm});
            skLineSegment(sketch, "E177.1.33", {"start": v(-15.4, 26.67) * mm, "end": v(-15.2, 26.33) * mm});
            skLineSegment(sketch, "E177.1.34", {"start": v(-39.2, 67.9) * mm, "end": v(-39, 67.55) * mm});
            skLineSegment(sketch, "E177.1.35", {"start": v(-5.2, 9) * mm, "end": v(-5, 8.66) * mm});
            skLineSegment(sketch, "E177.1.36", {"start": v(-26.63, 77.34) * mm, "end": v(-26.5, 76.97) * mm});
            skLineSegment(sketch, "E177.1.37", {"start": v(-15.56, 45.2) * mm, "end": v(-15.43, 44.82) * mm});
            skLineSegment(sketch, "E177.1.38", {"start": v(-12, 20.78) * mm, "end": v(-11.8, 20.44) * mm});
            skLineSegment(sketch, "E177.2.0", {"start": v(0, 58) * mm, "end": v(0, 57.6) * mm});
            skLineSegment(sketch, "E177.2.1", {"start": v(11.72, 60.27) * mm, "end": v(11.64, 59.88) * mm});
            skLineSegment(sketch, "E177.2.2", {"start": v(0, 37.6) * mm, "end": v(0, 37.2) * mm});
            skLineSegment(sketch, "E177.2.3", {"start": v(2.63, 13.55) * mm, "end": v(2.56, 13.15) * mm});
            skLineSegment(sketch, "E177.2.4", {"start": v(1.34, 6.87) * mm, "end": v(1.26, 6.48) * mm});
            skLineSegment(sketch, "E177.2.5", {"start": v(13.01, 66.95) * mm, "end": v(12.94, 66.55) * mm});
            skLineSegment(sketch, "E177.2.6", {"start": v(16.9, 86.97) * mm, "end": v(16.83, 86.58) * mm});
            skLineSegment(sketch, "E177.2.7", {"start": v(19.41, 72.44) * mm, "end": v(19.3, 72.06) * mm});
            skLineSegment(sketch, "E177.2.8", {"start": v(5.23, 26.9) * mm, "end": v(5.15, 26.5) * mm});
            skLineSegment(sketch, "E177.2.9", {"start": v(8.85, 33.03) * mm, "end": v(8.75, 32.65) * mm});
            skLineSegment(sketch, "E177.2.10", {"start": v(3.57, 13.33) * mm, "end": v(3.47, 12.94) * mm});
            skLineSegment(sketch, "E177.2.11", {"start": v(14.13, 52.74) * mm, "end": v(14.03, 52.35) * mm});
            skLineSegment(sketch, "E177.2.12", {"start": v(7.1, 26.47) * mm, "end": v(6.99, 26.08) * mm});
            skLineSegment(sketch, "E177.2.13", {"start": v(0, 85.2) * mm, "end": v(0, 84.8) * mm});
            skLineSegment(sketch, "E177.2.14", {"start": v(14.31, 73.62) * mm, "end": v(14.23, 73.23) * mm});
            skLineSegment(sketch, "E177.2.15", {"start": v(0, 17.2) * mm, "end": v(0, 16.8) * mm});
            skLineSegment(sketch, "E177.2.16", {"start": v(6.53, 33.57) * mm, "end": v(6.45, 33.18) * mm});
            skLineSegment(sketch, "E177.2.17", {"start": v(10.42, 53.6) * mm, "end": v(10.34, 53.2) * mm});
            skLineSegment(sketch, "E177.2.18", {"start": v(0, 51.2) * mm, "end": v(0, 50.8) * mm});
            skLineSegment(sketch, "E177.2.19", {"start": v(7.82, 40.25) * mm, "end": v(7.75, 39.85) * mm});
            skLineSegment(sketch, "E177.2.20", {"start": v(21.17, 79.01) * mm, "end": v(21.07, 78.63) * mm});
            skLineSegment(sketch, "E177.2.21", {"start": v(15.9, 59.3) * mm, "end": v(15.79, 58.92) * mm});
            skLineSegment(sketch, "E177.2.22", {"start": v(1.81, 6.76) * mm, "end": v(1.7, 6.38) * mm});
            skLineSegment(sketch, "E177.2.23", {"start": v(5.33, 19.9) * mm, "end": v(5.23, 19.51) * mm});
            skLineSegment(sketch, "E177.2.24", {"start": v(0, 71.6) * mm, "end": v(0, 71.2) * mm});
            skLineSegment(sketch, "E177.2.25", {"start": v(3.93, 20.22) * mm, "end": v(3.85, 19.83) * mm});
            skLineSegment(sketch, "E177.2.26", {"start": v(12.37, 46.17) * mm, "end": v(12.27, 45.78) * mm});
            skLineSegment(sketch, "E177.2.27", {"start": v(0, 92) * mm, "end": v(0, 91.6) * mm});
            skLineSegment(sketch, "E177.2.28", {"start": v(10.61, 39.6) * mm, "end": v(10.5, 39.22) * mm});
            skLineSegment(sketch, "E177.2.29", {"start": v(0, 44.4) * mm, "end": v(0, 44) * mm});
            skLineSegment(sketch, "E177.2.30", {"start": v(0, 64.8) * mm, "end": v(0, 64.4) * mm});
            skLineSegment(sketch, "E177.2.31", {"start": v(17.65, 65.88) * mm, "end": v(17.55, 65.49) * mm});
            skLineSegment(sketch, "E177.2.32", {"start": v(22.93, 85.58) * mm, "end": v(22.83, 85.2) * mm});
            skLineSegment(sketch, "E177.2.33", {"start": v(0, 30.8) * mm, "end": v(0, 30.4) * mm});
            skLineSegment(sketch, "E177.2.34", {"start": v(0, 78.4) * mm, "end": v(0, 78) * mm});
            skLineSegment(sketch, "E177.2.35", {"start": v(0, 10.4) * mm, "end": v(0, 10) * mm});
            skLineSegment(sketch, "E177.2.36", {"start": v(15.6, 80.3) * mm, "end": v(15.53, 79.9) * mm});
            skLineSegment(sketch, "E177.2.37", {"start": v(9.12, 46.92) * mm, "end": v(9.04, 46.53) * mm});
            skLineSegment(sketch, "E177.2.38", {"start": v(0, 24) * mm, "end": v(0, 23.6) * mm});
            skLineSegment(sketch, "E177.3.0", {"start": v(29, 50.23) * mm, "end": v(28.8, 49.88) * mm});
            skLineSegment(sketch, "E177.3.1", {"start": v(40.28, 46.34) * mm, "end": v(40.02, 46.04) * mm});
            skLineSegment(sketch, "E177.3.2", {"start": v(18.8, 32.56) * mm, "end": v(18.6, 32.22) * mm});
            skLineSegment(sketch, "E177.3.3", {"start": v(9.05, 10.41) * mm, "end": v(8.8, 10.11) * mm});
            skLineSegment(sketch, "E177.3.4", {"start": v(4.6, 5.28) * mm, "end": v(4.33, 4.98) * mm});
            skLineSegment(sketch, "E177.3.5", {"start": v(44.74, 51.47) * mm, "end": v(44.48, 51.17) * mm});
            skLineSegment(sketch, "E177.3.6", {"start": v(58.13, 66.87) * mm, "end": v(57.86, 66.57) * mm});
            skLineSegment(sketch, "E177.3.7", {"start": v(53.03, 53.03) * mm, "end": v(52.75, 52.75) * mm});
            skLineSegment(sketch, "E177.3.8", {"start": v(17.98, 20.68) * mm, "end": v(17.71, 20.38) * mm});
            skLineSegment(sketch, "E177.3.9", {"start": v(24.18, 24.18) * mm, "end": v(23.9, 23.9) * mm});
            skLineSegment(sketch, "E177.3.10", {"start": v(9.76, 9.76) * mm, "end": v(9.48, 9.48) * mm});
            skLineSegment(sketch, "E177.3.11", {"start": v(38.6, 38.6) * mm, "end": v(38.33, 38.33) * mm});
            skLineSegment(sketch, "E177.3.12", {"start": v(19.37, 19.37) * mm, "end": v(19.1, 19.1) * mm});
            skLineSegment(sketch, "E177.3.13", {"start": v(42.6, 73.79) * mm, "end": v(42.4, 73.44) * mm});
            skLineSegment(sketch, "E177.3.14", {"start": v(49.2, 56.6) * mm, "end": v(48.94, 56.3) * mm});
            skLineSegment(sketch, "E177.3.15", {"start": v(8.6, 14.9) * mm, "end": v(8.4, 14.55) * mm});
            skLineSegment(sketch, "E177.3.16", {"start": v(22.44, 25.81) * mm, "end": v(22.17, 25.5) * mm});
            skLineSegment(sketch, "E177.3.17", {"start": v(35.82, 41.2) * mm, "end": v(35.56, 40.9) * mm});
            skLineSegment(sketch, "E177.3.18", {"start": v(25.6, 44.34) * mm, "end": v(25.4, 44) * mm});
            skLineSegment(sketch, "E177.3.19", {"start": v(26.9, 30.94) * mm, "end": v(26.64, 30.64) * mm});
            skLineSegment(sketch, "E177.3.20", {"start": v(57.84, 57.84) * mm, "end": v(57.56, 57.56) * mm});
            skLineSegment(sketch, "E177.3.21", {"start": v(43.42, 43.42) * mm, "end": v(43.13, 43.13) * mm});
            skLineSegment(sketch, "E177.3.22", {"start": v(4.95, 4.95) * mm, "end": v(4.67, 4.67) * mm});
            skLineSegment(sketch, "E177.3.23", {"start": v(14.57, 14.57) * mm, "end": v(14.28, 14.28) * mm});
            skLineSegment(sketch, "E177.3.24", {"start": v(35.8, 62) * mm, "end": v(35.6, 61.66) * mm});
            skLineSegment(sketch, "E177.3.25", {"start": v(13.51, 15.55) * mm, "end": v(13.25, 15.25) * mm});
            skLineSegment(sketch, "E177.3.26", {"start": v(33.8, 33.8) * mm, "end": v(33.52, 33.52) * mm});
            skLineSegment(sketch, "E177.3.27", {"start": v(46, 79.67) * mm, "end": v(45.8, 79.33) * mm});
            skLineSegment(sketch, "E177.3.28", {"start": v(29, 29) * mm, "end": v(28.7, 28.7) * mm});
            skLineSegment(sketch, "E177.3.29", {"start": v(22.2, 38.45) * mm, "end": v(22, 38.1) * mm});
            skLineSegment(sketch, "E177.3.30", {"start": v(32.4, 56.12) * mm, "end": v(32.2, 55.77) * mm});
            skLineSegment(sketch, "E177.3.31", {"start": v(48.22, 48.22) * mm, "end": v(47.94, 47.94) * mm});
            skLineSegment(sketch, "E177.3.32", {"start": v(62.65, 62.65) * mm, "end": v(62.37, 62.37) * mm});
            skLineSegment(sketch, "E177.3.33", {"start": v(15.4, 26.67) * mm, "end": v(15.2, 26.33) * mm});
            skLineSegment(sketch, "E177.3.34", {"start": v(39.2, 67.9) * mm, "end": v(39, 67.55) * mm});
            skLineSegment(sketch, "E177.3.35", {"start": v(5.2, 9) * mm, "end": v(5, 8.66) * mm});
            skLineSegment(sketch, "E177.3.36", {"start": v(53.67, 61.74) * mm, "end": v(53.4, 61.43) * mm});
            skLineSegment(sketch, "E177.3.37", {"start": v(31.36, 36.08) * mm, "end": v(31.1, 35.77) * mm});
            skLineSegment(sketch, "E177.3.38", {"start": v(12, 20.78) * mm, "end": v(11.8, 20.44) * mm});
            skLineSegment(sketch, "E177.4.0", {"start": v(50.23, 29) * mm, "end": v(49.88, 28.8) * mm});
            skLineSegment(sketch, "E177.4.1", {"start": v(58.05, 19.99) * mm, "end": v(57.68, 19.86) * mm});
            skLineSegment(sketch, "E177.4.2", {"start": v(32.56, 18.8) * mm, "end": v(32.22, 18.6) * mm});
            skLineSegment(sketch, "E177.4.3", {"start": v(13.05, 4.5) * mm, "end": v(12.67, 4.36) * mm});
            skLineSegment(sketch, "E177.4.4", {"start": v(6.62, 2.28) * mm, "end": v(6.24, 2.15) * mm});
            skLineSegment(sketch, "E177.4.5", {"start": v(64.48, 22.2) * mm, "end": v(64.1, 22.07) * mm});
            skLineSegment(sketch, "E177.4.6", {"start": v(83.77, 28.85) * mm, "end": v(83.4, 28.72) * mm});
            skLineSegment(sketch, "E177.4.7", {"start": v(72.44, 19.41) * mm, "end": v(72.06, 19.3) * mm});
            skLineSegment(sketch, "E177.4.8", {"start": v(25.9, 8.92) * mm, "end": v(25.53, 8.8) * mm});
            skLineSegment(sketch, "E177.4.9", {"start": v(33.03, 8.85) * mm, "end": v(32.65, 8.75) * mm});
            skLineSegment(sketch, "E177.4.10", {"start": v(13.33, 3.57) * mm, "end": v(12.94, 3.47) * mm});
            skLineSegment(sketch, "E177.4.11", {"start": v(52.74, 14.13) * mm, "end": v(52.35, 14.03) * mm});
            skLineSegment(sketch, "E177.4.12", {"start": v(26.47, 7.1) * mm, "end": v(26.08, 6.99) * mm});
            skLineSegment(sketch, "E177.4.13", {"start": v(73.79, 42.6) * mm, "end": v(73.44, 42.4) * mm});
            skLineSegment(sketch, "E177.4.14", {"start": v(70.91, 24.42) * mm, "end": v(70.54, 24.29) * mm});
            skLineSegment(sketch, "E177.4.15", {"start": v(14.9, 8.6) * mm, "end": v(14.55, 8.4) * mm});
            skLineSegment(sketch, "E177.4.16", {"start": v(32.34, 11.13) * mm, "end": v(31.96, 11) * mm});
            skLineSegment(sketch, "E177.4.17", {"start": v(51.63, 17.78) * mm, "end": v(51.25, 17.65) * mm});
            skLineSegment(sketch, "E177.4.18", {"start": v(44.34, 25.6) * mm, "end": v(44, 25.4) * mm});
            skLineSegment(sketch, "E177.4.19", {"start": v(38.77, 13.35) * mm, "end": v(38.39, 13.22) * mm});
            skLineSegment(sketch, "E177.4.20", {"start": v(79.01, 21.17) * mm, "end": v(78.63, 21.07) * mm});
            skLineSegment(sketch, "E177.4.21", {"start": v(59.3, 15.9) * mm, "end": v(58.92, 15.79) * mm});
            skLineSegment(sketch, "E177.4.22", {"start": v(6.76, 1.81) * mm, "end": v(6.38, 1.7) * mm});
            skLineSegment(sketch, "E177.4.23", {"start": v(19.9, 5.33) * mm, "end": v(19.51, 5.23) * mm});
            skLineSegment(sketch, "E177.4.24", {"start": v(62, 35.8) * mm, "end": v(61.66, 35.6) * mm});
            skLineSegment(sketch, "E177.4.25", {"start": v(19.48, 6.7) * mm, "end": v(19.1, 6.58) * mm});
            skLineSegment(sketch, "E177.4.26", {"start": v(46.17, 12.37) * mm, "end": v(45.78, 12.27) * mm});
            skLineSegment(sketch, "E177.4.27", {"start": v(79.67, 46) * mm, "end": v(79.33, 45.8) * mm});
            skLineSegment(sketch, "E177.4.28", {"start": v(39.6, 10.61) * mm, "end": v(39.22, 10.5) * mm});
            skLineSegment(sketch, "E177.4.29", {"start": v(38.45, 22.2) * mm, "end": v(38.1, 22) * mm});
            skLineSegment(sketch, "E177.4.30", {"start": v(56.12, 32.4) * mm, "end": v(55.77, 32.2) * mm});
            skLineSegment(sketch, "E177.4.31", {"start": v(65.88, 17.65) * mm, "end": v(65.49, 17.55) * mm});
            skLineSegment(sketch, "E177.4.32", {"start": v(85.58, 22.93) * mm, "end": v(85.2, 22.83) * mm});
            skLineSegment(sketch, "E177.4.33", {"start": v(26.67, 15.4) * mm, "end": v(26.33, 15.2) * mm});
            skLineSegment(sketch, "E177.4.34", {"start": v(67.9, 39.2) * mm, "end": v(67.55, 39) * mm});
            skLineSegment(sketch, "E177.4.35", {"start": v(9, 5.2) * mm, "end": v(8.66, 5) * mm});
            skLineSegment(sketch, "E177.4.36", {"start": v(77.34, 26.63) * mm, "end": v(76.97, 26.5) * mm});
            skLineSegment(sketch, "E177.4.37", {"start": v(45.2, 15.56) * mm, "end": v(44.82, 15.43) * mm});
            skLineSegment(sketch, "E177.4.38", {"start": v(20.78, 12) * mm, "end": v(20.44, 11.8) * mm});
            skLineSegment(sketch, "E177.5.0", {"start": v(58, 0) * mm, "end": v(57.6, 0) * mm});
            skLineSegment(sketch, "E177.5.1", {"start": v(60.27, -11.72) * mm, "end": v(59.88, -11.64) * mm});
            skLineSegment(sketch, "E177.5.2", {"start": v(37.6, 0) * mm, "end": v(37.2, 0) * mm});
            skLineSegment(sketch, "E177.5.3", {"start": v(13.55, -2.63) * mm, "end": v(13.15, -2.56) * mm});
            skLineSegment(sketch, "E177.5.4", {"start": v(6.87, -1.34) * mm, "end": v(6.48, -1.26) * mm});
            skLineSegment(sketch, "E177.5.5", {"start": v(66.95, -13.01) * mm, "end": v(66.55, -12.94) * mm});
            skLineSegment(sketch, "E177.5.6", {"start": v(86.97, -16.9) * mm, "end": v(86.58, -16.83) * mm});
            skLineSegment(sketch, "E177.5.7", {"start": v(72.44, -19.41) * mm, "end": v(72.06, -19.3) * mm});
            skLineSegment(sketch, "E177.5.8", {"start": v(26.9, -5.23) * mm, "end": v(26.5, -5.15) * mm});
            skLineSegment(sketch, "E177.5.9", {"start": v(33.03, -8.85) * mm, "end": v(32.65, -8.75) * mm});
            skLineSegment(sketch, "E177.5.10", {"start": v(13.33, -3.57) * mm, "end": v(12.94, -3.47) * mm});
            skLineSegment(sketch, "E177.5.11", {"start": v(52.74, -14.13) * mm, "end": v(52.35, -14.03) * mm});
            skLineSegment(sketch, "E177.5.12", {"start": v(26.47, -7.1) * mm, "end": v(26.08, -6.99) * mm});
            skLineSegment(sketch, "E177.5.13", {"start": v(85.2, 0) * mm, "end": v(84.8, 0) * mm});
            skLineSegment(sketch, "E177.5.14", {"start": v(73.62, -14.31) * mm, "end": v(73.23, -14.23) * mm});
            skLineSegment(sketch, "E177.5.15", {"start": v(17.2, 0) * mm, "end": v(16.8, 0) * mm});
            skLineSegment(sketch, "E177.5.16", {"start": v(33.57, -6.53) * mm, "end": v(33.18, -6.45) * mm});
            skLineSegment(sketch, "E177.5.17", {"start": v(53.6, -10.42) * mm, "end": v(53.2, -10.34) * mm});
            skLineSegment(sketch, "E177.5.18", {"start": v(51.2, 0) * mm, "end": v(50.8, 0) * mm});
            skLineSegment(sketch, "E177.5.19", {"start": v(40.25, -7.82) * mm, "end": v(39.85, -7.75) * mm});
            skLineSegment(sketch, "E177.5.20", {"start": v(79.01, -21.17) * mm, "end": v(78.63, -21.07) * mm});
            skLineSegment(sketch, "E177.5.21", {"start": v(59.3, -15.9) * mm, "end": v(58.92, -15.79) * mm});
            skLineSegment(sketch, "E177.5.22", {"start": v(6.76, -1.81) * mm, "end": v(6.38, -1.7) * mm});
            skLineSegment(sketch, "E177.5.23", {"start": v(19.9, -5.33) * mm, "end": v(19.51, -5.23) * mm});
            skLineSegment(sketch, "E177.5.24", {"start": v(71.6, 0) * mm, "end": v(71.2, 0) * mm});
            skLineSegment(sketch, "E177.5.25", {"start": v(20.22, -3.93) * mm, "end": v(19.83, -3.85) * mm});
            skLineSegment(sketch, "E177.5.26", {"start": v(46.17, -12.37) * mm, "end": v(45.78, -12.27) * mm});
            skLineSegment(sketch, "E177.5.27", {"start": v(92, 0) * mm, "end": v(91.6, 0) * mm});
            skLineSegment(sketch, "E177.5.28", {"start": v(39.6, -10.61) * mm, "end": v(39.22, -10.5) * mm});
            skLineSegment(sketch, "E177.5.29", {"start": v(44.4, 0) * mm, "end": v(44, 0) * mm});
            skLineSegment(sketch, "E177.5.30", {"start": v(64.8, 0) * mm, "end": v(64.4, 0) * mm});
            skLineSegment(sketch, "E177.5.31", {"start": v(65.88, -17.65) * mm, "end": v(65.49, -17.55) * mm});
            skLineSegment(sketch, "E177.5.32", {"start": v(85.58, -22.93) * mm, "end": v(85.2, -22.83) * mm});
            skLineSegment(sketch, "E177.5.33", {"start": v(30.8, 0) * mm, "end": v(30.4, 0) * mm});
            skLineSegment(sketch, "E177.5.34", {"start": v(78.4, 0) * mm, "end": v(78, 0) * mm});
            skLineSegment(sketch, "E177.5.35", {"start": v(10.4, 0) * mm, "end": v(10, 0) * mm});
            skLineSegment(sketch, "E177.5.36", {"start": v(80.3, -15.6) * mm, "end": v(79.9, -15.53) * mm});
            skLineSegment(sketch, "E177.5.37", {"start": v(46.92, -9.12) * mm, "end": v(46.53, -9.04) * mm});
            skLineSegment(sketch, "E177.5.38", {"start": v(24, 0) * mm, "end": v(23.6, 0) * mm});
            skLineSegment(sketch, "E177.6.0", {"start": v(50.23, -29) * mm, "end": v(49.88, -28.8) * mm});
            skLineSegment(sketch, "E177.6.1", {"start": v(46.34, -40.28) * mm, "end": v(46.04, -40.02) * mm});
            skLineSegment(sketch, "E177.6.2", {"start": v(32.56, -18.8) * mm, "end": v(32.22, -18.6) * mm});
            skLineSegment(sketch, "E177.6.3", {"start": v(10.41, -9.05) * mm, "end": v(10.11, -8.8) * mm});
            skLineSegment(sketch, "E177.6.4", {"start": v(5.28, -4.6) * mm, "end": v(4.98, -4.33) * mm});
            skLineSegment(sketch, "E177.6.5", {"start": v(51.47, -44.74) * mm, "end": v(51.17, -44.48) * mm});
            skLineSegment(sketch, "E177.6.6", {"start": v(66.87, -58.13) * mm, "end": v(66.57, -57.86) * mm});
            skLineSegment(sketch, "E177.6.7", {"start": v(53.03, -53.03) * mm, "end": v(52.75, -52.75) * mm});
            skLineSegment(sketch, "E177.6.8", {"start": v(20.68, -17.98) * mm, "end": v(20.38, -17.71) * mm});
            skLineSegment(sketch, "E177.6.9", {"start": v(24.18, -24.18) * mm, "end": v(23.9, -23.9) * mm});
            skLineSegment(sketch, "E177.6.10", {"start": v(9.76, -9.76) * mm, "end": v(9.48, -9.48) * mm});
            skLineSegment(sketch, "E177.6.11", {"start": v(38.6, -38.6) * mm, "end": v(38.33, -38.33) * mm});
            skLineSegment(sketch, "E177.6.12", {"start": v(19.37, -19.37) * mm, "end": v(19.1, -19.1) * mm});
            skLineSegment(sketch, "E177.6.13", {"start": v(73.79, -42.6) * mm, "end": v(73.44, -42.4) * mm});
            skLineSegment(sketch, "E177.6.14", {"start": v(56.6, -49.2) * mm, "end": v(56.3, -48.94) * mm});
            skLineSegment(sketch, "E177.6.15", {"start": v(14.9, -8.6) * mm, "end": v(14.55, -8.4) * mm});
            skLineSegment(sketch, "E177.6.16", {"start": v(25.81, -22.44) * mm, "end": v(25.5, -22.17) * mm});
            skLineSegment(sketch, "E177.6.17", {"start": v(41.2, -35.82) * mm, "end": v(40.9, -35.56) * mm});
            skLineSegment(sketch, "E177.6.18", {"start": v(44.34, -25.6) * mm, "end": v(44, -25.4) * mm});
            skLineSegment(sketch, "E177.6.19", {"start": v(30.94, -26.9) * mm, "end": v(30.64, -26.64) * mm});
            skLineSegment(sketch, "E177.6.20", {"start": v(57.84, -57.84) * mm, "end": v(57.56, -57.56) * mm});
            skLineSegment(sketch, "E177.6.21", {"start": v(43.42, -43.42) * mm, "end": v(43.13, -43.13) * mm});
            skLineSegment(sketch, "E177.6.22", {"start": v(4.95, -4.95) * mm, "end": v(4.67, -4.67) * mm});
            skLineSegment(sketch, "E177.6.23", {"start": v(14.57, -14.57) * mm, "end": v(14.28, -14.28) * mm});
            skLineSegment(sketch, "E177.6.24", {"start": v(62, -35.8) * mm, "end": v(61.66, -35.6) * mm});
            skLineSegment(sketch, "E177.6.25", {"start": v(15.55, -13.51) * mm, "end": v(15.25, -13.25) * mm});
            skLineSegment(sketch, "E177.6.26", {"start": v(33.8, -33.8) * mm, "end": v(33.52, -33.52) * mm});
            skLineSegment(sketch, "E177.6.27", {"start": v(79.67, -46) * mm, "end": v(79.33, -45.8) * mm});
            skLineSegment(sketch, "E177.6.28", {"start": v(29, -29) * mm, "end": v(28.7, -28.7) * mm});
            skLineSegment(sketch, "E177.6.29", {"start": v(38.45, -22.2) * mm, "end": v(38.1, -22) * mm});
            skLineSegment(sketch, "E177.6.30", {"start": v(56.12, -32.4) * mm, "end": v(55.77, -32.2) * mm});
            skLineSegment(sketch, "E177.6.31", {"start": v(48.22, -48.22) * mm, "end": v(47.94, -47.94) * mm});
            skLineSegment(sketch, "E177.6.32", {"start": v(62.65, -62.65) * mm, "end": v(62.37, -62.37) * mm});
            skLineSegment(sketch, "E177.6.33", {"start": v(26.67, -15.4) * mm, "end": v(26.33, -15.2) * mm});
            skLineSegment(sketch, "E177.6.34", {"start": v(67.9, -39.2) * mm, "end": v(67.55, -39) * mm});
            skLineSegment(sketch, "E177.6.35", {"start": v(9, -5.2) * mm, "end": v(8.66, -5) * mm});
            skLineSegment(sketch, "E177.6.36", {"start": v(61.74, -53.67) * mm, "end": v(61.43, -53.4) * mm});
            skLineSegment(sketch, "E177.6.37", {"start": v(36.08, -31.36) * mm, "end": v(35.77, -31.1) * mm});
            skLineSegment(sketch, "E177.6.38", {"start": v(20.78, -12) * mm, "end": v(20.44, -11.8) * mm});
            skLineSegment(sketch, "E177.7.0", {"start": v(29, -50.23) * mm, "end": v(28.8, -49.88) * mm});
            skLineSegment(sketch, "E177.7.1", {"start": v(19.99, -58.05) * mm, "end": v(19.86, -57.68) * mm});
            skLineSegment(sketch, "E177.7.2", {"start": v(18.8, -32.56) * mm, "end": v(18.6, -32.22) * mm});
            skLineSegment(sketch, "E177.7.3", {"start": v(4.5, -13.05) * mm, "end": v(4.36, -12.67) * mm});
            skLineSegment(sketch, "E177.7.4", {"start": v(2.28, -6.62) * mm, "end": v(2.15, -6.24) * mm});
            skLineSegment(sketch, "E177.7.5", {"start": v(22.2, -64.48) * mm, "end": v(22.07, -64.1) * mm});
            skLineSegment(sketch, "E177.7.6", {"start": v(28.85, -83.77) * mm, "end": v(28.72, -83.4) * mm});
            skLineSegment(sketch, "E177.7.7", {"start": v(19.41, -72.44) * mm, "end": v(19.3, -72.06) * mm});
            skLineSegment(sketch, "E177.7.8", {"start": v(8.92, -25.9) * mm, "end": v(8.8, -25.53) * mm});
            skLineSegment(sketch, "E177.7.9", {"start": v(8.85, -33.03) * mm, "end": v(8.75, -32.65) * mm});
            skLineSegment(sketch, "E177.7.10", {"start": v(3.57, -13.33) * mm, "end": v(3.47, -12.94) * mm});
            skLineSegment(sketch, "E177.7.11", {"start": v(14.13, -52.74) * mm, "end": v(14.03, -52.35) * mm});
            skLineSegment(sketch, "E177.7.12", {"start": v(7.1, -26.47) * mm, "end": v(6.99, -26.08) * mm});
            skLineSegment(sketch, "E177.7.13", {"start": v(42.6, -73.79) * mm, "end": v(42.4, -73.44) * mm});
            skLineSegment(sketch, "E177.7.14", {"start": v(24.42, -70.91) * mm, "end": v(24.29, -70.54) * mm});
            skLineSegment(sketch, "E177.7.15", {"start": v(8.6, -14.9) * mm, "end": v(8.4, -14.55) * mm});
            skLineSegment(sketch, "E177.7.16", {"start": v(11.13, -32.34) * mm, "end": v(11, -31.96) * mm});
            skLineSegment(sketch, "E177.7.17", {"start": v(17.78, -51.63) * mm, "end": v(17.65, -51.25) * mm});
            skLineSegment(sketch, "E177.7.18", {"start": v(25.6, -44.34) * mm, "end": v(25.4, -44) * mm});
            skLineSegment(sketch, "E177.7.19", {"start": v(13.35, -38.77) * mm, "end": v(13.22, -38.39) * mm});
            skLineSegment(sketch, "E177.7.20", {"start": v(21.17, -79.01) * mm, "end": v(21.07, -78.63) * mm});
            skLineSegment(sketch, "E177.7.21", {"start": v(15.9, -59.3) * mm, "end": v(15.79, -58.92) * mm});
            skLineSegment(sketch, "E177.7.22", {"start": v(1.81, -6.76) * mm, "end": v(1.7, -6.38) * mm});
            skLineSegment(sketch, "E177.7.23", {"start": v(5.33, -19.9) * mm, "end": v(5.23, -19.51) * mm});
            skLineSegment(sketch, "E177.7.24", {"start": v(35.8, -62) * mm, "end": v(35.6, -61.66) * mm});
            skLineSegment(sketch, "E177.7.25", {"start": v(6.7, -19.48) * mm, "end": v(6.58, -19.1) * mm});
            skLineSegment(sketch, "E177.7.26", {"start": v(12.37, -46.17) * mm, "end": v(12.27, -45.78) * mm});
            skLineSegment(sketch, "E177.7.27", {"start": v(46, -79.67) * mm, "end": v(45.8, -79.33) * mm});
            skLineSegment(sketch, "E177.7.28", {"start": v(10.61, -39.6) * mm, "end": v(10.5, -39.22) * mm});
            skLineSegment(sketch, "E177.7.29", {"start": v(22.2, -38.45) * mm, "end": v(22, -38.1) * mm});
            skLineSegment(sketch, "E177.7.30", {"start": v(32.4, -56.12) * mm, "end": v(32.2, -55.77) * mm});
            skLineSegment(sketch, "E177.7.31", {"start": v(17.65, -65.88) * mm, "end": v(17.55, -65.49) * mm});
            skLineSegment(sketch, "E177.7.32", {"start": v(22.93, -85.58) * mm, "end": v(22.83, -85.2) * mm});
            skLineSegment(sketch, "E177.7.33", {"start": v(15.4, -26.67) * mm, "end": v(15.2, -26.33) * mm});
            skLineSegment(sketch, "E177.7.34", {"start": v(39.2, -67.9) * mm, "end": v(39, -67.55) * mm});
            skLineSegment(sketch, "E177.7.35", {"start": v(5.2, -9) * mm, "end": v(5, -8.66) * mm});
            skLineSegment(sketch, "E177.7.36", {"start": v(26.63, -77.34) * mm, "end": v(26.5, -76.97) * mm});
            skLineSegment(sketch, "E177.7.37", {"start": v(15.56, -45.2) * mm, "end": v(15.43, -44.82) * mm});
            skLineSegment(sketch, "E177.7.38", {"start": v(12, -20.78) * mm, "end": v(11.8, -20.44) * mm});
            skLineSegment(sketch, "E177.8.0", {"start": v(0, -58) * mm, "end": v(0, -57.6) * mm});
            skLineSegment(sketch, "E177.8.1", {"start": v(-11.72, -60.27) * mm, "end": v(-11.64, -59.88) * mm});
            skLineSegment(sketch, "E177.8.2", {"start": v(0, -37.6) * mm, "end": v(0, -37.2) * mm});
            skLineSegment(sketch, "E177.8.3", {"start": v(-2.63, -13.55) * mm, "end": v(-2.56, -13.15) * mm});
            skLineSegment(sketch, "E177.8.4", {"start": v(-1.34, -6.87) * mm, "end": v(-1.26, -6.48) * mm});
            skLineSegment(sketch, "E177.8.5", {"start": v(-13.01, -66.95) * mm, "end": v(-12.94, -66.55) * mm});
            skLineSegment(sketch, "E177.8.6", {"start": v(-16.9, -86.97) * mm, "end": v(-16.83, -86.58) * mm});
            skLineSegment(sketch, "E177.8.7", {"start": v(-19.41, -72.44) * mm, "end": v(-19.3, -72.06) * mm});
            skLineSegment(sketch, "E177.8.8", {"start": v(-5.23, -26.9) * mm, "end": v(-5.15, -26.5) * mm});
            skLineSegment(sketch, "E177.8.9", {"start": v(-8.85, -33.03) * mm, "end": v(-8.75, -32.65) * mm});
            skLineSegment(sketch, "E177.8.10", {"start": v(-3.57, -13.33) * mm, "end": v(-3.47, -12.94) * mm});
            skLineSegment(sketch, "E177.8.11", {"start": v(-14.13, -52.74) * mm, "end": v(-14.03, -52.35) * mm});
            skLineSegment(sketch, "E177.8.12", {"start": v(-7.1, -26.47) * mm, "end": v(-6.99, -26.08) * mm});
            skLineSegment(sketch, "E177.8.13", {"start": v(0, -85.2) * mm, "end": v(0, -84.8) * mm});
            skLineSegment(sketch, "E177.8.14", {"start": v(-14.31, -73.62) * mm, "end": v(-14.23, -73.23) * mm});
            skLineSegment(sketch, "E177.8.15", {"start": v(0, -17.2) * mm, "end": v(0, -16.8) * mm});
            skLineSegment(sketch, "E177.8.16", {"start": v(-6.53, -33.57) * mm, "end": v(-6.45, -33.18) * mm});
            skLineSegment(sketch, "E177.8.17", {"start": v(-10.42, -53.6) * mm, "end": v(-10.34, -53.2) * mm});
            skLineSegment(sketch, "E177.8.18", {"start": v(0, -51.2) * mm, "end": v(0, -50.8) * mm});
            skLineSegment(sketch, "E177.8.19", {"start": v(-7.82, -40.25) * mm, "end": v(-7.75, -39.85) * mm});
            skLineSegment(sketch, "E177.8.20", {"start": v(-21.17, -79.01) * mm, "end": v(-21.07, -78.63) * mm});
            skLineSegment(sketch, "E177.8.21", {"start": v(-15.9, -59.3) * mm, "end": v(-15.79, -58.92) * mm});
            skLineSegment(sketch, "E177.8.22", {"start": v(-1.81, -6.76) * mm, "end": v(-1.7, -6.38) * mm});
            skLineSegment(sketch, "E177.8.23", {"start": v(-5.33, -19.9) * mm, "end": v(-5.23, -19.51) * mm});
            skLineSegment(sketch, "E177.8.24", {"start": v(0, -71.6) * mm, "end": v(0, -71.2) * mm});
            skLineSegment(sketch, "E177.8.25", {"start": v(-3.93, -20.22) * mm, "end": v(-3.85, -19.83) * mm});
            skLineSegment(sketch, "E177.8.26", {"start": v(-12.37, -46.17) * mm, "end": v(-12.27, -45.78) * mm});
            skLineSegment(sketch, "E177.8.27", {"start": v(0, -92) * mm, "end": v(0, -91.6) * mm});
            skLineSegment(sketch, "E177.8.28", {"start": v(-10.61, -39.6) * mm, "end": v(-10.5, -39.22) * mm});
            skLineSegment(sketch, "E177.8.29", {"start": v(0, -44.4) * mm, "end": v(0, -44) * mm});
            skLineSegment(sketch, "E177.8.30", {"start": v(0, -64.8) * mm, "end": v(0, -64.4) * mm});
            skLineSegment(sketch, "E177.8.31", {"start": v(-17.65, -65.88) * mm, "end": v(-17.55, -65.49) * mm});
            skLineSegment(sketch, "E177.8.32", {"start": v(-22.93, -85.58) * mm, "end": v(-22.83, -85.2) * mm});
            skLineSegment(sketch, "E177.8.33", {"start": v(0, -30.8) * mm, "end": v(0, -30.4) * mm});
            skLineSegment(sketch, "E177.8.34", {"start": v(0, -78.4) * mm, "end": v(0, -78) * mm});
            skLineSegment(sketch, "E177.8.35", {"start": v(0, -10.4) * mm, "end": v(0, -10) * mm});
            skLineSegment(sketch, "E177.8.36", {"start": v(-15.6, -80.3) * mm, "end": v(-15.53, -79.9) * mm});
            skLineSegment(sketch, "E177.8.37", {"start": v(-9.12, -46.92) * mm, "end": v(-9.04, -46.53) * mm});
            skLineSegment(sketch, "E177.8.38", {"start": v(0, -24) * mm, "end": v(0, -23.6) * mm});
            skLineSegment(sketch, "E177.9.0", {"start": v(-29, -50.23) * mm, "end": v(-28.8, -49.88) * mm});
            skLineSegment(sketch, "E177.9.1", {"start": v(-40.28, -46.34) * mm, "end": v(-40.02, -46.04) * mm});
            skLineSegment(sketch, "E177.9.2", {"start": v(-18.8, -32.56) * mm, "end": v(-18.6, -32.22) * mm});
            skLineSegment(sketch, "E177.9.3", {"start": v(-9.05, -10.41) * mm, "end": v(-8.8, -10.11) * mm});
            skLineSegment(sketch, "E177.9.4", {"start": v(-4.6, -5.28) * mm, "end": v(-4.33, -4.98) * mm});
            skLineSegment(sketch, "E177.9.5", {"start": v(-44.74, -51.47) * mm, "end": v(-44.48, -51.17) * mm});
            skLineSegment(sketch, "E177.9.6", {"start": v(-58.13, -66.87) * mm, "end": v(-57.86, -66.57) * mm});
            skLineSegment(sketch, "E177.9.7", {"start": v(-53.03, -53.03) * mm, "end": v(-52.75, -52.75) * mm});
            skLineSegment(sketch, "E177.9.8", {"start": v(-17.98, -20.68) * mm, "end": v(-17.71, -20.38) * mm});
            skLineSegment(sketch, "E177.9.9", {"start": v(-24.18, -24.18) * mm, "end": v(-23.9, -23.9) * mm});
            skLineSegment(sketch, "E177.9.10", {"start": v(-9.76, -9.76) * mm, "end": v(-9.48, -9.48) * mm});
            skLineSegment(sketch, "E177.9.11", {"start": v(-38.6, -38.6) * mm, "end": v(-38.33, -38.33) * mm});
            skLineSegment(sketch, "E177.9.12", {"start": v(-19.37, -19.37) * mm, "end": v(-19.1, -19.1) * mm});
            skLineSegment(sketch, "E177.9.13", {"start": v(-42.6, -73.79) * mm, "end": v(-42.4, -73.44) * mm});
            skLineSegment(sketch, "E177.9.14", {"start": v(-49.2, -56.6) * mm, "end": v(-48.94, -56.3) * mm});
            skLineSegment(sketch, "E177.9.15", {"start": v(-8.6, -14.9) * mm, "end": v(-8.4, -14.55) * mm});
            skLineSegment(sketch, "E177.9.16", {"start": v(-22.44, -25.81) * mm, "end": v(-22.17, -25.5) * mm});
            skLineSegment(sketch, "E177.9.17", {"start": v(-35.82, -41.2) * mm, "end": v(-35.56, -40.9) * mm});
            skLineSegment(sketch, "E177.9.18", {"start": v(-25.6, -44.34) * mm, "end": v(-25.4, -44) * mm});
            skLineSegment(sketch, "E177.9.19", {"start": v(-26.9, -30.94) * mm, "end": v(-26.64, -30.64) * mm});
            skLineSegment(sketch, "E177.9.20", {"start": v(-57.84, -57.84) * mm, "end": v(-57.56, -57.56) * mm});
            skLineSegment(sketch, "E177.9.21", {"start": v(-43.42, -43.42) * mm, "end": v(-43.13, -43.13) * mm});
            skLineSegment(sketch, "E177.9.22", {"start": v(-4.95, -4.95) * mm, "end": v(-4.67, -4.67) * mm});
            skLineSegment(sketch, "E177.9.23", {"start": v(-14.57, -14.57) * mm, "end": v(-14.28, -14.28) * mm});
            skLineSegment(sketch, "E177.9.24", {"start": v(-35.8, -62) * mm, "end": v(-35.6, -61.66) * mm});
            skLineSegment(sketch, "E177.9.25", {"start": v(-13.51, -15.55) * mm, "end": v(-13.25, -15.25) * mm});
            skLineSegment(sketch, "E177.9.26", {"start": v(-33.8, -33.8) * mm, "end": v(-33.52, -33.52) * mm});
            skLineSegment(sketch, "E177.9.27", {"start": v(-46, -79.67) * mm, "end": v(-45.8, -79.33) * mm});
            skLineSegment(sketch, "E177.9.28", {"start": v(-29, -29) * mm, "end": v(-28.7, -28.7) * mm});
            skLineSegment(sketch, "E177.9.29", {"start": v(-22.2, -38.45) * mm, "end": v(-22, -38.1) * mm});
            skLineSegment(sketch, "E177.9.30", {"start": v(-32.4, -56.12) * mm, "end": v(-32.2, -55.77) * mm});
            skLineSegment(sketch, "E177.9.31", {"start": v(-48.22, -48.22) * mm, "end": v(-47.94, -47.94) * mm});
            skLineSegment(sketch, "E177.9.32", {"start": v(-62.65, -62.65) * mm, "end": v(-62.37, -62.37) * mm});
            skLineSegment(sketch, "E177.9.33", {"start": v(-15.4, -26.67) * mm, "end": v(-15.2, -26.33) * mm});
            skLineSegment(sketch, "E177.9.34", {"start": v(-39.2, -67.9) * mm, "end": v(-39, -67.55) * mm});
            skLineSegment(sketch, "E177.9.35", {"start": v(-5.2, -9) * mm, "end": v(-5, -8.66) * mm});
            skLineSegment(sketch, "E177.9.36", {"start": v(-53.67, -61.74) * mm, "end": v(-53.4, -61.43) * mm});
            skLineSegment(sketch, "E177.9.37", {"start": v(-31.36, -36.08) * mm, "end": v(-31.1, -35.77) * mm});
            skLineSegment(sketch, "E177.9.38", {"start": v(-12, -20.78) * mm, "end": v(-11.8, -20.44) * mm});
            skLineSegment(sketch, "E177.10.0", {"start": v(-50.23, -29) * mm, "end": v(-49.88, -28.8) * mm});
            skLineSegment(sketch, "E177.10.1", {"start": v(-58.05, -19.99) * mm, "end": v(-57.68, -19.86) * mm});
            skLineSegment(sketch, "E177.10.2", {"start": v(-32.56, -18.8) * mm, "end": v(-32.22, -18.6) * mm});
            skLineSegment(sketch, "E177.10.3", {"start": v(-13.05, -4.5) * mm, "end": v(-12.67, -4.36) * mm});
            skLineSegment(sketch, "E177.10.4", {"start": v(-6.62, -2.28) * mm, "end": v(-6.24, -2.15) * mm});
            skLineSegment(sketch, "E177.10.5", {"start": v(-64.48, -22.2) * mm, "end": v(-64.1, -22.07) * mm});
            skLineSegment(sketch, "E177.10.6", {"start": v(-83.77, -28.85) * mm, "end": v(-83.4, -28.72) * mm});
            skLineSegment(sketch, "E177.10.8", {"start": v(-25.9, -8.92) * mm, "end": v(-25.53, -8.8) * mm});
            skLineSegment(sketch, "E177.10.13", {"start": v(-73.79, -42.6) * mm, "end": v(-73.44, -42.4) * mm});
            skLineSegment(sketch, "E177.10.14", {"start": v(-70.91, -24.42) * mm, "end": v(-70.54, -24.29) * mm});
            skLineSegment(sketch, "E177.10.15", {"start": v(-14.9, -8.6) * mm, "end": v(-14.55, -8.4) * mm});
            skLineSegment(sketch, "E177.10.16", {"start": v(-32.34, -11.13) * mm, "end": v(-31.96, -11) * mm});
            skLineSegment(sketch, "E177.10.17", {"start": v(-51.63, -17.78) * mm, "end": v(-51.25, -17.65) * mm});
            skLineSegment(sketch, "E177.10.18", {"start": v(-44.34, -25.6) * mm, "end": v(-44, -25.4) * mm});
            skLineSegment(sketch, "E177.10.19", {"start": v(-38.77, -13.35) * mm, "end": v(-38.39, -13.22) * mm});
            skLineSegment(sketch, "E177.10.24", {"start": v(-62, -35.8) * mm, "end": v(-61.66, -35.6) * mm});
            skLineSegment(sketch, "E177.10.25", {"start": v(-19.48, -6.7) * mm, "end": v(-19.1, -6.58) * mm});
            skLineSegment(sketch, "E177.10.27", {"start": v(-79.67, -46) * mm, "end": v(-79.33, -45.8) * mm});
            skLineSegment(sketch, "E177.10.29", {"start": v(-38.45, -22.2) * mm, "end": v(-38.1, -22) * mm});
            skLineSegment(sketch, "E177.10.30", {"start": v(-56.12, -32.4) * mm, "end": v(-55.77, -32.2) * mm});
            skLineSegment(sketch, "E177.10.33", {"start": v(-26.67, -15.4) * mm, "end": v(-26.33, -15.2) * mm});
            skLineSegment(sketch, "E177.10.34", {"start": v(-67.9, -39.2) * mm, "end": v(-67.55, -39) * mm});
            skLineSegment(sketch, "E177.10.35", {"start": v(-9, -5.2) * mm, "end": v(-8.66, -5) * mm});
            skLineSegment(sketch, "E177.10.36", {"start": v(-77.34, -26.63) * mm, "end": v(-76.97, -26.5) * mm});
            skLineSegment(sketch, "E177.10.37", {"start": v(-45.2, -15.56) * mm, "end": v(-44.82, -15.43) * mm});
            skLineSegment(sketch, "E177.10.38", {"start": v(-20.78, -12) * mm, "end": v(-20.44, -11.8) * mm});
            skLineSegment(sketch, "E177.11.7", {"start": v(-72.44, 19.41) * mm, "end": v(-72.06, 19.3) * mm});
            skLineSegment(sketch, "E177.11.9", {"start": v(-33.03, 8.85) * mm, "end": v(-32.65, 8.75) * mm});
            skLineSegment(sketch, "E177.11.10", {"start": v(-13.33, 3.57) * mm, "end": v(-12.94, 3.47) * mm});
            skLineSegment(sketch, "E177.11.11", {"start": v(-52.74, 14.13) * mm, "end": v(-52.35, 14.03) * mm});
            skLineSegment(sketch, "E177.11.12", {"start": v(-26.47, 7.1) * mm, "end": v(-26.08, 6.99) * mm});
            skLineSegment(sketch, "E177.11.20", {"start": v(-79.01, 21.17) * mm, "end": v(-78.63, 21.07) * mm});
            skLineSegment(sketch, "E177.11.21", {"start": v(-59.3, 15.9) * mm, "end": v(-58.92, 15.79) * mm});
            skLineSegment(sketch, "E177.11.22", {"start": v(-6.76, 1.81) * mm, "end": v(-6.38, 1.7) * mm});
            skLineSegment(sketch, "E177.11.23", {"start": v(-19.9, 5.33) * mm, "end": v(-19.51, 5.23) * mm});
            skLineSegment(sketch, "E177.11.26", {"start": v(-46.17, 12.37) * mm, "end": v(-45.78, 12.27) * mm});
            skLineSegment(sketch, "E177.11.28", {"start": v(-39.6, 10.61) * mm, "end": v(-39.22, 10.5) * mm});
            skLineSegment(sketch, "E177.11.31", {"start": v(-65.88, 17.65) * mm, "end": v(-65.49, 17.55) * mm});
            skLineSegment(sketch, "E177.11.32", {"start": v(-85.58, 22.93) * mm, "end": v(-85.2, 22.83) * mm});
            skLineSegment(sketch, "E177.anchor1", {"start": v(0, 0) * mm, "end": v(-79.67, 46) * mm, "construction": true});
            skLineSegment(sketch, "E178", {"start": v(-47.64, 70.63) * mm, "end": v(-47.42, 70.3) * mm});
            skLineSegment(sketch, "E179", {"start": v(-43.84, 65) * mm, "end": v(-43.62, 64.66) * mm});
            skLineSegment(sketch, "E180", {"start": v(-40.04, 59.36) * mm, "end": v(-39.81, 59.03) * mm});
            skLineSegment(sketch, "E181", {"start": v(-36.24, 53.72) * mm, "end": v(-36.01, 53.4) * mm});
            skLineSegment(sketch, "E182", {"start": v(-32.43, 48.08) * mm, "end": v(-32.2, 47.75) * mm});
            skLineSegment(sketch, "E183", {"start": v(-28.63, 42.45) * mm, "end": v(-28.4, 42.12) * mm});
            skLineSegment(sketch, "E184", {"start": v(-24.83, 36.8) * mm, "end": v(-24.6, 36.48) * mm});
            skLineSegment(sketch, "E185", {"start": v(-21.03, 31.17) * mm, "end": v(-20.8, 30.84) * mm});
            skLineSegment(sketch, "E186", {"start": v(-17.22, 25.53) * mm, "end": v(-17, 25.2) * mm});
            skLineSegment(sketch, "E187", {"start": v(-13.42, 19.9) * mm, "end": v(-13.2, 19.57) * mm});
            skLineSegment(sketch, "E188", {"start": v(-9.62, 14.26) * mm, "end": v(-9.4, 13.93) * mm});
            skLineSegment(sketch, "E189", {"start": v(-5.82, 8.62) * mm, "end": v(-5.6, 8.3) * mm});
            skLineSegment(sketch, "E190.1.0", {"start": v(-5, 71.43) * mm, "end": v(-4.97, 71.03) * mm});
            skLineSegment(sketch, "E190.1.1", {"start": v(-2.62, 37.5) * mm, "end": v(-2.6, 37.1) * mm});
            skLineSegment(sketch, "E190.1.2", {"start": v(-5.94, 85) * mm, "end": v(-5.92, 84.6) * mm});
            skLineSegment(sketch, "E190.1.3", {"start": v(-1.67, 23.94) * mm, "end": v(-1.65, 23.54) * mm});
            skLineSegment(sketch, "E190.1.4", {"start": v(-2.15, 30.72) * mm, "end": v(-2.12, 30.33) * mm});
            skLineSegment(sketch, "E190.1.5", {"start": v(-4.05, 57.86) * mm, "end": v(-4.02, 57.46) * mm});
            skLineSegment(sketch, "E190.1.6", {"start": v(-0.73, 10.37) * mm, "end": v(-0.7, 9.98) * mm});
            skLineSegment(sketch, "E190.1.7", {"start": v(-4.52, 64.64) * mm, "end": v(-4.5, 64.24) * mm});
            skLineSegment(sketch, "E190.1.8", {"start": v(-3.1, 44.3) * mm, "end": v(-3.07, 43.9) * mm});
            skLineSegment(sketch, "E190.1.9", {"start": v(-1.2, 17.16) * mm, "end": v(-1.17, 16.76) * mm});
            skLineSegment(sketch, "E190.1.10", {"start": v(-3.57, 51.08) * mm, "end": v(-3.54, 50.68) * mm});
            skLineSegment(sketch, "E190.1.11", {"start": v(-5.47, 78.2) * mm, "end": v(-5.44, 77.8) * mm});
            skLineSegment(sketch, "E190.2.0", {"start": v(31.39, 64.35) * mm, "end": v(31.21, 64) * mm});
            skLineSegment(sketch, "E190.2.1", {"start": v(16.48, 33.8) * mm, "end": v(16.3, 33.44) * mm});
            skLineSegment(sketch, "E190.2.2", {"start": v(37.35, 76.58) * mm, "end": v(37.17, 76.22) * mm});
            skLineSegment(sketch, "E190.2.3", {"start": v(10.52, 21.57) * mm, "end": v(10.35, 21.21) * mm});
            skLineSegment(sketch, "E190.2.4", {"start": v(13.5, 27.68) * mm, "end": v(13.33, 27.32) * mm});
            skLineSegment(sketch, "E190.2.5", {"start": v(25.43, 52.13) * mm, "end": v(25.25, 51.77) * mm});
            skLineSegment(sketch, "E190.2.6", {"start": v(4.56, 9.35) * mm, "end": v(4.38, 8.99) * mm});
            skLineSegment(sketch, "E190.2.7", {"start": v(28.4, 58.24) * mm, "end": v(28.23, 57.88) * mm});
            skLineSegment(sketch, "E190.2.8", {"start": v(19.46, 39.9) * mm, "end": v(19.29, 39.55) * mm});
            skLineSegment(sketch, "E190.2.9", {"start": v(7.54, 15.46) * mm, "end": v(7.36, 15.1) * mm});
            skLineSegment(sketch, "E190.2.10", {"start": v(22.44, 46.02) * mm, "end": v(22.27, 45.66) * mm});
            skLineSegment(sketch, "E190.2.11", {"start": v(34.37, 70.47) * mm, "end": v(34.2, 70.1) * mm});
            skLineSegment(sketch, "E190.3.0", {"start": v(59.36, 40.04) * mm, "end": v(59.03, 39.81) * mm});
            skLineSegment(sketch, "E190.3.1", {"start": v(31.17, 21.03) * mm, "end": v(30.84, 20.8) * mm});
            skLineSegment(sketch, "E190.3.2", {"start": v(70.63, 47.64) * mm, "end": v(70.3, 47.42) * mm});
            skLineSegment(sketch, "E190.3.3", {"start": v(19.9, 13.42) * mm, "end": v(19.57, 13.2) * mm});
            skLineSegment(sketch, "E190.3.4", {"start": v(25.53, 17.22) * mm, "end": v(25.2, 17) * mm});
            skLineSegment(sketch, "E190.3.5", {"start": v(48.08, 32.43) * mm, "end": v(47.75, 32.2) * mm});
            skLineSegment(sketch, "E190.3.6", {"start": v(8.62, 5.82) * mm, "end": v(8.3, 5.6) * mm});
            skLineSegment(sketch, "E190.3.7", {"start": v(53.72, 36.24) * mm, "end": v(53.4, 36.01) * mm});
            skLineSegment(sketch, "E190.3.8", {"start": v(36.8, 24.83) * mm, "end": v(36.48, 24.6) * mm});
            skLineSegment(sketch, "E190.3.9", {"start": v(14.26, 9.62) * mm, "end": v(13.93, 9.4) * mm});
            skLineSegment(sketch, "E190.3.10", {"start": v(42.45, 28.63) * mm, "end": v(42.12, 28.4) * mm});
            skLineSegment(sketch, "E190.3.11", {"start": v(65, 43.84) * mm, "end": v(64.66, 43.62) * mm});
            skLineSegment(sketch, "E190.4.0", {"start": v(71.43, 5) * mm, "end": v(71.03, 4.97) * mm});
            skLineSegment(sketch, "E190.4.1", {"start": v(37.5, 2.62) * mm, "end": v(37.1, 2.6) * mm});
            skLineSegment(sketch, "E190.4.2", {"start": v(85, 5.94) * mm, "end": v(84.6, 5.92) * mm});
            skLineSegment(sketch, "E190.4.3", {"start": v(23.94, 1.67) * mm, "end": v(23.54, 1.65) * mm});
            skLineSegment(sketch, "E190.4.4", {"start": v(30.72, 2.15) * mm, "end": v(30.33, 2.12) * mm});
            skLineSegment(sketch, "E190.4.5", {"start": v(57.86, 4.05) * mm, "end": v(57.46, 4.02) * mm});
            skLineSegment(sketch, "E190.4.6", {"start": v(10.37, 0.73) * mm, "end": v(9.98, 0.7) * mm});
            skLineSegment(sketch, "E190.4.7", {"start": v(64.64, 4.52) * mm, "end": v(64.24, 4.5) * mm});
            skLineSegment(sketch, "E190.4.8", {"start": v(44.3, 3.1) * mm, "end": v(43.9, 3.07) * mm});
            skLineSegment(sketch, "E190.4.9", {"start": v(17.16, 1.2) * mm, "end": v(16.76, 1.17) * mm});
            skLineSegment(sketch, "E190.4.10", {"start": v(51.08, 3.57) * mm, "end": v(50.68, 3.54) * mm});
            skLineSegment(sketch, "E190.4.11", {"start": v(78.2, 5.47) * mm, "end": v(77.8, 5.44) * mm});
            skLineSegment(sketch, "E190.5.0", {"start": v(64.35, -31.39) * mm, "end": v(64, -31.21) * mm});
            skLineSegment(sketch, "E190.5.1", {"start": v(33.8, -16.48) * mm, "end": v(33.44, -16.3) * mm});
            skLineSegment(sketch, "E190.5.2", {"start": v(76.58, -37.35) * mm, "end": v(76.22, -37.17) * mm});
            skLineSegment(sketch, "E190.5.3", {"start": v(21.57, -10.52) * mm, "end": v(21.21, -10.35) * mm});
            skLineSegment(sketch, "E190.5.4", {"start": v(27.68, -13.5) * mm, "end": v(27.32, -13.33) * mm});
            skLineSegment(sketch, "E190.5.5", {"start": v(52.13, -25.43) * mm, "end": v(51.77, -25.25) * mm});
            skLineSegment(sketch, "E190.5.6", {"start": v(9.35, -4.56) * mm, "end": v(8.99, -4.38) * mm});
            skLineSegment(sketch, "E190.5.7", {"start": v(58.24, -28.4) * mm, "end": v(57.88, -28.23) * mm});
            skLineSegment(sketch, "E190.5.8", {"start": v(39.9, -19.46) * mm, "end": v(39.55, -19.29) * mm});
            skLineSegment(sketch, "E190.5.9", {"start": v(15.46, -7.54) * mm, "end": v(15.1, -7.36) * mm});
            skLineSegment(sketch, "E190.5.10", {"start": v(46.02, -22.44) * mm, "end": v(45.66, -22.27) * mm});
            skLineSegment(sketch, "E190.5.11", {"start": v(70.47, -34.37) * mm, "end": v(70.1, -34.2) * mm});
            skLineSegment(sketch, "E190.6.0", {"start": v(40.04, -59.36) * mm, "end": v(39.81, -59.03) * mm});
            skLineSegment(sketch, "E190.6.1", {"start": v(21.03, -31.17) * mm, "end": v(20.8, -30.84) * mm});
            skLineSegment(sketch, "E190.6.2", {"start": v(47.64, -70.63) * mm, "end": v(47.42, -70.3) * mm});
            skLineSegment(sketch, "E190.6.3", {"start": v(13.42, -19.9) * mm, "end": v(13.2, -19.57) * mm});
            skLineSegment(sketch, "E190.6.4", {"start": v(17.22, -25.53) * mm, "end": v(17, -25.2) * mm});
            skLineSegment(sketch, "E190.6.5", {"start": v(32.43, -48.08) * mm, "end": v(32.2, -47.75) * mm});
            skLineSegment(sketch, "E190.6.6", {"start": v(5.82, -8.62) * mm, "end": v(5.6, -8.3) * mm});
            skLineSegment(sketch, "E190.6.7", {"start": v(36.24, -53.72) * mm, "end": v(36.01, -53.4) * mm});
            skLineSegment(sketch, "E190.6.8", {"start": v(24.83, -36.8) * mm, "end": v(24.6, -36.48) * mm});
            skLineSegment(sketch, "E190.6.9", {"start": v(9.62, -14.26) * mm, "end": v(9.4, -13.93) * mm});
            skLineSegment(sketch, "E190.6.10", {"start": v(28.63, -42.45) * mm, "end": v(28.4, -42.12) * mm});
            skLineSegment(sketch, "E190.6.11", {"start": v(43.84, -65) * mm, "end": v(43.62, -64.66) * mm});
            skLineSegment(sketch, "E190.7.0", {"start": v(5, -71.43) * mm, "end": v(4.97, -71.03) * mm});
            skLineSegment(sketch, "E190.7.1", {"start": v(2.62, -37.5) * mm, "end": v(2.6, -37.1) * mm});
            skLineSegment(sketch, "E190.7.2", {"start": v(5.94, -85) * mm, "end": v(5.92, -84.6) * mm});
            skLineSegment(sketch, "E190.7.3", {"start": v(1.67, -23.94) * mm, "end": v(1.65, -23.54) * mm});
            skLineSegment(sketch, "E190.7.4", {"start": v(2.15, -30.72) * mm, "end": v(2.12, -30.33) * mm});
            skLineSegment(sketch, "E190.7.5", {"start": v(4.05, -57.86) * mm, "end": v(4.02, -57.46) * mm});
            skLineSegment(sketch, "E190.7.6", {"start": v(0.73, -10.37) * mm, "end": v(0.7, -9.98) * mm});
            skLineSegment(sketch, "E190.7.7", {"start": v(4.52, -64.64) * mm, "end": v(4.5, -64.24) * mm});
            skLineSegment(sketch, "E190.7.8", {"start": v(3.1, -44.3) * mm, "end": v(3.07, -43.9) * mm});
            skLineSegment(sketch, "E190.7.9", {"start": v(1.2, -17.16) * mm, "end": v(1.17, -16.76) * mm});
            skLineSegment(sketch, "E190.7.10", {"start": v(3.57, -51.08) * mm, "end": v(3.54, -50.68) * mm});
            skLineSegment(sketch, "E190.7.11", {"start": v(5.47, -78.2) * mm, "end": v(5.44, -77.8) * mm});
            skLineSegment(sketch, "E190.8.0", {"start": v(-31.39, -64.35) * mm, "end": v(-31.21, -64) * mm});
            skLineSegment(sketch, "E190.8.1", {"start": v(-16.48, -33.8) * mm, "end": v(-16.3, -33.44) * mm});
            skLineSegment(sketch, "E190.8.2", {"start": v(-37.35, -76.58) * mm, "end": v(-37.17, -76.22) * mm});
            skLineSegment(sketch, "E190.8.3", {"start": v(-10.52, -21.57) * mm, "end": v(-10.35, -21.21) * mm});
            skLineSegment(sketch, "E190.8.4", {"start": v(-13.5, -27.68) * mm, "end": v(-13.33, -27.32) * mm});
            skLineSegment(sketch, "E190.8.5", {"start": v(-25.43, -52.13) * mm, "end": v(-25.25, -51.77) * mm});
            skLineSegment(sketch, "E190.8.6", {"start": v(-4.56, -9.35) * mm, "end": v(-4.38, -8.99) * mm});
            skLineSegment(sketch, "E190.8.7", {"start": v(-28.4, -58.24) * mm, "end": v(-28.23, -57.88) * mm});
            skLineSegment(sketch, "E190.8.8", {"start": v(-19.46, -39.9) * mm, "end": v(-19.29, -39.55) * mm});
            skLineSegment(sketch, "E190.8.9", {"start": v(-7.54, -15.46) * mm, "end": v(-7.36, -15.1) * mm});
            skLineSegment(sketch, "E190.8.10", {"start": v(-22.44, -46.02) * mm, "end": v(-22.27, -45.66) * mm});
            skLineSegment(sketch, "E190.8.11", {"start": v(-34.37, -70.47) * mm, "end": v(-34.2, -70.1) * mm});
            skLineSegment(sketch, "E190.9.0", {"start": v(-59.36, -40.04) * mm, "end": v(-59.03, -39.81) * mm});
            skLineSegment(sketch, "E190.9.1", {"start": v(-31.17, -21.03) * mm, "end": v(-30.84, -20.8) * mm});
            skLineSegment(sketch, "E190.9.2", {"start": v(-70.63, -47.64) * mm, "end": v(-70.3, -47.42) * mm});
            skLineSegment(sketch, "E190.9.3", {"start": v(-19.9, -13.42) * mm, "end": v(-19.57, -13.2) * mm});
            skLineSegment(sketch, "E190.9.4", {"start": v(-25.53, -17.22) * mm, "end": v(-25.2, -17) * mm});
            skLineSegment(sketch, "E190.9.5", {"start": v(-48.08, -32.43) * mm, "end": v(-47.75, -32.2) * mm});
            skLineSegment(sketch, "E190.9.6", {"start": v(-8.62, -5.82) * mm, "end": v(-8.3, -5.6) * mm});
            skLineSegment(sketch, "E190.9.7", {"start": v(-53.72, -36.24) * mm, "end": v(-53.4, -36.01) * mm});
            skLineSegment(sketch, "E190.9.8", {"start": v(-36.8, -24.83) * mm, "end": v(-36.48, -24.6) * mm});
            skLineSegment(sketch, "E190.9.9", {"start": v(-14.26, -9.62) * mm, "end": v(-13.93, -9.4) * mm});
            skLineSegment(sketch, "E190.9.10", {"start": v(-42.45, -28.63) * mm, "end": v(-42.12, -28.4) * mm});
            skLineSegment(sketch, "E190.9.11", {"start": v(-65, -43.84) * mm, "end": v(-64.66, -43.62) * mm});
            skLineSegment(sketch, "E190.10.0", {"start": v(-71.43, -5) * mm, "end": v(-71.03, -4.97) * mm});
            skLineSegment(sketch, "E190.10.1", {"start": v(-37.5, -2.62) * mm, "end": v(-37.1, -2.6) * mm});
            skLineSegment(sketch, "E190.10.2", {"start": v(-85, -5.94) * mm, "end": v(-84.6, -5.92) * mm});
            skLineSegment(sketch, "E190.10.3", {"start": v(-23.94, -1.67) * mm, "end": v(-23.54, -1.65) * mm});
            skLineSegment(sketch, "E190.10.4", {"start": v(-30.72, -2.15) * mm, "end": v(-30.33, -2.12) * mm});
            skLineSegment(sketch, "E190.10.5", {"start": v(-57.86, -4.05) * mm, "end": v(-57.46, -4.02) * mm});
            skLineSegment(sketch, "E190.10.6", {"start": v(-10.37, -0.73) * mm, "end": v(-9.98, -0.7) * mm});
            skLineSegment(sketch, "E190.10.7", {"start": v(-64.64, -4.52) * mm, "end": v(-64.24, -4.5) * mm});
            skLineSegment(sketch, "E190.10.8", {"start": v(-44.3, -3.1) * mm, "end": v(-43.9, -3.07) * mm});
            skLineSegment(sketch, "E190.10.9", {"start": v(-17.16, -1.2) * mm, "end": v(-16.76, -1.17) * mm});
            skLineSegment(sketch, "E190.10.10", {"start": v(-51.08, -3.57) * mm, "end": v(-50.68, -3.54) * mm});
            skLineSegment(sketch, "E190.10.11", {"start": v(-78.2, -5.47) * mm, "end": v(-77.8, -5.44) * mm});
            skLineSegment(sketch, "E190.anchor1", {"start": v(0, 0) * mm, "end": v(-5.82, 8.62) * mm, "construction": true});
            skLineSegment(sketch, "E190.anchor2", {"start": v(0, 0) * mm, "end": v(-9.35, 4.56) * mm, "construction": true});
            skSolve(sketch);
        }
        {
            var Q0;
            Q0=makeQuery(id+"F1.imprint","IMPRINT",FACE,{"disambiguationData":[TD([[makeQuery(id+"F1.imprint","IMPRINT",EDGE,{"derivedFrom":sQuery(id+"F1.wireOp",EDGE,"E0")}),1.0]])]});
            extrude(context, id + "F2", {"entities" : qUnion([Q0]), "depth" : getVariable(context, 'T') * mm});
        }
    });
